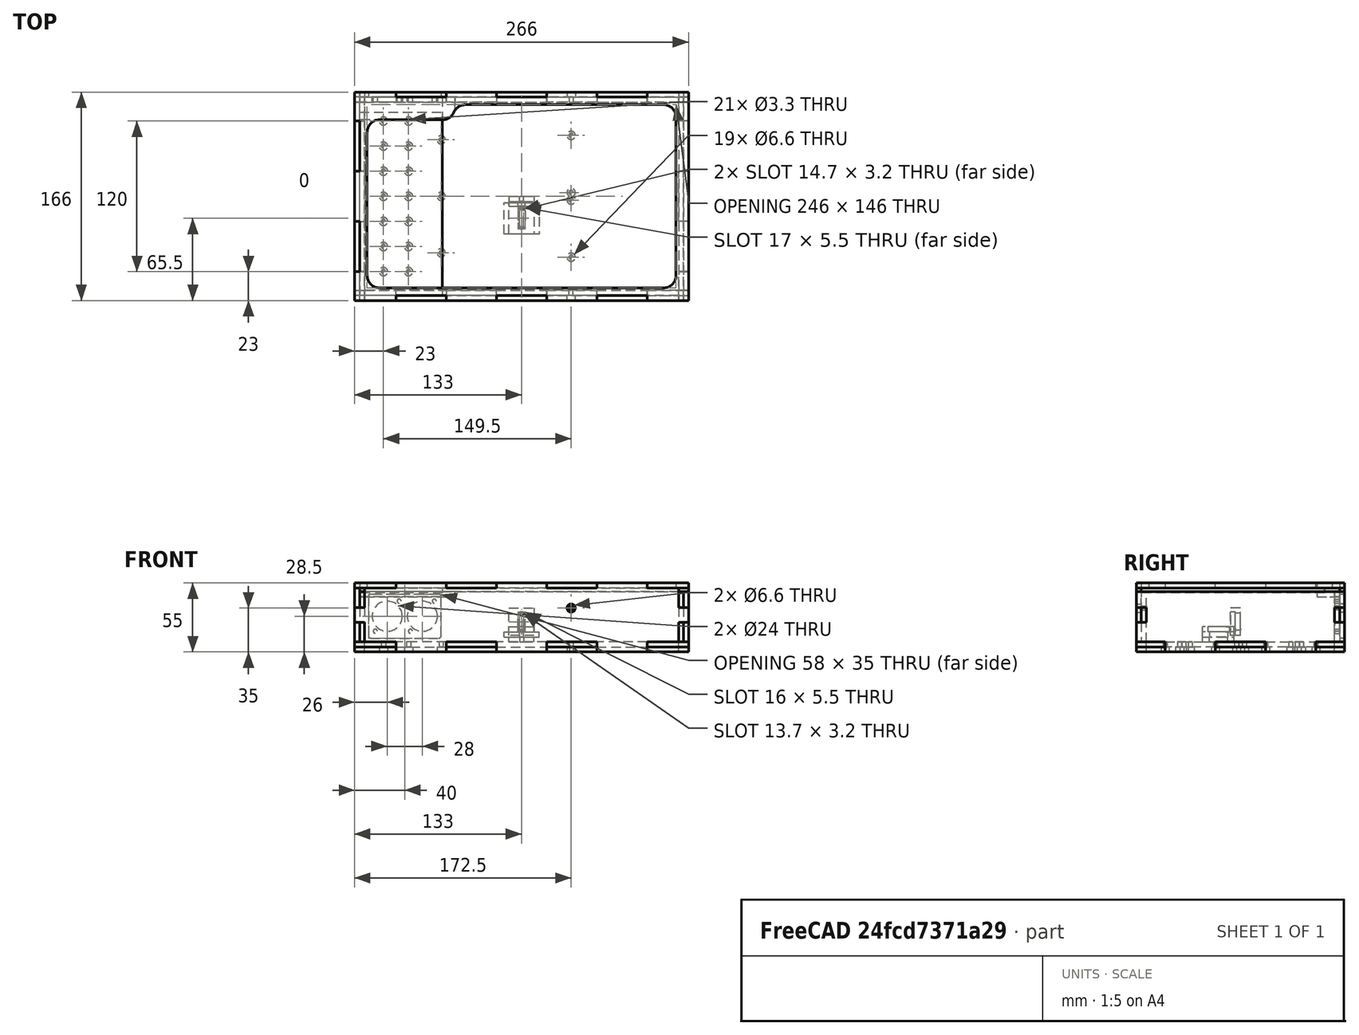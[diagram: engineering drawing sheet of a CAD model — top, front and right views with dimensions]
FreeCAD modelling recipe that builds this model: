
FCSTD DOCUMENT  (FreeCAD 0.17R13312 (Git))
Label: BreadBoardBox
License: All rights reserved
LicenseURL: http://en.wikipedia.org/wiki/All_rights_reserved
objects: Sketcher::SketchObject×62, PartDesign::ShapeBinder×61, PartDesign::Body×25, PartDesign::Pad×24, PartDesign::Pocket×24, TechDraw::DrawSVGTemplate×24, TechDraw::DrawViewPart×24, TechDraw::DrawPage×24, PartDesign::Plane×19, App::Part×18, PartDesign::FeatureBase×7, PartDesign::Hole×6, PartDesign::Mirrored×5, PartDesign::LinearPattern×5, PartDesign::MultiTransform×3, TechDraw::DrawViewDimension×3, App::DocumentObjectGroup×1
note: 295 computed .brp shape members not serialized (recipe doc carries the construction recipe); baked Part::Feature solids carry a one-line shape summary decoded from their .brp

FEATURE [Sketcher::SketchObject] Sketch  label="InsideSize_XY_Sketch"
  MapMode = 5
  Support = -> [XY_Plane026]
  sketch-geometry (4):
    g0: LineSegment StartX=-125 StartY=75 StartZ=0 EndX=125 EndY=75 EndZ=0
    g1: LineSegment StartX=125 StartY=75 StartZ=0 EndX=125 EndY=-75 EndZ=0
    g2: LineSegment StartX=125 StartY=-75 StartZ=0 EndX=-125 EndY=-75 EndZ=0
    g3: LineSegment StartX=-125 StartY=-75 StartZ=0 EndX=-125 EndY=75 EndZ=0
  constraints (11):
    c: Coincident(g0,g1)
    c: Coincident(g1,g2)
    c: Coincident(g2,g3)
    c: Coincident(g3,g0)
    c: Horizontal(g0)
    c: Horizontal(g2)
    c: Vertical(g1)
    c: Vertical(g3)
    c: Symmetric(g0,g2,g-1)
    c: DistanceX(g0,g0) = 250
    c: DistanceY(g1,g1) = 150
FEATURE [Sketcher::SketchObject] Sketch001  label="BaseIn_Sketch"
  MapMode = 5
  Support = -> [XY_Plane019]
  expr: Constraints[9] = 250 + 4 * 4
  expr: Constraints[8] = 150 + 4 * 4
  sketch-geometry (4):
    g0: LineSegment StartX=-133 StartY=83 StartZ=0 EndX=133 EndY=83 EndZ=0
    g1: LineSegment StartX=133 StartY=83 StartZ=0 EndX=133 EndY=-83 EndZ=0
    g2: LineSegment StartX=133 StartY=-83 StartZ=0 EndX=-133 EndY=-83 EndZ=0
    g3: LineSegment StartX=-133 StartY=-83 StartZ=0 EndX=-133 EndY=83 EndZ=0
  constraints (11):
    c: Coincident(g0,g1)
    c: Coincident(g1,g2)
    c: Coincident(g2,g3)
    c: Coincident(g3,g0)
    c: Horizontal(g0)
    c: Horizontal(g2)
    c: Vertical(g1)
    c: Vertical(g3)
    c: DistanceY(g1,g1) = 166
    c: DistanceX(g0,g0) = 266
    c: Symmetric(g2,g0,g-1)
FEATURE [PartDesign::Pad] Pad  label="BaseIn_Pad"
  Length = 4
  Length2 = 100
  Profile = -> Sketch001
  Reversed = true
  Type = 0
FEATURE [PartDesign::ShapeBinder] ShapeBinder
  Placement = pos=(0,0,-4) rot=(0,0,1;0rad)
  Support = -> [Pad]
FEATURE [PartDesign::Plane] DatumPlane
  MapMode = 5
  Placement = pos=(0,0,-4) rot=(0,0,1;3.14159rad)
  Support = -> [Pad]
FEATURE [Sketcher::SketchObject] Sketch002  label="BaseOut_Sketch"
  ExternalGeometry = -> [ShapeBinder]
  MapMode = 5
  Placement = pos=(0,0,-4) rot=(0,0,1;3.14159rad)
  Support = -> [DatumPlane]
  sketch-geometry (4):
    g0: LineSegment StartX=-133 StartY=83 StartZ=0 EndX=133 EndY=83 EndZ=0
    g1: LineSegment StartX=133 StartY=83 StartZ=0 EndX=133 EndY=-83 EndZ=0
    g2: LineSegment StartX=133 StartY=-83 StartZ=0 EndX=-133 EndY=-83 EndZ=0
    g3: LineSegment StartX=-133 StartY=-83 StartZ=0 EndX=-133 EndY=83 EndZ=0
  constraints (10):
    c: Coincident(g0,g1)
    c: Coincident(g1,g2)
    c: Coincident(g2,g3)
    c: Coincident(g3,g0)
    c: Horizontal(g0)
    c: Horizontal(g2)
    c: Vertical(g1)
    c: Vertical(g3)
    c: Coincident(g0,g-4)
    c: Coincident(g1,g-6)
FEATURE [PartDesign::Pad] Pad001  label="BaseOut_Pad"
  Length = 4
  Length2 = 100
  Placement = pos=(0,0,-4) rot=(0,0,1;3.14159rad)
  Profile = -> Sketch002
  Reversed = true
  Type = 0
FEATURE [Sketcher::SketchObject] Sketch003  label="InsideSize_XZ_Sketch"
  ExternalGeometry = -> [Sketch]
  MapMode = 5
  Placement = pos=(0,0,0) rot=(1,0,0;1.5708rad)
  Support = -> [XZ_Plane026]
  sketch-geometry (4):
    g0: LineSegment StartX=-125 StartY=40 StartZ=0 EndX=125 EndY=40 EndZ=0
    g1: LineSegment StartX=125 StartY=40 StartZ=0 EndX=125 EndY=0 EndZ=0
    g2: LineSegment StartX=125 StartY=0 StartZ=0 EndX=-125 EndY=0 EndZ=0
    g3: LineSegment StartX=-125 StartY=0 StartZ=0 EndX=-125 EndY=40 EndZ=0
  constraints (11):
    c: Coincident(g0,g1)
    c: Coincident(g1,g2)
    c: Coincident(g2,g3)
    c: Coincident(g3,g0)
    c: Horizontal(g0)
    c: Horizontal(g2)
    c: Vertical(g1)
    c: Vertical(g3)
    c: Coincident(g1,g-3)
    c: Coincident(g-3,g2)
    c: DistanceY(g3,g3) = 40
FEATURE [Sketcher::SketchObject] Sketch004  label="InsideSize_YZ_Sketch"
  ExternalGeometry = -> [Sketch003,Sketch]
  MapMode = 5
  Placement = pos=(0,0,0) rot=(0.57735,0.57735,0.57735;2.0944rad)
  Support = -> [YZ_Plane026]
  sketch-geometry (4):
    g0: LineSegment StartX=-75 StartY=40 StartZ=0 EndX=75 EndY=40 EndZ=0
    g1: LineSegment StartX=75 StartY=40 StartZ=0 EndX=75 EndY=0 EndZ=0
    g2: LineSegment StartX=75 StartY=0 StartZ=0 EndX=-75 EndY=0 EndZ=0
    g3: LineSegment StartX=-75 StartY=0 StartZ=0 EndX=-75 EndY=40 EndZ=0
  constraints (11):
    c: Coincident(g0,g1)
    c: Coincident(g1,g2)
    c: Coincident(g2,g3)
    c: Coincident(g3,g0)
    c: Horizontal(g0)
    c: Horizontal(g2)
    c: Vertical(g1)
    c: Vertical(g3)
    c: Coincident(g2,g-4)
    c: Coincident(g1,g-4)
    c: PointOnObject(g-3,g0)
FEATURE [PartDesign::Plane] DatumPlane001
  MapMode = 5
  Placement = pos=(0,83,0) rot=(1,0,0;1.5708rad)
  Support = -> [Pad]
FEATURE [PartDesign::ShapeBinder] ShapeBinder001
  Support = -> [Pad]
FEATURE [PartDesign::ShapeBinder] ShapeBinder002
  Placement = pos=(0,0,-4) rot=(0,0,1;3.14159rad)
  Support = -> [Pad001]
FEATURE [Sketcher::SketchObject] Sketch005  label="TopOut_Sketch"
  ExternalGeometry = -> [ShapeBinder001,ShapeBinder002]
  MapMode = 5
  Placement = pos=(0,83,0) rot=(1,0,0;1.5708rad)
  Support = -> [DatumPlane001]
  expr: Constraints[9] = 40 + 3 * 4 + 3
  sketch-geometry (4):
    g0: LineSegment StartX=-133 StartY=47 StartZ=0 EndX=133 EndY=47 EndZ=0
    g1: LineSegment StartX=133 StartY=47 StartZ=0 EndX=133 EndY=-8 EndZ=0
    g2: LineSegment StartX=133 StartY=-8 StartZ=0 EndX=-133 EndY=-8 EndZ=0
    g3: LineSegment StartX=-133 StartY=-8 StartZ=0 EndX=-133 EndY=47 EndZ=0
  constraints (11):
    c: Coincident(g0,g1)
    c: Coincident(g1,g2)
    c: Coincident(g2,g3)
    c: Coincident(g3,g0)
    c: Horizontal(g0)
    c: Horizontal(g2)
    c: Vertical(g1)
    c: Vertical(g3)
    c: Coincident(g1,g-4)
    c: DistanceY(g3,g3) = 55
    c: Coincident(g-4,g2)
FEATURE [PartDesign::Pad] Pad002  label="TopOut_Pad"
  Length = 4
  Length2 = 100
  Placement = pos=(0,83,0) rot=(1,0,0;1.5708rad)
  Profile = -> Sketch005
  Type = 0
FEATURE [PartDesign::ShapeBinder] ShapeBinder003
  Placement = pos=(0,-4,0) rot=(0,0,1;0rad)
  Support = -> [Pad002]
FEATURE [PartDesign::Plane] DatumPlane002  label="TopOut_inside_DatumPlane"
  MapMode = 5
  Placement = pos=(0,79,0) rot=(1,0,0;1.5708rad)
  Support = -> [Pad002]
FEATURE [Sketcher::SketchObject] Sketch006  label="TopIn_Sketch"
  ExternalGeometry = -> [ShapeBinder003]
  MapMode = 5
  Placement = pos=(0,79,0) rot=(1,0,0;1.5708rad)
  Support = -> [DatumPlane002]
  expr: Constraints[10] = 4 + 3
  sketch-geometry (4):
    g0: LineSegment StartX=-133 StartY=40 StartZ=0 EndX=133 EndY=40 EndZ=0
    g1: LineSegment StartX=133 StartY=40 StartZ=0 EndX=133 EndY=-8 EndZ=0
    g2: LineSegment StartX=133 StartY=-8 StartZ=0 EndX=-133 EndY=-8 EndZ=0
    g3: LineSegment StartX=-133 StartY=-8 StartZ=0 EndX=-133 EndY=40 EndZ=0
  constraints (11):
    c: Coincident(g0,g1)
    c: Coincident(g1,g2)
    c: Coincident(g2,g3)
    c: Coincident(g3,g0)
    c: Horizontal(g0)
    c: Horizontal(g2)
    c: Vertical(g1)
    c: Vertical(g3)
    c: Coincident(g1,g-6)
    c: PointOnObject(g0,g-3)
    c: DistanceY(g0,g-4) = 7
FEATURE [PartDesign::Pad] Pad003  label="TopIn_Pad"
  Length = 4
  Length2 = 100
  Placement = pos=(0,79,0) rot=(1,0,0;1.5708rad)
  Profile = -> Sketch006
  Type = 0
FEATURE [PartDesign::Plane] DatumPlane003
  MapMode = 5
  Placement = pos=(-133,0,-4) rot=(0.57735,0.57735,0.57735;2.0944rad)
  Support = -> [Pad001]
FEATURE [PartDesign::ShapeBinder] ShapeBinder004
  Placement = pos=(0,0,-4) rot=(0,0,1;3.14159rad)
  Support = -> [Pad001]
FEATURE [PartDesign::ShapeBinder] ShapeBinder005
  Placement = pos=(0,83,0) rot=(1,0,0;1.5708rad)
  Support = -> [Pad002]
FEATURE [Sketcher::SketchObject] Sketch007  label="LeftOut_Sketch"
  ExternalGeometry = -> [ShapeBinder004,ShapeBinder005]
  MapMode = 5
  Placement = pos=(-133,0,-4) rot=(0.57735,0.57735,0.57735;2.0944rad)
  Support = -> [DatumPlane003]
  sketch-geometry (4):
    g0: LineSegment StartX=-83 StartY=51 StartZ=0 EndX=83 EndY=51 EndZ=0
    g1: LineSegment StartX=83 StartY=51 StartZ=0 EndX=83 EndY=-4 EndZ=0
    g2: LineSegment StartX=83 StartY=-4 StartZ=0 EndX=-83 EndY=-4 EndZ=0
    g3: LineSegment StartX=-83 StartY=-4 StartZ=0 EndX=-83 EndY=51 EndZ=0
  constraints (10):
    c: Coincident(g0,g1)
    c: Coincident(g1,g2)
    c: Coincident(g2,g3)
    c: Coincident(g3,g0)
    c: Horizontal(g0)
    c: Horizontal(g2)
    c: Vertical(g1)
    c: Vertical(g3)
    c: Coincident(g0,g-4)
    c: Coincident(g2,g-3)
FEATURE [PartDesign::Pad] Pad004  label="LeftOut_Pad"
  Length = 4
  Length2 = 100
  Placement = pos=(-133,0,-4) rot=(0.57735,0.57735,0.57735;2.0944rad)
  Profile = -> Sketch007
  Type = 0
FEATURE [PartDesign::Plane] DatumPlane004
  MapMode = 5
  Placement = pos=(-129,0,-4) rot=(0.57735,0.57735,0.57735;2.0944rad)
  Support = -> [Pad004]
FEATURE [PartDesign::ShapeBinder] ShapeBinder006
  Placement = pos=(4,0,0) rot=(0,0,1;0rad)
  Support = -> [Pad004]
FEATURE [PartDesign::ShapeBinder] ShapeBinder007
  Placement = pos=(0,-4,0) rot=(0,0,1;0rad)
  Support = -> [Pad003]
FEATURE [Sketcher::SketchObject] Sketch008  label="LeftIn_Sketch"
  ExternalGeometry = -> [ShapeBinder007,ShapeBinder006]
  MapMode = 5
  Placement = pos=(-129,0,-4) rot=(0.57735,0.57735,0.57735;2.0944rad)
  Support = -> [DatumPlane004]
  sketch-geometry (4):
    g0: LineSegment StartX=-83 StartY=44 StartZ=0 EndX=83 EndY=44 EndZ=0
    g1: LineSegment StartX=83 StartY=44 StartZ=0 EndX=83 EndY=-4 EndZ=0
    g2: LineSegment StartX=83 StartY=-4 StartZ=0 EndX=-83 EndY=-4 EndZ=0
    g3: LineSegment StartX=-83 StartY=-4 StartZ=0 EndX=-83 EndY=44 EndZ=0
  constraints (11):
    c: Coincident(g0,g1)
    c: Coincident(g1,g2)
    c: Coincident(g2,g3)
    c: Coincident(g3,g0)
    c: Horizontal(g0)
    c: Horizontal(g2)
    c: Vertical(g1)
    c: Vertical(g3)
    c: Coincident(g2,g-4)
    c: PointOnObject(g0,g-5)
    c: PointOnObject(g-3,g0)
FEATURE [PartDesign::Pad] Pad005  label="LeftIn_Pad"
  Length = 4
  Length2 = 100
  Placement = pos=(-129,0,-4) rot=(0.57735,0.57735,0.57735;2.0944rad)
  Profile = -> Sketch008
  Type = 0
FEATURE [PartDesign::Plane] DatumPlane005
  MapMode = 5
  Placement = pos=(133,0,-4) rot=(0.57735,-0.57735,-0.57735;2.0944rad)
  Support = -> [Pad001]
FEATURE [PartDesign::ShapeBinder] ShapeBinder008
  Placement = pos=(0,0,-4) rot=(0,0,1;3.14159rad)
  Support = -> [Pad001]
FEATURE [PartDesign::ShapeBinder] ShapeBinder009
  Placement = pos=(0,83,0) rot=(1,0,0;1.5708rad)
  Support = -> [Pad002]
FEATURE [PartDesign::ShapeBinder] ShapeBinder010
  Placement = pos=(0,79,0) rot=(1,0,0;1.5708rad)
  Support = -> [Pad003]
FEATURE [Sketcher::SketchObject] Sketch009  label="RightOut_Sketch"
  ExternalGeometry = -> [ShapeBinder008,ShapeBinder009,ShapeBinder010]
  MapMode = 5
  Placement = pos=(133,0,-4) rot=(0.57735,-0.57735,-0.57735;2.0944rad)
  Support = -> [DatumPlane005]
  sketch-geometry (4):
    g0: LineSegment StartX=-83 StartY=44 StartZ=0 EndX=83 EndY=44 EndZ=0
    g1: LineSegment StartX=83 StartY=44 StartZ=0 EndX=83 EndY=-4 EndZ=0
    g2: LineSegment StartX=83 StartY=-4 StartZ=0 EndX=-83 EndY=-4 EndZ=0
    g3: LineSegment StartX=-83 StartY=-4 StartZ=0 EndX=-83 EndY=44 EndZ=0
  constraints (11):
    c: Coincident(g0,g1)
    c: Coincident(g1,g2)
    c: Coincident(g2,g3)
    c: Coincident(g3,g0)
    c: Horizontal(g0)
    c: Horizontal(g2)
    c: Vertical(g1)
    c: Vertical(g3)
    c: Coincident(g1,g-3)
    c: PointOnObject(g0,g-4)
    c: PointOnObject(g-5,g0)
FEATURE [PartDesign::Pad] Pad006  label="RightOut_Pad"
  Length = 4
  Length2 = 100
  Placement = pos=(133,0,-4) rot=(0.57735,-0.57735,-0.57735;2.0944rad)
  Profile = -> Sketch009
  Type = 0
FEATURE [PartDesign::Plane] DatumPlane006
  MapMode = 5
  Placement = pos=(129,0,-4) rot=(0.57735,-0.57735,-0.57735;2.0944rad)
  Support = -> [Pad006]
FEATURE [PartDesign::ShapeBinder] ShapeBinder011
  Placement = pos=(-4,0,0) rot=(0,0,1;0rad)
  Support = -> [Pad006]
FEATURE [Sketcher::SketchObject] Sketch010  label="RightIn_Sketch"
  ExternalGeometry = -> [ShapeBinder011]
  MapMode = 5
  Placement = pos=(129,0,-4) rot=(0.57735,-0.57735,-0.57735;2.0944rad)
  Support = -> [DatumPlane006]
  sketch-geometry (4):
    g0: LineSegment StartX=-83 StartY=44 StartZ=0 EndX=83 EndY=44 EndZ=0
    g1: LineSegment StartX=83 StartY=44 StartZ=0 EndX=83 EndY=-4 EndZ=0
    g2: LineSegment StartX=83 StartY=-4 StartZ=0 EndX=-83 EndY=-4 EndZ=0
    g3: LineSegment StartX=-83 StartY=-4 StartZ=0 EndX=-83 EndY=44 EndZ=0
  constraints (10):
    c: Coincident(g0,g1)
    c: Coincident(g1,g2)
    c: Coincident(g2,g3)
    c: Coincident(g3,g0)
    c: Horizontal(g0)
    c: Horizontal(g2)
    c: Vertical(g1)
    c: Vertical(g3)
    c: Coincident(g0,g-4)
    c: Coincident(g2,g-3)
FEATURE [PartDesign::Pad] Pad007  label="RightIn_Pad"
  Length = 4
  Length2 = 100
  Placement = pos=(129,0,-4) rot=(0.57735,-0.57735,-0.57735;2.0944rad)
  Profile = -> Sketch010
  Type = 0
FEATURE [PartDesign::Plane] DatumPlane007
  MapMode = 5
  Placement = pos=(0,-83,-4) rot=(0,0.707107,0.707107;3.14159rad)
  Support = -> [Pad001]
FEATURE [PartDesign::ShapeBinder] ShapeBinder012
  Placement = pos=(0,0,-4) rot=(0,0,1;3.14159rad)
  Support = -> [Pad001]
FEATURE [PartDesign::ShapeBinder] ShapeBinder013
  Placement = pos=(-133,0,-4) rot=(0.57735,0.57735,0.57735;2.0944rad)
  Support = -> [Pad004]
FEATURE [Sketcher::SketchObject] Sketch011  label="BottomOut_Sketch"
  ExternalGeometry = -> [ShapeBinder013,ShapeBinder012]
  MapMode = 5
  Placement = pos=(0,-83,-4) rot=(0,0.707107,0.707107;3.14159rad)
  Support = -> [DatumPlane007]
  sketch-geometry (4):
    g0: LineSegment StartX=-133 StartY=51 StartZ=0 EndX=133 EndY=51 EndZ=0
    g1: LineSegment StartX=133 StartY=51 StartZ=0 EndX=133 EndY=-4 EndZ=0
    g2: LineSegment StartX=133 StartY=-4 StartZ=0 EndX=-133 EndY=-4 EndZ=0
    g3: LineSegment StartX=-133 StartY=-4 StartZ=0 EndX=-133 EndY=51 EndZ=0
  constraints (10):
    c: Coincident(g0,g1)
    c: Coincident(g1,g2)
    c: Coincident(g2,g3)
    c: Coincident(g3,g0)
    c: Horizontal(g0)
    c: Horizontal(g2)
    c: Vertical(g1)
    c: Vertical(g3)
    c: Coincident(g0,g-3)
    c: Coincident(g2,g-4)
FEATURE [PartDesign::Pad] Pad008  label="BottomOut_Pad"
  Length = 4
  Length2 = 100
  Placement = pos=(0,-83,-4) rot=(0,0.707107,0.707107;3.14159rad)
  Profile = -> Sketch011
  Type = 0
FEATURE [PartDesign::Plane] DatumPlane008
  MapMode = 5
  Placement = pos=(0,-79,-4) rot=(0,0.707107,0.707107;3.14159rad)
  Support = -> [Pad008]
FEATURE [PartDesign::ShapeBinder] ShapeBinder014
  Placement = pos=(0,4,0) rot=(0,0,1;0rad)
  Support = -> [Pad008]
FEATURE [PartDesign::ShapeBinder] ShapeBinder015
  Placement = pos=(-129,0,-4) rot=(0.57735,0.57735,0.57735;2.0944rad)
  Support = -> [Pad005]
FEATURE [Sketcher::SketchObject] Sketch012  label="BottomIn_Sketch"
  ExternalGeometry = -> [ShapeBinder015,ShapeBinder014]
  MapMode = 5
  Placement = pos=(0,-79,-4) rot=(0,0.707107,0.707107;3.14159rad)
  Support = -> [DatumPlane008]
  sketch-geometry (4):
    g0: LineSegment StartX=-133 StartY=44 StartZ=0 EndX=133 EndY=44 EndZ=0
    g1: LineSegment StartX=133 StartY=44 StartZ=0 EndX=133 EndY=-4 EndZ=0
    g2: LineSegment StartX=133 StartY=-4 StartZ=0 EndX=-133 EndY=-4 EndZ=0
    g3: LineSegment StartX=-133 StartY=-4 StartZ=0 EndX=-133 EndY=44 EndZ=0
  constraints (11):
    c: Coincident(g0,g1)
    c: Coincident(g1,g2)
    c: Coincident(g2,g3)
    c: Coincident(g3,g0)
    c: Horizontal(g0)
    c: Horizontal(g2)
    c: Vertical(g1)
    c: Vertical(g3)
    c: Coincident(g1,g-5)
    c: Coincident(g2,g-4)
    c: PointOnObject(g-3,g0)
FEATURE [PartDesign::Pad] Pad009  label="BottomIn_Pad"
  Length = 4
  Length2 = 100
  Placement = pos=(0,-79,-4) rot=(0,0.707107,0.707107;3.14159rad)
  Profile = -> Sketch012
  Type = 0
FEATURE [PartDesign::Plane] DatumPlane009
  MapMode = 45
  Placement = pos=(-31.1547,0,47) rot=(-0.707107,0.707107,0;3.14159rad)
  Support = -> [Pad008,Pad002,Pad004]
FEATURE [PartDesign::ShapeBinder] ShapeBinder016
  Support = -> [Pad004,Pad008,Pad002]
FEATURE [PartDesign::ShapeBinder] ShapeBinder017
  Placement = pos=(0,-83,-4) rot=(0,0.707107,0.707107;3.14159rad)
  Support = -> [Pad008]
FEATURE [PartDesign::ShapeBinder] ShapeBinder018
  Placement = pos=(0,83,0) rot=(1,0,0;1.5708rad)
  Support = -> [Pad002]
FEATURE [Sketcher::SketchObject] Sketch013  label="LidOut_Sketch"
  ExternalGeometry = -> [ShapeBinder018,ShapeBinder016,ShapeBinder017]
  MapMode = 5
  Placement = pos=(-31.1547,0,47) rot=(-0.707107,0.707107,0;3.14159rad)
  Support = -> [DatumPlane009]
  sketch-geometry (4):
    g0: LineSegment StartX=-83 StartY=101.845 StartZ=0 EndX=83 EndY=101.845 EndZ=0
    g1: LineSegment StartX=83 StartY=101.845 StartZ=0 EndX=83 EndY=-164.155 EndZ=0
    g2: LineSegment StartX=83 StartY=-164.155 StartZ=0 EndX=-83 EndY=-164.155 EndZ=0
    g3: LineSegment StartX=-83 StartY=-164.155 StartZ=0 EndX=-83 EndY=101.845 EndZ=0
  constraints (10):
    c: Coincident(g0,g1)
    c: Coincident(g1,g2)
    c: Coincident(g2,g3)
    c: Coincident(g3,g0)
    c: Horizontal(g0)
    c: Horizontal(g2)
    c: Vertical(g1)
    c: Vertical(g3)
    c: Coincident(g0,g-4)
    c: Coincident(g1,g-5)
FEATURE [PartDesign::Pad] Pad010  label="LidOut_Pad"
  Length = 4
  Length2 = 100
  Placement = pos=(-31.1547,0,47) rot=(0.707107,-0.707107,0;3.14159rad)
  Profile = -> Sketch013
  Type = 0
FEATURE [PartDesign::Plane] DatumPlane010
  MapMode = 5
  Placement = pos=(-31.1547,0,43) rot=(0.707107,-0.707107,0;3.14159rad)
  Support = -> [Pad010]
FEATURE [PartDesign::ShapeBinder] ShapeBinder019
  Placement = pos=(0,79,0) rot=(1,0,0;1.5708rad)
  Support = -> [Pad003]
FEATURE [PartDesign::ShapeBinder] ShapeBinder020
  Placement = pos=(-129,0,-4) rot=(0.57735,0.57735,0.57735;2.0944rad)
  Support = -> [Pad005]
FEATURE [PartDesign::ShapeBinder] ShapeBinder021
  Placement = pos=(0,-79,-4) rot=(0,0.707107,0.707107;3.14159rad)
  Support = -> [Pad009]
FEATURE [PartDesign::ShapeBinder] ShapeBinder022
  Placement = pos=(133,0,-4) rot=(0.57735,-0.57735,-0.57735;2.0944rad)
  Support = -> [Pad006]
FEATURE [PartDesign::ShapeBinder] ShapeBinder023
  Placement = pos=(129,0,-4) rot=(0.57735,-0.57735,-0.57735;2.0944rad)
  Support = -> [Pad007]
FEATURE [Sketcher::SketchObject] Sketch015  label="BaseOut_Locks_Sketch"
  ExternalGeometry = -> [Pad001]
  MapMode = 5
  Placement = pos=(0,0,-8) rot=(0,1,0;3.14159rad)
  Support = -> [Pad001]
  sketch-geometry (28):
    g0: LineSegment StartX=-100 StartY=105 StartZ=0 EndX=-60 EndY=105 EndZ=0
    g1: LineSegment StartX=-60 StartY=105 StartZ=0 EndX=-60 EndY=75 EndZ=0
    g2: LineSegment StartX=-60 StartY=75 StartZ=0 EndX=-100 EndY=75 EndZ=0
    g3: LineSegment StartX=-100 StartY=75 StartZ=0 EndX=-100 EndY=105 EndZ=0
    g4: LineSegment StartX=-20 StartY=105 StartZ=0 EndX=20 EndY=105 EndZ=0
    g5: LineSegment StartX=20 StartY=105 StartZ=0 EndX=20 EndY=75 EndZ=0
    g6: LineSegment StartX=20 StartY=75 StartZ=0 EndX=-20 EndY=75 EndZ=0
    g7: LineSegment StartX=-20 StartY=75 StartZ=0 EndX=-20 EndY=105 EndZ=0
    g8: LineSegment StartX=60 StartY=105 StartZ=0 EndX=100 EndY=105 EndZ=0
    g9: LineSegment StartX=100 StartY=105 StartZ=0 EndX=100 EndY=75 EndZ=0
    g10: LineSegment StartX=100 StartY=75 StartZ=0 EndX=60 EndY=75 EndZ=0
    g11: LineSegment StartX=60 StartY=75 StartZ=0 EndX=60 EndY=105 EndZ=0
    g12: LineSegment [constr] StartX=-60 StartY=75 StartZ=0 EndX=-20 EndY=75 EndZ=0
    g13: LineSegment [constr] StartX=20 StartY=75 StartZ=0 EndX=60 EndY=75 EndZ=0
    g14: LineSegment [constr] StartX=-133 StartY=75 StartZ=0 EndX=-100 EndY=75 EndZ=0
    g15: LineSegment [constr] StartX=100 StartY=75 StartZ=0 EndX=133 EndY=75 EndZ=0
    g16: LineSegment StartX=-155 StartY=60 StartZ=0 EndX=-125 EndY=60 EndZ=0
    g17: LineSegment StartX=-125 StartY=60 StartZ=0 EndX=-125 EndY=20 EndZ=0
    g18: LineSegment StartX=-125 StartY=20 StartZ=0 EndX=-155 EndY=20 EndZ=0
    g19: LineSegment StartX=-155 StartY=20 StartZ=0 EndX=-155 EndY=60 EndZ=0
    g20: LineSegment StartX=-155 StartY=-20 StartZ=0 EndX=-125 EndY=-20 EndZ=0
    g21: LineSegment StartX=-125 StartY=-20 StartZ=0 EndX=-125 EndY=-60 EndZ=0
    g22: LineSegment StartX=-125 StartY=-60 StartZ=0 EndX=-155 EndY=-60 EndZ=0
    g23: LineSegment StartX=-155 StartY=-60 StartZ=0 EndX=-155 EndY=-20 EndZ=0
    g24: LineSegment [constr] StartX=-125 StartY=60 StartZ=0 EndX=-125 EndY=83 EndZ=0
    g25: LineSegment [constr] StartX=-125 StartY=-60 StartZ=0 EndX=-125 EndY=-83 EndZ=0
    g26: LineSegment [constr] StartX=-125 StartY=20 StartZ=0 EndX=-125 EndY=-20 EndZ=0
    g27: GeomPoint X=0 Y=0 Z=0
  constraints (79):
    c: Coincident(g0,g1)
    c: Coincident(g1,g2)
    c: Coincident(g2,g3)
    c: Coincident(g3,g0)
    c: Horizontal(g0)
    c: Horizontal(g2)
    c: Vertical(g1)
    c: Vertical(g3)
    c: Coincident(g4,g5)
    c: Coincident(g5,g6)
    c: Coincident(g6,g7)
    c: Coincident(g7,g4)
    c: Horizontal(g4)
    c: Horizontal(g6)
    c: Vertical(g5)
    c: Vertical(g7)
    c: Coincident(g8,g9)
    c: Coincident(g9,g10)
    c: Coincident(g10,g11)
    c: Coincident(g11,g8)
    c: Horizontal(g8)
    c: Horizontal(g10)
    c: Vertical(g9)
    c: Vertical(g11)
    c: Equal(g2,g6)
    c: Equal(g6,g10)
    c: Coincident(g12,g1)
    c: Horizontal(g12)
    c: Coincident(g13,g5)
    c: Coincident(g13,g10)
    c: Horizontal(g13)
    c: Coincident(g6,g12)
    c: Equal(g3,g7)
    c: Equal(g7,g11)
    c: DistanceY(g3,g3) = 30
    c: Equal(g12,g13)
    c: Horizontal(g14)
    c: Horizontal(g15)
    c: Coincident(g9,g15)
    c: PointOnObject(g15,g-4)
    c: Equal(g15,g14)
    c: Coincident(g2,g14)
    c: PointOnObject(g14,g-5)
    c: DistanceY(g14,g-5) = 8
    c: Equal(g2,g12)
    c: DistanceX(g2,g2) = 40
    c: Coincident(g16,g17)
    c: Coincident(g17,g18)
    c: Coincident(g18,g19)
    c: Coincident(g19,g16)
    c: Horizontal(g16)
    c: Horizontal(g18)
    c: Vertical(g17)
    c: Vertical(g19)
    c: Coincident(g20,g21)
    c: Coincident(g21,g22)
    c: Coincident(g22,g23)
    c: Coincident(g23,g20)
    c: Horizontal(g20)
    c: Horizontal(g22)
    c: Vertical(g21)
    c: Vertical(g23)
    c: Equal(g16,g20)
    c: Equal(g20,g3)
    c: Equal(g17,g2)
    c: Equal(g2,g21)
    c: Coincident(g24,g16)
    c: PointOnObject(g24,g-3)
    c: Vertical(g24)
    c: Coincident(g25,g21)
    c: PointOnObject(g25,g-6)
    c: Vertical(g25)
    c: Equal(g25,g24)
    c: Coincident(g26,g17)
    c: Vertical(g26)
    c: Coincident(g20,g26)
    c: Equal(g26,g2)
    c: DistanceX(g-5,g24) = 8
    c: Coincident(g27,g-1)
FEATURE [PartDesign::Pocket] Pocket  label="BaseOut_Locks_Pocket"
  BaseFeature = -> Pad001
  Length = 5
  Length2 = 100
  Placement = pos=(0,0,-4) rot=(0,0,1;3.14159rad)
  Profile = -> Sketch015
  Type = 1
FEATURE [PartDesign::Mirrored] Mirrored  label="BaseOut_Locks_MirroredY"
  BaseFeature = -> Pocket
  MirrorPlane = -> Sketch015 [V_Axis]
  Originals = -> [Pocket]
  Placement = pos=(0,0,-4) rot=(0,0,1;3.14159rad)
FEATURE [PartDesign::Mirrored] Mirrored001  label=" BaseOut_Locks_MirroredX"
  BaseFeature = -> Mirrored
  MirrorPlane = -> Sketch015 [H_Axis]
  Originals = -> [Pocket]
  Placement = pos=(0,0,-4) rot=(0,0,1;3.14159rad)
FEATURE [PartDesign::ShapeBinder] ShapeBinder024
  Placement = pos=(0,0,-8) rot=(0,1,0;3.14159rad)
  Support = -> [Sketch015]
FEATURE [Sketcher::SketchObject] Sketch016  label="BaseIn_Locks_Sketch"
  ExternalGeometry = -> [ShapeBinder024]
  MapMode = 5
  Placement = pos=(0,0,-4) rot=(1,0,0;3.14159rad)
  Support = -> [Pad]
  sketch-geometry (20):
    g0: LineSegment StartX=125 StartY=20 StartZ=0 EndX=155 EndY=20 EndZ=0
    g1: LineSegment StartX=155 StartY=20 StartZ=0 EndX=155 EndY=60 EndZ=0
    g2: LineSegment StartX=155 StartY=60 StartZ=0 EndX=125 EndY=60 EndZ=0
    g3: LineSegment StartX=125 StartY=60 StartZ=0 EndX=125 EndY=20 EndZ=0
    g4: LineSegment StartX=125 StartY=-60 StartZ=0 EndX=155 EndY=-60 EndZ=0
    g5: LineSegment StartX=155 StartY=-60 StartZ=0 EndX=155 EndY=-20 EndZ=0
    g6: LineSegment StartX=155 StartY=-20 StartZ=0 EndX=125 EndY=-20 EndZ=0
    g7: LineSegment StartX=125 StartY=-20 StartZ=0 EndX=125 EndY=-60 EndZ=0
    g8: LineSegment StartX=60 StartY=-105 StartZ=0 EndX=100 EndY=-105 EndZ=0
    g9: LineSegment StartX=100 StartY=-105 StartZ=0 EndX=100 EndY=-75 EndZ=0
    g10: LineSegment StartX=100 StartY=-75 StartZ=0 EndX=60 EndY=-75 EndZ=0
    g11: LineSegment StartX=60 StartY=-75 StartZ=0 EndX=60 EndY=-105 EndZ=0
    g12: LineSegment StartX=-20 StartY=-105 StartZ=0 EndX=20 EndY=-105 EndZ=0
    g13: LineSegment StartX=20 StartY=-105 StartZ=0 EndX=20 EndY=-75 EndZ=0
    g14: LineSegment StartX=20 StartY=-75 StartZ=0 EndX=-20 EndY=-75 EndZ=0
    g15: LineSegment StartX=-20 StartY=-75 StartZ=0 EndX=-20 EndY=-105 EndZ=0
    g16: LineSegment StartX=-100 StartY=-105 StartZ=0 EndX=-60 EndY=-105 EndZ=0
    g17: LineSegment StartX=-60 StartY=-105 StartZ=0 EndX=-60 EndY=-75 EndZ=0
    g18: LineSegment StartX=-60 StartY=-75 StartZ=0 EndX=-100 EndY=-75 EndZ=0
    g19: LineSegment StartX=-100 StartY=-75 StartZ=0 EndX=-100 EndY=-105 EndZ=0
  constraints (50):
    c: Coincident(g0,g1)
    c: Coincident(g1,g2)
    c: Coincident(g2,g3)
    c: Coincident(g3,g0)
    c: Horizontal(g0)
    c: Horizontal(g2)
    c: Vertical(g1)
    c: Vertical(g3)
    c: Coincident(g0,g-5)
    c: Coincident(g1,g-6)
    c: Coincident(g4,g5)
    c: Coincident(g5,g6)
    c: Coincident(g6,g7)
    c: Coincident(g7,g4)
    c: Horizontal(g4)
    c: Horizontal(g6)
    c: Vertical(g5)
    c: Vertical(g7)
    c: Coincident(g4,g-3)
    c: Coincident(g5,g-4)
    c: Coincident(g8,g9)
    c: Coincident(g9,g10)
    c: Coincident(g10,g11)
    c: Coincident(g11,g8)
    c: Horizontal(g8)
    c: Horizontal(g10)
    c: Vertical(g9)
    c: Vertical(g11)
    c: Coincident(g8,g-8)
    c: Coincident(g9,g-7)
    c: Coincident(g12,g13)
    c: Coincident(g13,g14)
    c: Coincident(g14,g15)
    c: Coincident(g15,g12)
    c: Horizontal(g12)
    c: Horizontal(g14)
    c: Vertical(g13)
    c: Vertical(g15)
    c: Coincident(g12,g-10)
    c: Coincident(g13,g-9)
    c: Coincident(g16,g17)
    c: Coincident(g17,g18)
    c: Coincident(g18,g19)
    c: Coincident(g19,g16)
    c: Horizontal(g16)
    c: Horizontal(g18)
    c: Vertical(g17)
    c: Vertical(g19)
    c: Coincident(g16,g-12)
    c: Coincident(g17,g-11)
FEATURE [PartDesign::Pocket] Pocket001  label="BaseIn_Locks_Pocket"
  BaseFeature = -> Pad
  Length = 5
  Length2 = 100
  Profile = -> Sketch016
  Type = 1
FEATURE [PartDesign::Mirrored] Mirrored002  label="BaseIn_Locks_MirroredX"
  MirrorPlane = -> Sketch016 [V_Axis]
FEATURE [PartDesign::Mirrored] Mirrored003  label="BaseIn_Locks_MirroredY"
  MirrorPlane = -> Sketch016 [H_Axis]
FEATURE [PartDesign::MultiTransform] MultiTransform  label="BaseIn_Locks_MultiTransform"
  BaseFeature = -> Pocket001
  Originals = -> [Pocket001]
  Transformations = -> [Mirrored002,Mirrored003]
FEATURE [PartDesign::ShapeBinder] ShapeBinder025
  Placement = pos=(0,0,-8) rot=(0,1,0;3.14159rad)
  Support = -> [Sketch015]
FEATURE [Sketcher::SketchObject] Sketch017  label="LidOut_Locks_Sketch"
  ExternalGeometry = -> [ShapeBinder025]
  MapMode = 5
  Placement = pos=(-31.1547,0,47) rot=(0,0,-1;1.5708rad)
  Support = -> [Pad010]
  sketch-geometry (13):
    g0: LineSegment StartX=-105 StartY=131.155 StartZ=0 EndX=-79 EndY=131.155 EndZ=0
    g1: LineSegment StartX=-79 StartY=131.155 StartZ=0 EndX=-79 EndY=91.1547 EndZ=0
    g2: LineSegment StartX=-79 StartY=91.1547 StartZ=0 EndX=-105 EndY=91.1547 EndZ=0
    g3: LineSegment StartX=-105 StartY=91.1547 StartZ=0 EndX=-105 EndY=131.155 EndZ=0
    g4: LineSegment StartX=-105 StartY=51.1547 StartZ=0 EndX=-79 EndY=51.1547 EndZ=0
    g5: LineSegment StartX=-79 StartY=51.1547 StartZ=0 EndX=-79 EndY=11.1547 EndZ=0
    g6: LineSegment StartX=-79 StartY=11.1547 StartZ=0 EndX=-105 EndY=11.1547 EndZ=0
    g7: LineSegment StartX=-105 StartY=11.1547 StartZ=0 EndX=-105 EndY=51.1547 EndZ=0
    g8: LineSegment StartX=-105 StartY=-28.8453 StartZ=0 EndX=-79 EndY=-28.8453 EndZ=0
    g9: LineSegment StartX=-79 StartY=-28.8453 StartZ=0 EndX=-79 EndY=-68.8453 EndZ=0
    g10: LineSegment StartX=-79 StartY=-68.8453 StartZ=0 EndX=-105 EndY=-68.8453 EndZ=0
    g11: LineSegment StartX=-105 StartY=-68.8453 StartZ=0 EndX=-105 EndY=-28.8453 EndZ=0
    g12: LineSegment [constr] StartX=-79 StartY=91.1547 StartZ=0 EndX=-79 EndY=-28.8453 EndZ=0
  constraints (36):
    c: Coincident(g0,g1)
    c: Coincident(g1,g2)
    c: Coincident(g2,g3)
    c: Coincident(g3,g0)
    c: Horizontal(g0)
    c: Horizontal(g2)
    c: Vertical(g1)
    c: Vertical(g3)
    c: Coincident(g0,g-3)
    c: Coincident(g4,g5)
    c: Coincident(g5,g6)
    c: Coincident(g6,g7)
    c: Coincident(g7,g4)
    c: Horizontal(g4)
    c: Horizontal(g6)
    c: Vertical(g5)
    c: Vertical(g7)
    c: Coincident(g4,g-5)
    c: Coincident(g8,g9)
    c: Coincident(g9,g10)
    c: Coincident(g10,g11)
    c: Horizontal(g8)
    c: Horizontal(g10)
    c: Vertical(g9)
    c: Vertical(g11)
    c: Coincident(g8,g-7)
    c: Coincident(g12,g8)
    c: Vertical(g12)
    c: PointOnObject(g1,g-4)
    c: PointOnObject(g1,g12)
    c: DistanceX(g12,g-3) = 4
    c: Coincident(g12,g1)
    c: Coincident(g8,g11)
    c: PointOnObject(g9,g-8)
    c: PointOnObject(g5,g-6)
    c: PointOnObject(g5,g12)
FEATURE [PartDesign::Pocket] Pocket002  label="LidOut_Locks_Pocket"
  BaseFeature = -> Pad010
  Length = 5
  Length2 = 100
  Placement = pos=(-31.1547,0,47) rot=(0.707107,-0.707107,0;3.14159rad)
  Profile = -> Sketch017
  Type = 1
FEATURE [PartDesign::Mirrored] Mirrored004  label="LidOut_Locks_MirroredX"
  BaseFeature = -> Pocket002
  MirrorPlane = -> Sketch017 [V_Axis]
  Originals = -> [Pocket002]
  Placement = pos=(-31.1547,0,47) rot=(0.707107,-0.707107,0;3.14159rad)
FEATURE [Sketcher::SketchObject] Sketch018  label="LidOut_LocksLeft_Sketch"
  ExternalGeometry = -> [ShapeBinder025,Mirrored004]
  MapMode = 5
  Placement = pos=(-31.1547,0,47) rot=(0,0,-1;1.5708rad)
  Support = -> [Mirrored004]
  sketch-geometry (9):
    g0: LineSegment StartX=-60 StartY=-97.8453 StartZ=0 EndX=-20 EndY=-97.8453 EndZ=0
    g1: LineSegment StartX=-20 StartY=-97.8453 StartZ=0 EndX=-20 EndY=-127.845 EndZ=0
    g2: LineSegment StartX=-20 StartY=-127.845 StartZ=0 EndX=-60 EndY=-127.845 EndZ=0
    g3: LineSegment StartX=-60 StartY=-127.845 StartZ=0 EndX=-60 EndY=-97.8453 EndZ=0
    g4: LineSegment StartX=20 StartY=-97.8453 StartZ=0 EndX=60 EndY=-97.8453 EndZ=0
    g5: LineSegment StartX=60 StartY=-97.8453 StartZ=0 EndX=60 EndY=-127.845 EndZ=0
    g6: LineSegment StartX=60 StartY=-127.845 StartZ=0 EndX=20 EndY=-127.845 EndZ=0
    g7: LineSegment StartX=20 StartY=-127.845 StartZ=0 EndX=20 EndY=-97.8453 EndZ=0
    g8: LineSegment [constr] StartX=-20 StartY=-97.8453 StartZ=0 EndX=20 EndY=-97.8453 EndZ=0
  constraints (26):
    c: Coincident(g0,g1)
    c: Coincident(g1,g2)
    c: Coincident(g2,g3)
    c: Coincident(g3,g0)
    c: Horizontal(g0)
    c: Horizontal(g2)
    c: Vertical(g1)
    c: Vertical(g3)
    c: Coincident(g4,g5)
    c: Coincident(g5,g6)
    c: Coincident(g6,g7)
    c: Coincident(g7,g4)
    c: Horizontal(g4)
    c: Horizontal(g6)
    c: Vertical(g5)
    c: Vertical(g7)
    c: Equal(g-4,g0)
    c: Equal(g0,g4)
    c: Equal(g-3,g3)
    c: Equal(g3,g7)
    c: Coincident(g8,g0)
    c: Horizontal(g8)
    c: Coincident(g4,g8)
    c: PointOnObject(g0,g-5)
    c: PointOnObject(g4,g-7)
    c: DistanceY(g-9,g0) = 4
FEATURE [PartDesign::Pocket] Pocket003  label="LidOut_LocksLeft_Pocket"
  BaseFeature = -> Mirrored004
  Length = 5
  Length2 = 100
  Placement = pos=(-31.1547,0,47) rot=(0.707107,-0.707107,0;3.14159rad)
  Profile = -> Sketch018
  Type = 1
FEATURE [Sketcher::SketchObject] Sketch019  label="Locks_XZ_Sketch"
  ExternalGeometry = -> [Sketch,Sketch003]
  MapMode = 5
  Placement = pos=(0,0,0) rot=(1,0,0;1.5708rad)
  Support = -> [XZ_Plane026]
  sketch-geometry (57):
    g0: LineSegment StartX=60 StartY=-8e-12 StartZ=0 EndX=100 EndY=-8e-12 EndZ=0
    g1: LineSegment StartX=100 StartY=-8e-12 StartZ=0 EndX=100 EndY=-30 EndZ=0
    g2: LineSegment StartX=100 StartY=-30 StartZ=0 EndX=60 EndY=-30 EndZ=0
    g3: LineSegment StartX=60 StartY=-30 StartZ=0 EndX=60 EndY=-8e-12 EndZ=0
    g4: LineSegment StartX=-100 StartY=-8e-12 StartZ=0 EndX=-60 EndY=-8e-12 EndZ=0
    g5: LineSegment StartX=-60 StartY=-8e-12 StartZ=0 EndX=-60 EndY=-30 EndZ=0
    g6: LineSegment StartX=-60 StartY=-30 StartZ=0 EndX=-100 EndY=-30 EndZ=0
    g7: LineSegment StartX=-100 StartY=-30 StartZ=0 EndX=-100 EndY=-8e-12 EndZ=0
    g8: LineSegment StartX=-20 StartY=-8e-12 StartZ=0 EndX=20 EndY=-8e-12 EndZ=0
    g9: LineSegment StartX=20 StartY=-8e-12 StartZ=0 EndX=20 EndY=-30 EndZ=0
    g10: LineSegment StartX=20 StartY=-30 StartZ=0 EndX=-20 EndY=-30 EndZ=0
    g11: LineSegment StartX=-20 StartY=-30 StartZ=0 EndX=-20 EndY=-8e-12 EndZ=0
    g12: LineSegment [constr] StartX=-125 StartY=40 StartZ=0 EndX=-125 EndY=43 EndZ=0
    g13: LineSegment [constr] StartX=-125 StartY=43 StartZ=0 EndX=125 EndY=43 EndZ=0
    g14: LineSegment [constr] StartX=125 StartY=43 StartZ=0 EndX=125 EndY=40 EndZ=0
    g15: LineSegment StartX=-100 StartY=73 StartZ=0 EndX=-60 EndY=73 EndZ=0
    g16: LineSegment StartX=-60 StartY=73 StartZ=0 EndX=-60 EndY=43 EndZ=0
    g17: LineSegment StartX=-60 StartY=43 StartZ=0 EndX=-100 EndY=43 EndZ=0
    g18: LineSegment StartX=-100 StartY=43 StartZ=0 EndX=-100 EndY=73 EndZ=0
    g19: LineSegment StartX=-20 StartY=73 StartZ=0 EndX=20 EndY=73 EndZ=0
    g20: LineSegment StartX=20 StartY=73 StartZ=0 EndX=20 EndY=43 EndZ=0
    g21: LineSegment StartX=20 StartY=43 StartZ=0 EndX=-20 EndY=43 EndZ=0
    g22: LineSegment StartX=-20 StartY=43 StartZ=0 EndX=-20 EndY=73 EndZ=0
    g23: LineSegment StartX=60 StartY=73 StartZ=0 EndX=100 EndY=73 EndZ=0
    g24: LineSegment StartX=100 StartY=73 StartZ=0 EndX=100 EndY=43 EndZ=0
    g25: LineSegment StartX=100 StartY=43 StartZ=0 EndX=60 EndY=43 EndZ=0
    g26: LineSegment StartX=60 StartY=43 StartZ=0 EndX=60 EndY=73 EndZ=0
    g27: LineSegment [constr] StartX=-60 StartY=-30 StartZ=0 EndX=-20 EndY=-30 EndZ=0
    g28: LineSegment [constr] StartX=20 StartY=-30 StartZ=0 EndX=60 EndY=-30 EndZ=0
    g29: LineSegment [constr] StartX=125 StartY=-30 StartZ=0 EndX=145 EndY=-30 EndZ=0
    g30: LineSegment [constr] StartX=-145 StartY=-30 StartZ=0 EndX=-125 EndY=-30 EndZ=0
    g31: LineSegment StartX=-145 StartY=43 StartZ=0 EndX=-145 EndY=73 EndZ=0
    g32: LineSegment StartX=145 StartY=73 StartZ=0 EndX=145 EndY=43 EndZ=0
    g33: LineSegment StartX=145 StartY=-30 StartZ=0 EndX=145 EndY=-8e-12 EndZ=0
    g34: LineSegment StartX=-145 StartY=-30 StartZ=0 EndX=-145 EndY=-8e-12 EndZ=0
    g35: LineSegment [constr] StartX=-125 StartY=-30 StartZ=0 EndX=-100 EndY=-30 EndZ=0
    g36: LineSegment [constr] StartX=100 StartY=-30 StartZ=0 EndX=125 EndY=-30 EndZ=0
    g37: LineSegment StartX=-155 StartY=47.5 StartZ=0 EndX=-125 EndY=47.5 EndZ=0
    g38: LineSegment StartX=-125 StartY=47.5 StartZ=0 EndX=-125 EndY=27.5 EndZ=0
    g39: LineSegment StartX=-125 StartY=27.5 StartZ=0 EndX=-155 EndY=27.5 EndZ=0
    g40: LineSegment StartX=-155 StartY=27.5 StartZ=0 EndX=-155 EndY=47.5 EndZ=0
    g41: LineSegment StartX=-155 StartY=15.5 StartZ=0 EndX=-125 EndY=15.5 EndZ=0
    g42: LineSegment StartX=-125 StartY=15.5 StartZ=0 EndX=-125 EndY=-4.5 EndZ=0
    g43: LineSegment StartX=-125 StartY=-4.5 StartZ=0 EndX=-155 EndY=-4.5 EndZ=0
    g44: LineSegment StartX=-155 StartY=-4.5 StartZ=0 EndX=-155 EndY=15.5 EndZ=0
    g45: LineSegment StartX=125 StartY=47.5 StartZ=0 EndX=155 EndY=47.5 EndZ=0
    g46: LineSegment StartX=155 StartY=47.5 StartZ=0 EndX=155 EndY=27.5 EndZ=0
    g47: LineSegment StartX=155 StartY=27.5 StartZ=0 EndX=125 EndY=27.5 EndZ=0
    g48: LineSegment StartX=125 StartY=27.5 StartZ=0 EndX=125 EndY=47.5 EndZ=0
    g49: LineSegment StartX=125 StartY=15.5 StartZ=0 EndX=155 EndY=15.5 EndZ=0
    g50: LineSegment StartX=155 StartY=15.5 StartZ=0 EndX=155 EndY=-4.5 EndZ=0
    g51: LineSegment StartX=155 StartY=-4.5 StartZ=0 EndX=125 EndY=-4.5 EndZ=0
    g52: LineSegment StartX=125 StartY=-4.5 StartZ=0 EndX=125 EndY=15.5 EndZ=0
    g53: LineSegment [constr] StartX=-155 StartY=27.5 StartZ=0 EndX=-155 EndY=15.5 EndZ=0
    g54: LineSegment [constr] StartX=155 StartY=27.5 StartZ=0 EndX=155 EndY=15.5 EndZ=0
    g55: LineSegment [constr] StartX=-145 StartY=-8e-12 StartZ=0 EndX=-145 EndY=15.5 EndZ=0
    g56: LineSegment [constr] StartX=-145 StartY=43 StartZ=0 EndX=-145 EndY=27.5 EndZ=0
  constraints (169):
    c: Coincident(g0,g1)
    c: Coincident(g1,g2)
    c: Coincident(g2,g3)
    c: Coincident(g3,g0)
    c: Horizontal(g0)
    c: Horizontal(g2)
    c: Vertical(g1)
    c: Vertical(g3)
    c: PointOnObject(g0,g-3)
    c: Coincident(g4,g5)
    c: Coincident(g5,g6)
    c: Coincident(g6,g7)
    c: Coincident(g7,g4)
    c: Horizontal(g4)
    c: Horizontal(g6)
    c: Vertical(g5)
    c: Vertical(g7)
    c: PointOnObject(g4,g-3)
    c: Coincident(g8,g9)
    c: Coincident(g9,g10)
    c: Coincident(g10,g11)
    c: Coincident(g11,g8)
    c: Horizontal(g8)
    c: Horizontal(g10)
    c: Vertical(g9)
    c: Vertical(g11)
    c: Equal(g3,g11)
    c: Equal(g11,g7)
    c: DistanceY(g7,g7) = 30
    c: Vertical(g12)
    c: Coincident(g12,g-4)
    c: Horizontal(g13)
    c: Vertical(g14)
    c: Coincident(g13,g14)
    c: Coincident(g14,g-4)
    c: Coincident(g12,g13)
    c: DistanceY(g12,g12) = 3
    c: Coincident(g15,g16)
    c: Coincident(g16,g17)
    c: Coincident(g17,g18)
    c: Coincident(g18,g15)
    c: Horizontal(g15)
    c: Horizontal(g17)
    c: Vertical(g16)
    c: Vertical(g18)
    c: PointOnObject(g16,g13)
    c: Coincident(g19,g20)
    c: Coincident(g20,g21)
    c: Coincident(g21,g22)
    c: Coincident(g22,g19)
    c: Horizontal(g19)
    c: Horizontal(g21)
    c: Vertical(g20)
    c: Vertical(g22)
    c: PointOnObject(g20,g13)
    c: Coincident(g23,g24)
    c: Coincident(g24,g25)
    c: Coincident(g25,g26)
    c: Coincident(g26,g23)
    c: Horizontal(g23)
    c: Horizontal(g25)
    c: Vertical(g24)
    c: Vertical(g26)
    c: PointOnObject(g24,g13)
    c: Equal(g18,g22)
    c: Equal(g22,g26)
    c: Equal(g26,g7)
    c: PointOnObject(g17,g7)
    c: PointOnObject(g16,g5)
    c: PointOnObject(g21,g11)
    c: PointOnObject(g20,g9)
    c: PointOnObject(g25,g3)
    c: PointOnObject(g24,g1)
    c: Horizontal(g27)
    c: Horizontal(g28)
    c: Horizontal(g29)
    c: Horizontal(g30)
    c: Coincident(g5,g27)
    c: Coincident(g10,g27)
    c: Coincident(g9,g28)
    c: Coincident(g2,g28)
    c: Equal(g6,g27)
    c: Equal(g27,g10)
    c: Equal(g10,g28)
    c: Equal(g28,g2)
    c: Equal(g30,g29)
    c: DistanceX(g6,g6) = 40
    c: Vertical(g31)
    c: PointOnObject(g32,g13)
    c: Equal(g32,g33)
    c: Equal(g33,g34)
    c: Equal(g34,g31)
    c: Equal(g31,g7)
    c: Vertical(g32)
    c: PointOnObject(g31,g13)
    c: Coincident(g35,g6)
    c: Horizontal(g35)
    c: Horizontal(g36)
    c: Coincident(g29,g36)
    c: Coincident(g1,g36)
    c: Equal(g36,g35)
    c: Coincident(g30,g35)
    c: DistanceX(g30,g30) = 20
    c: PointOnObject(g29,g-6)
    c: PointOnObject(g30,g-5)
    c: Coincident(g29,g33)
    c: Coincident(g30,g34)
    c: Vertical(g34)
    c: PointOnObject(g34,g31)
    c: Vertical(g33)
    c: PointOnObject(g33,g32)
    c: Coincident(g37,g38)
    c: Coincident(g38,g39)
    c: Coincident(g39,g40)
    c: Coincident(g40,g37)
    c: Horizontal(g37)
    c: Horizontal(g39)
    c: Vertical(g38)
    c: Vertical(g40)
    c: Coincident(g41,g42)
    c: Coincident(g42,g43)
    c: Coincident(g43,g44)
    c: Coincident(g44,g41)
    c: Horizontal(g41)
    c: Horizontal(g43)
    c: Vertical(g42)
    c: Vertical(g44)
    c: PointOnObject(g38,g-5)
    c: PointOnObject(g41,g-5)
    c: Coincident(g45,g46)
    c: Coincident(g46,g47)
    c: Coincident(g47,g48)
    c: Coincident(g48,g45)
    c: Horizontal(g45)
    c: Horizontal(g47)
    c: Vertical(g46)
    c: Vertical(g48)
    c: PointOnObject(g45,g-6)
    c: Coincident(g49,g50)
    c: Coincident(g50,g51)
    c: Coincident(g51,g52)
    c: Coincident(g52,g49)
    c: Horizontal(g49)
    c: Horizontal(g51)
    c: Vertical(g50)
    c: Vertical(g52)
    c: PointOnObject(g49,g-6)
    c: Equal(g49,g45)
    c: Equal(g45,g37)
    c: Equal(g37,g41)
    c: Equal(g41,g7)
    c: Equal(g50,g46)
    c: Equal(g46,g44)
    c: Equal(g44,g40)
    c: Coincident(g53,g39)
    c: Coincident(g53,g41)
    c: Coincident(g54,g46)
    c: Coincident(g54,g49)
    c: Equal(g54,g53)
    c: DistanceY(g53,g53) = 12
    c: DistanceY(g44,g44) = 20
    c: Coincident(g55,g34)
    c: PointOnObject(g55,g41)
    c: Vertical(g55)
    c: Coincident(g56,g31)
    c: PointOnObject(g56,g39)
    c: Vertical(g56)
    c: Equal(g56,g55)
    c: PointOnObject(g47,g39)
FEATURE [Sketcher::SketchObject] Sketch020  label="Locks_YZ_Sketch"
  ExternalGeometry = -> [Sketch004,Sketch019]
  MapMode = 5
  Placement = pos=(0,0,0) rot=(0.57735,0.57735,0.57735;2.0944rad)
  Support = -> [YZ_Plane026]
  sketch-geometry (37):
    g0: LineSegment [constr] StartX=-75 StartY=43 StartZ=0 EndX=75 EndY=43 EndZ=0
    g1: LineSegment [constr] StartX=75 StartY=43 StartZ=0 EndX=75 EndY=40 EndZ=0
    g2: LineSegment [constr] StartX=-75 StartY=43 StartZ=0 EndX=-75 EndY=40 EndZ=0
    g3: LineSegment [constr] StartX=-75 StartY=0 StartZ=0 EndX=75 EndY=0 EndZ=0
    g4: LineSegment [constr] StartX=-75 StartY=-30 StartZ=0 EndX=-60 EndY=-30 EndZ=0
    g5: LineSegment [constr] StartX=-20 StartY=-30 StartZ=0 EndX=20 EndY=-30 EndZ=0
    g6: LineSegment [constr] StartX=60 StartY=-30 StartZ=0 EndX=75 EndY=-30 EndZ=0
    g7: LineSegment StartX=-60 StartY=0 StartZ=0 EndX=-20 EndY=0 EndZ=0
    g8: LineSegment StartX=-20 StartY=0 StartZ=0 EndX=-20 EndY=-30 EndZ=0
    g9: LineSegment StartX=-20 StartY=-30 StartZ=0 EndX=-60 EndY=-30 EndZ=0
    g10: LineSegment StartX=-60 StartY=-30 StartZ=0 EndX=-60 EndY=0 EndZ=0
    g11: LineSegment StartX=20 StartY=0 StartZ=0 EndX=60 EndY=0 EndZ=0
    g12: LineSegment StartX=60 StartY=0 StartZ=0 EndX=60 EndY=-30 EndZ=0
    g13: LineSegment StartX=60 StartY=-30 StartZ=0 EndX=20 EndY=-30 EndZ=0
    g14: LineSegment StartX=20 StartY=-30 StartZ=0 EndX=20 EndY=0 EndZ=0
    g15: LineSegment StartX=-60 StartY=73 StartZ=0 EndX=-20 EndY=73 EndZ=0
    g16: LineSegment StartX=-20 StartY=73 StartZ=0 EndX=-20 EndY=43 EndZ=0
    g17: LineSegment StartX=-20 StartY=43 StartZ=0 EndX=-60 EndY=43 EndZ=0
    g18: LineSegment StartX=-60 StartY=43 StartZ=0 EndX=-60 EndY=73 EndZ=0
    g19: LineSegment StartX=20 StartY=73 StartZ=0 EndX=60 EndY=73 EndZ=0
    g20: LineSegment StartX=60 StartY=73 StartZ=0 EndX=60 EndY=43 EndZ=0
    g21: LineSegment StartX=60 StartY=43 StartZ=0 EndX=20 EndY=43 EndZ=0
    g22: LineSegment StartX=20 StartY=43 StartZ=0 EndX=20 EndY=73 EndZ=0
    g23: LineSegment [constr] StartX=75 StartY=-30 StartZ=0 EndX=100 EndY=-30 EndZ=0
    g24: LineSegment [constr] StartX=-75 StartY=-30 StartZ=0 EndX=-100 EndY=-30 EndZ=0
    g25: LineSegment StartX=-100 StartY=-30 StartZ=0 EndX=-100 EndY=0 EndZ=0
    g26: LineSegment StartX=100 StartY=-30 StartZ=0 EndX=100 EndY=0 EndZ=0
    g27: LineSegment StartX=-100 StartY=43 StartZ=0 EndX=-100 EndY=73 EndZ=0
    g28: LineSegment StartX=100 StartY=43 StartZ=0 EndX=100 EndY=73 EndZ=0
    g29: LineSegment StartX=-115 StartY=27.5 StartZ=0 EndX=-75 EndY=27.5 EndZ=0
    g30: LineSegment StartX=-75 StartY=27.5 StartZ=0 EndX=-75 EndY=15.5 EndZ=0
    g31: LineSegment StartX=-75 StartY=15.5 StartZ=0 EndX=-115 EndY=15.5 EndZ=0
    g32: LineSegment StartX=-115 StartY=15.5 StartZ=0 EndX=-115 EndY=27.5 EndZ=0
    g33: LineSegment StartX=75 StartY=27.5 StartZ=0 EndX=115 EndY=27.5 EndZ=0
    g34: LineSegment StartX=115 StartY=27.5 StartZ=0 EndX=115 EndY=15.5 EndZ=0
    g35: LineSegment StartX=115 StartY=15.5 StartZ=0 EndX=75 EndY=15.5 EndZ=0
    g36: LineSegment StartX=75 StartY=15.5 StartZ=0 EndX=75 EndY=27.5 EndZ=0
  constraints (110):
    c: Horizontal(g0)
    c: Coincident(g1,g0)
    c: Coincident(g0,g2)
    c: Vertical(g2)
    c: Vertical(g1)
    c: DistanceY(g2,g2) = 3
    c: Horizontal(g4)
    c: Horizontal(g5)
    c: Horizontal(g6)
    c: Equal(g6,g4)
    c: Coincident(g7,g8)
    c: Coincident(g8,g9)
    c: Coincident(g9,g10)
    c: Coincident(g10,g7)
    c: Horizontal(g7)
    c: Horizontal(g9)
    c: Vertical(g8)
    c: Vertical(g10)
    c: PointOnObject(g7,g3)
    c: Coincident(g8,g5)
    c: Coincident(g11,g12)
    c: Coincident(g12,g13)
    c: Coincident(g13,g14)
    c: Coincident(g14,g11)
    c: Horizontal(g11)
    c: Horizontal(g13)
    c: Vertical(g12)
    c: Vertical(g14)
    c: PointOnObject(g11,g3)
    c: Coincident(g12,g6)
    c: Coincident(g5,g13)
    c: Coincident(g4,g9)
    c: Equal(g13,g5)
    c: Equal(g5,g9)
    c: DistanceY(g10,g10) = 30
    c: DistanceX(g9,g9) = 40
    c: Coincident(g15,g16)
    c: Coincident(g16,g17)
    c: Coincident(g17,g18)
    c: Coincident(g18,g15)
    c: Horizontal(g15)
    c: Horizontal(g17)
    c: Vertical(g16)
    c: Vertical(g18)
    c: Coincident(g19,g20)
    c: Coincident(g20,g21)
    c: Coincident(g21,g22)
    c: Coincident(g22,g19)
    c: Horizontal(g19)
    c: Horizontal(g21)
    c: Vertical(g20)
    c: Vertical(g22)
    c: PointOnObject(g20,g0)
    c: Equal(g22,g18)
    c: Equal(g18,g10)
    c: PointOnObject(g17,g10)
    c: Equal(g17,g9)
    c: Equal(g9,g21)
    c: PointOnObject(g21,g14)
    c: PointOnObject(g16,g0)
    c: Coincident(g3,g-5)
    c: Coincident(g3,g-4)
    c: PointOnObject(g6,g-4)
    c: PointOnObject(g4,g-5)
    c: Coincident(g2,g-5)
    c: Coincident(g1,g-4)
    c: Coincident(g23,g6)
    c: Horizontal(g23)
    c: Coincident(g24,g4)
    c: Horizontal(g24)
    c: Equal(g24,g23)
    c: DistanceX(g24,g24) = 25
    c: Coincident(g25,g24)
    c: Vertical(g25)
    c: Coincident(g26,g23)
    c: Vertical(g26)
    c: Equal(g26,g25)
    c: Equal(g25,g10)
    c: Vertical(g27)
    c: Vertical(g28)
    c: Equal(g27,g10)
    c: PointOnObject(g27,g0)
    c: PointOnObject(g28,g0)
    c: PointOnObject(g26,g28)
    c: PointOnObject(g25,g27)
    c: Equal(g28,g10)
    c: Coincident(g29,g30)
    c: Coincident(g30,g31)
    c: Coincident(g31,g32)
    c: Coincident(g32,g29)
    c: Horizontal(g29)
    c: Horizontal(g31)
    c: Vertical(g30)
    c: Vertical(g32)
    c: Coincident(g33,g34)
    c: Coincident(g34,g35)
    c: Coincident(g35,g36)
    c: Coincident(g36,g33)
    c: Horizontal(g33)
    c: Horizontal(g35)
    c: Vertical(g34)
    c: Vertical(g36)
    c: PointOnObject(g33,g-4)
    c: PointOnObject(g29,g-5)
    c: PointOnObject(g-6,g29)
    c: PointOnObject(g-6,g33)
    c: PointOnObject(g-7,g35)
    c: PointOnObject(g-7,g31)
    c: Equal(g29,g33)
    c: Equal(g33,g9)
FEATURE [PartDesign::ShapeBinder] ShapeBinder026
  Placement = pos=(0,0,0) rot=(1,0,0;1.5708rad)
  Support = -> [Sketch019]
FEATURE [Sketcher::SketchObject] Sketch021  label="BottomOut_Locks_Sketch"
  ExternalGeometry = -> [ShapeBinder026]
  MapMode = 5
  Placement = pos=(0,-83,-4) rot=(0,-0.707107,0.707107;3.14159rad)
  Support = -> [Pad008]
  sketch-geometry (48):
    g0: LineSegment StartX=-60 StartY=26 StartZ=0 EndX=-20 EndY=26 EndZ=0
    g1: LineSegment StartX=-20 StartY=26 StartZ=0 EndX=-20 EndY=-4 EndZ=0
    g2: LineSegment StartX=-20 StartY=-4 StartZ=0 EndX=-60 EndY=-4 EndZ=0
    g3: LineSegment StartX=-60 StartY=-4 StartZ=0 EndX=-60 EndY=26 EndZ=0
    g4: LineSegment StartX=20 StartY=26 StartZ=0 EndX=60 EndY=26 EndZ=0
    g5: LineSegment StartX=60 StartY=26 StartZ=0 EndX=60 EndY=-4 EndZ=0
    g6: LineSegment StartX=60 StartY=-4 StartZ=0 EndX=20 EndY=-4 EndZ=0
    g7: LineSegment StartX=20 StartY=-4 StartZ=0 EndX=20 EndY=26 EndZ=0
    g8: LineSegment StartX=100 StartY=26 StartZ=0 EndX=145 EndY=26 EndZ=0
    g9: LineSegment StartX=145 StartY=26 StartZ=0 EndX=145 EndY=0.5 EndZ=0
    g10: LineSegment StartX=125 StartY=-4 StartZ=0 EndX=100 EndY=-4 EndZ=0
    g11: LineSegment StartX=100 StartY=-4 StartZ=0 EndX=100 EndY=26 EndZ=0
    g12: LineSegment StartX=-145 StartY=26 StartZ=0 EndX=-100 EndY=26 EndZ=0
    g13: LineSegment StartX=-100 StartY=26 StartZ=0 EndX=-100 EndY=-4 EndZ=0
    g14: LineSegment StartX=-100 StartY=-4 StartZ=0 EndX=-125 EndY=-4 EndZ=0
    g15: LineSegment StartX=-145 StartY=0.5 StartZ=0 EndX=-145 EndY=26 EndZ=0
    g16: LineSegment StartX=-125 StartY=-47 StartZ=0 EndX=-100 EndY=-47 EndZ=0
    g17: LineSegment StartX=-100 StartY=-47 StartZ=0 EndX=-100 EndY=-77 EndZ=0
    g18: LineSegment StartX=-100 StartY=-77 StartZ=0 EndX=-145 EndY=-77 EndZ=0
    g19: LineSegment StartX=-145 StartY=-77 StartZ=0 EndX=-145 EndY=-51.5 EndZ=0
    g20: LineSegment StartX=-60 StartY=-47 StartZ=0 EndX=-20 EndY=-47 EndZ=0
    g21: LineSegment StartX=-20 StartY=-47 StartZ=0 EndX=-20 EndY=-77 EndZ=0
    g22: LineSegment StartX=-20 StartY=-77 StartZ=0 EndX=-60 EndY=-77 EndZ=0
    g23: LineSegment StartX=-60 StartY=-77 StartZ=0 EndX=-60 EndY=-47 EndZ=0
    g24: LineSegment StartX=20 StartY=-47 StartZ=0 EndX=60 EndY=-47 EndZ=0
    g25: LineSegment StartX=60 StartY=-47 StartZ=0 EndX=60 EndY=-77 EndZ=0
    g26: LineSegment StartX=60 StartY=-77 StartZ=0 EndX=20 EndY=-77 EndZ=0
    g27: LineSegment StartX=20 StartY=-77 StartZ=0 EndX=20 EndY=-47 EndZ=0
    g28: LineSegment StartX=100 StartY=-47 StartZ=0 EndX=125 EndY=-47 EndZ=0
    g29: LineSegment StartX=145 StartY=-51.5 StartZ=0 EndX=145 EndY=-77 EndZ=0
    g30: LineSegment StartX=145 StartY=-77 StartZ=0 EndX=100 EndY=-77 EndZ=0
    g31: LineSegment StartX=100 StartY=-77 StartZ=0 EndX=100 EndY=-47 EndZ=0
    g32: LineSegment StartX=-155 StartY=0.5 StartZ=0 EndX=-145 EndY=0.5 EndZ=0
    g33: LineSegment StartX=-125 StartY=-4 StartZ=0 EndX=-125 EndY=-19.5 EndZ=0
    g34: LineSegment StartX=-125 StartY=-19.5 StartZ=0 EndX=-155 EndY=-19.5 EndZ=0
    g35: LineSegment StartX=-155 StartY=-19.5 StartZ=0 EndX=-155 EndY=0.5 EndZ=0
    g36: LineSegment StartX=-155 StartY=-31.5 StartZ=0 EndX=-125 EndY=-31.5 EndZ=0
    g37: LineSegment StartX=-125 StartY=-31.5 StartZ=0 EndX=-125 EndY=-47 EndZ=0
    g38: LineSegment StartX=-145 StartY=-51.5 StartZ=0 EndX=-155 EndY=-51.5 EndZ=0
    g39: LineSegment StartX=-155 StartY=-51.5 StartZ=0 EndX=-155 EndY=-31.5 EndZ=0
    g40: LineSegment StartX=145 StartY=0.5 StartZ=0 EndX=155 EndY=0.5 EndZ=0
    g41: LineSegment StartX=155 StartY=0.5 StartZ=0 EndX=155 EndY=-19.5 EndZ=0
    g42: LineSegment StartX=155 StartY=-19.5 StartZ=0 EndX=125 EndY=-19.5 EndZ=0
    g43: LineSegment StartX=125 StartY=-19.5 StartZ=0 EndX=125 EndY=-4 EndZ=0
    g44: LineSegment StartX=125 StartY=-31.5 StartZ=0 EndX=155 EndY=-31.5 EndZ=0
    g45: LineSegment StartX=155 StartY=-31.5 StartZ=0 EndX=155 EndY=-51.5 EndZ=0
    g46: LineSegment StartX=155 StartY=-51.5 StartZ=0 EndX=145 EndY=-51.5 EndZ=0
    g47: LineSegment StartX=125 StartY=-47 StartZ=0 EndX=125 EndY=-31.5 EndZ=0
  constraints (116):
    c: Coincident(g0,g1)
    c: Coincident(g1,g2)
    c: Coincident(g2,g3)
    c: Coincident(g3,g0)
    c: Horizontal(g0)
    c: Horizontal(g2)
    c: Vertical(g1)
    c: Vertical(g3)
    c: Coincident(g1,g-5)
    c: Coincident(g4,g5)
    c: Coincident(g5,g6)
    c: Coincident(g6,g7)
    c: Coincident(g7,g4)
    c: Horizontal(g4)
    c: Horizontal(g6)
    c: Vertical(g5)
    c: Vertical(g7)
    c: Coincident(g5,g-7)
    c: Coincident(g8,g9)
    c: Coincident(g10,g11)
    c: Coincident(g11,g8)
    c: Horizontal(g8)
    c: Horizontal(g10)
    c: Vertical(g9)
    c: Vertical(g11)
    c: Coincident(g12,g13)
    c: Coincident(g13,g14)
    c: Coincident(g15,g12)
    c: Horizontal(g12)
    c: Horizontal(g14)
    c: Vertical(g13)
    c: Vertical(g15)
    c: Coincident(g13,g-3)
    c: Coincident(g16,g17)
    c: Coincident(g17,g18)
    c: Coincident(g18,g19)
    c: Horizontal(g16)
    c: Horizontal(g18)
    c: Vertical(g17)
    c: Vertical(g19)
    c: Coincident(g17,g-14)
    c: Coincident(g20,g21)
    c: Coincident(g21,g22)
    c: Coincident(g22,g23)
    c: Coincident(g23,g20)
    c: Horizontal(g20)
    c: Horizontal(g22)
    c: Vertical(g21)
    c: Vertical(g23)
    c: Coincident(g20,g-13)
    c: Coincident(g21,g-12)
    c: Coincident(g24,g25)
    c: Coincident(g25,g26)
    c: Coincident(g26,g27)
    c: Coincident(g27,g24)
    c: Horizontal(g24)
    c: Horizontal(g26)
    c: Vertical(g25)
    c: Vertical(g27)
    c: Coincident(g25,g-10)
    c: Coincident(g29,g30)
    c: Coincident(g30,g31)
    c: Coincident(g31,g28)
    c: Horizontal(g28)
    c: Horizontal(g30)
    c: Vertical(g29)
    c: Vertical(g31)
    c: Coincident(g28,g-9)
    c: Coincident(g0,g-4)
    c: Coincident(g4,g-6)
    c: Coincident(g8,g-8)
    c: Coincident(g24,g-11)
    c: Coincident(g29,g-17)
    c: Coincident(g12,g-15)
    c: Coincident(g33,g34)
    c: Coincident(g34,g35)
    c: Coincident(g35,g32)
    c: Horizontal(g32)
    c: Horizontal(g34)
    c: Vertical(g33)
    c: Vertical(g35)
    c: Coincident(g32,g-20)
    c: Coincident(g33,g-19)
    c: Coincident(g36,g37)
    c: Coincident(g38,g39)
    c: Coincident(g39,g36)
    c: Horizontal(g36)
    c: Horizontal(g38)
    c: Vertical(g37)
    c: Vertical(g39)
    c: Coincident(g36,g-21)
    c: Coincident(g40,g41)
    c: Coincident(g41,g42)
    c: Coincident(g42,g43)
    c: Horizontal(g40)
    c: Horizontal(g42)
    c: Vertical(g41)
    c: Vertical(g43)
    c: Coincident(g41,g-24)
    c: Coincident(g44,g45)
    c: Coincident(g45,g46)
    c: Coincident(g47,g44)
    c: Horizontal(g44)
    c: Horizontal(g46)
    c: Vertical(g45)
    c: Vertical(g47)
    c: Coincident(g44,g-25)
    c: Coincident(g45,g-26)
    c: Coincident(g15,g32)
    c: Coincident(g33,g14)
    c: Coincident(g38,g19)
    c: Coincident(g37,g16)
    c: Coincident(g10,g43)
    c: Coincident(g9,g40)
    c: Coincident(g29,g46)
    c: Coincident(g47,g28)
FEATURE [PartDesign::Pocket] Pocket004  label="BottomOut_Locks_Pocket"
  BaseFeature = -> Pad008
  Length = 5
  Length2 = 100
  Placement = pos=(0,-83,-4) rot=(0,0.707107,0.707107;3.14159rad)
  Profile = -> Sketch021
  Type = 1
FEATURE [PartDesign::ShapeBinder] ShapeBinder027
  Placement = pos=(0,0,0) rot=(1,0,0;1.5708rad)
  Support = -> [Sketch019]
FEATURE [Sketcher::SketchObject] Sketch022  label="BottomIn_Locks_Sketch"
  ExternalGeometry = -> [ShapeBinder027]
  MapMode = 5
  Placement = pos=(0,-79,-4) rot=(0,-0.707107,0.707107;3.14159rad)
  Support = -> [Pad009]
  sketch-geometry (32):
    g0: LineSegment StartX=-145 StartY=26 StartZ=0 EndX=-100 EndY=26 EndZ=0
    g1: LineSegment StartX=-100 StartY=26 StartZ=0 EndX=-100 EndY=-4 EndZ=0
    g2: LineSegment StartX=-100 StartY=-4 StartZ=0 EndX=-125 EndY=-4 EndZ=0
    g3: LineSegment StartX=-145 StartY=0.5 StartZ=0 EndX=-145 EndY=26 EndZ=0
    g4: LineSegment StartX=-60 StartY=26 StartZ=0 EndX=-20 EndY=26 EndZ=0
    g5: LineSegment StartX=-20 StartY=26 StartZ=0 EndX=-20 EndY=-4 EndZ=0
    g6: LineSegment StartX=-20 StartY=-4 StartZ=0 EndX=-60 EndY=-4 EndZ=0
    g7: LineSegment StartX=-60 StartY=-4 StartZ=0 EndX=-60 EndY=26 EndZ=0
    g8: LineSegment StartX=20 StartY=26 StartZ=0 EndX=60 EndY=26 EndZ=0
    g9: LineSegment StartX=60 StartY=26 StartZ=0 EndX=60 EndY=-4 EndZ=0
    g10: LineSegment StartX=60 StartY=-4 StartZ=0 EndX=20 EndY=-4 EndZ=0
    g11: LineSegment StartX=20 StartY=-4 StartZ=0 EndX=20 EndY=26 EndZ=0
    g12: LineSegment StartX=100 StartY=26 StartZ=0 EndX=145 EndY=26 EndZ=0
    g13: LineSegment StartX=145 StartY=26 StartZ=0 EndX=145 EndY=0.5 EndZ=0
    g14: LineSegment StartX=125 StartY=-4 StartZ=0 EndX=100 EndY=-4 EndZ=0
    g15: LineSegment StartX=100 StartY=-4 StartZ=0 EndX=100 EndY=26 EndZ=0
    g16: LineSegment StartX=-155 StartY=0.5 StartZ=0 EndX=-145 EndY=0.5 EndZ=0
    g17: LineSegment StartX=-125 StartY=-4 StartZ=0 EndX=-125 EndY=-19.5 EndZ=0
    g18: LineSegment StartX=-125 StartY=-19.5 StartZ=0 EndX=-155 EndY=-19.5 EndZ=0
    g19: LineSegment StartX=-155 StartY=-19.5 StartZ=0 EndX=-155 EndY=0.5 EndZ=0
    g20: LineSegment StartX=125 StartY=-19.5 StartZ=0 EndX=155 EndY=-19.5 EndZ=0
    g21: LineSegment StartX=155 StartY=-19.5 StartZ=0 EndX=155 EndY=0.5 EndZ=0
    g22: LineSegment StartX=155 StartY=0.5 StartZ=0 EndX=145 EndY=0.5 EndZ=0
    g23: LineSegment StartX=125 StartY=-4 StartZ=0 EndX=125 EndY=-19.5 EndZ=0
    g24: LineSegment StartX=-155 StartY=-31.5 StartZ=0 EndX=-125 EndY=-31.5 EndZ=0
    g25: LineSegment StartX=-125 StartY=-31.5 StartZ=0 EndX=-125 EndY=-51.5 EndZ=0
    g26: LineSegment StartX=-125 StartY=-51.5 StartZ=0 EndX=-155 EndY=-51.5 EndZ=0
    g27: LineSegment StartX=-155 StartY=-51.5 StartZ=0 EndX=-155 EndY=-31.5 EndZ=0
    g28: LineSegment StartX=125 StartY=-51.5 StartZ=0 EndX=155 EndY=-51.5 EndZ=0
    g29: LineSegment StartX=155 StartY=-51.5 StartZ=0 EndX=155 EndY=-31.5 EndZ=0
    g30: LineSegment StartX=155 StartY=-31.5 StartZ=0 EndX=125 EndY=-31.5 EndZ=0
    g31: LineSegment StartX=125 StartY=-31.5 StartZ=0 EndX=125 EndY=-51.5 EndZ=0
  constraints (81):
    c: Coincident(g0,g1)
    c: Coincident(g1,g2)
    c: Coincident(g3,g0)
    c: Horizontal(g0)
    c: Horizontal(g2)
    c: Vertical(g1)
    c: Vertical(g3)
    c: Coincident(g0,g-3)
    c: Coincident(g4,g5)
    c: Coincident(g5,g6)
    c: Coincident(g6,g7)
    c: Coincident(g7,g4)
    c: Horizontal(g4)
    c: Horizontal(g6)
    c: Vertical(g5)
    c: Vertical(g7)
    c: Coincident(g8,g9)
    c: Coincident(g9,g10)
    c: Coincident(g10,g11)
    c: Coincident(g11,g8)
    c: Horizontal(g8)
    c: Horizontal(g10)
    c: Vertical(g9)
    c: Vertical(g11)
    c: Coincident(g12,g13)
    c: Coincident(g14,g15)
    c: Coincident(g15,g12)
    c: Horizontal(g12)
    c: Horizontal(g14)
    c: Vertical(g13)
    c: Vertical(g15)
    c: Coincident(g12,g-9)
    c: Coincident(g8,g-7)
    c: Coincident(g9,g-8)
    c: Coincident(g4,g-5)
    c: Coincident(g5,g-6)
    c: Coincident(g1,g-4)
    c: Coincident(g17,g18)
    c: Coincident(g18,g19)
    c: Coincident(g19,g16)
    c: Horizontal(g16)
    c: Horizontal(g18)
    c: Vertical(g17)
    c: Vertical(g19)
    c: Coincident(g16,g-11)
    c: Coincident(g17,g-12)
    c: Coincident(g2,g17)
    c: Coincident(g3,g16)
    c: Coincident(g20,g21)
    c: Coincident(g21,g22)
    c: Coincident(g23,g20)
    c: Horizontal(g20)
    c: Horizontal(g22)
    c: Vertical(g21)
    c: Vertical(g23)
    c: Coincident(g20,g-14)
    c: Coincident(g21,g-13)
    c: Coincident(g14,g23)
    c: Coincident(g13,g22)
    c: PointOnObject(g13,g-10)
    c: Coincident(g14,g-9)
    c: Coincident(g24,g25)
    c: Coincident(g25,g26)
    c: Coincident(g26,g27)
    c: Coincident(g27,g24)
    c: Horizontal(g24)
    c: Horizontal(g26)
    c: Vertical(g25)
    c: Vertical(g27)
    c: Coincident(g24,g-15)
    c: Coincident(g28,g29)
    c: Coincident(g29,g30)
    c: Coincident(g30,g31)
    c: Coincident(g31,g28)
    c: Horizontal(g28)
    c: Horizontal(g30)
    c: Vertical(g29)
    c: Vertical(g31)
    c: Coincident(g29,g-17)
    c: Coincident(g25,g-16)
    c: Coincident(g28,g-18)
FEATURE [PartDesign::Pocket] Pocket005  label="BottomIn_Locks_Pocket"
  BaseFeature = -> Pad009
  Length = 5
  Length2 = 100
  Placement = pos=(0,-79,-4) rot=(0,0.707107,0.707107;3.14159rad)
  Profile = -> Sketch022
  Type = 1
FEATURE [PartDesign::ShapeBinder] ShapeBinder028
  Placement = pos=(0,0,0) rot=(1,0,0;1.5708rad)
  Support = -> [Sketch019]
FEATURE [Sketcher::SketchObject] Sketch023  label="TopOut_Locks_Sketch"
  ExternalGeometry = -> [ShapeBinder028]
  MapMode = 5
  Placement = pos=(0,83,0) rot=(-1,0,0;1.5708rad)
  Support = -> [Pad002]
  sketch-geometry (48):
    g0: LineSegment StartX=-145 StartY=30 StartZ=0 EndX=-100 EndY=30 EndZ=0
    g1: LineSegment StartX=-100 StartY=30 StartZ=0 EndX=-100 EndY=8e-12 EndZ=0
    g2: LineSegment StartX=-100 StartY=8e-12 StartZ=0 EndX=-125 EndY=8e-12 EndZ=0
    g3: LineSegment StartX=-145 StartY=4.5 StartZ=0 EndX=-145 EndY=30 EndZ=0
    g4: LineSegment StartX=-60 StartY=30 StartZ=0 EndX=-20 EndY=30 EndZ=0
    g5: LineSegment StartX=-20 StartY=30 StartZ=0 EndX=-20 EndY=8e-12 EndZ=0
    g6: LineSegment StartX=-20 StartY=8e-12 StartZ=0 EndX=-60 EndY=8e-12 EndZ=0
    g7: LineSegment StartX=-60 StartY=8e-12 StartZ=0 EndX=-60 EndY=30 EndZ=0
    g8: LineSegment StartX=20 StartY=30 StartZ=0 EndX=60 EndY=30 EndZ=0
    g9: LineSegment StartX=60 StartY=30 StartZ=0 EndX=60 EndY=8e-12 EndZ=0
    g10: LineSegment StartX=60 StartY=8e-12 StartZ=0 EndX=20 EndY=8e-12 EndZ=0
    g11: LineSegment StartX=20 StartY=8e-12 StartZ=0 EndX=20 EndY=30 EndZ=0
    g12: LineSegment StartX=100 StartY=30 StartZ=0 EndX=145 EndY=30 EndZ=0
    g13: LineSegment StartX=145 StartY=30 StartZ=0 EndX=145 EndY=4.5 EndZ=0
    g14: LineSegment StartX=125 StartY=8e-12 StartZ=0 EndX=100 EndY=8e-12 EndZ=0
    g15: LineSegment StartX=100 StartY=8e-12 StartZ=0 EndX=100 EndY=30 EndZ=0
    g16: LineSegment StartX=-125 StartY=-43 StartZ=0 EndX=-100 EndY=-43 EndZ=0
    g17: LineSegment StartX=-100 StartY=-43 StartZ=0 EndX=-100 EndY=-73 EndZ=0
    g18: LineSegment StartX=-100 StartY=-73 StartZ=0 EndX=-145 EndY=-73 EndZ=0
    g19: LineSegment StartX=-145 StartY=-73 StartZ=0 EndX=-145 EndY=-47.5 EndZ=0
    g20: LineSegment StartX=-60 StartY=-43 StartZ=0 EndX=-20 EndY=-43 EndZ=0
    g21: LineSegment StartX=-20 StartY=-43 StartZ=0 EndX=-20 EndY=-73 EndZ=0
    g22: LineSegment StartX=-20 StartY=-73 StartZ=0 EndX=-60 EndY=-73 EndZ=0
    g23: LineSegment StartX=-60 StartY=-73 StartZ=0 EndX=-60 EndY=-43 EndZ=0
    g24: LineSegment StartX=20 StartY=-43 StartZ=0 EndX=60 EndY=-43 EndZ=0
    g25: LineSegment StartX=60 StartY=-43 StartZ=0 EndX=60 EndY=-73 EndZ=0
    g26: LineSegment StartX=60 StartY=-73 StartZ=0 EndX=20 EndY=-73 EndZ=0
    g27: LineSegment StartX=20 StartY=-73 StartZ=0 EndX=20 EndY=-43 EndZ=0
    g28: LineSegment StartX=100 StartY=-43 StartZ=0 EndX=125 EndY=-43 EndZ=0
    g29: LineSegment StartX=145 StartY=-47.5 StartZ=0 EndX=145 EndY=-73 EndZ=0
    g30: LineSegment StartX=145 StartY=-73 StartZ=0 EndX=100 EndY=-73 EndZ=0
    g31: LineSegment StartX=100 StartY=-73 StartZ=0 EndX=100 EndY=-43 EndZ=0
    g32: LineSegment StartX=-155 StartY=4.5 StartZ=0 EndX=-145 EndY=4.5 EndZ=0
    g33: LineSegment StartX=-125 StartY=8e-12 StartZ=0 EndX=-125 EndY=-15.5 EndZ=0
    g34: LineSegment StartX=-125 StartY=-15.5 StartZ=0 EndX=-155 EndY=-15.5 EndZ=0
    g35: LineSegment StartX=-155 StartY=-15.5 StartZ=0 EndX=-155 EndY=4.5 EndZ=0
    g36: LineSegment StartX=-155 StartY=-27.5 StartZ=0 EndX=-125 EndY=-27.5 EndZ=0
    g37: LineSegment StartX=-125 StartY=-27.5 StartZ=0 EndX=-125 EndY=-43 EndZ=0
    g38: LineSegment StartX=-145 StartY=-47.5 StartZ=0 EndX=-155 EndY=-47.5 EndZ=0
    g39: LineSegment StartX=-155 StartY=-47.5 StartZ=0 EndX=-155 EndY=-27.5 EndZ=0
    g40: LineSegment StartX=145 StartY=4.5 StartZ=0 EndX=155 EndY=4.5 EndZ=0
    g41: LineSegment StartX=155 StartY=4.5 StartZ=0 EndX=155 EndY=-15.5 EndZ=0
    g42: LineSegment StartX=155 StartY=-15.5 StartZ=0 EndX=125 EndY=-15.5 EndZ=0
    g43: LineSegment StartX=125 StartY=-15.5 StartZ=0 EndX=125 EndY=8e-12 EndZ=0
    g44: LineSegment StartX=125 StartY=-27.5 StartZ=0 EndX=155 EndY=-27.5 EndZ=0
    g45: LineSegment StartX=155 StartY=-27.5 StartZ=0 EndX=155 EndY=-47.5 EndZ=0
    g46: LineSegment StartX=155 StartY=-47.5 StartZ=0 EndX=145 EndY=-47.5 EndZ=0
    g47: LineSegment StartX=125 StartY=-43 StartZ=0 EndX=125 EndY=-27.5 EndZ=0
  constraints (124):
    c: Coincident(g0,g1)
    c: Coincident(g1,g2)
    c: Coincident(g3,g0)
    c: Horizontal(g0)
    c: Horizontal(g2)
    c: Vertical(g1)
    c: Vertical(g3)
    c: Coincident(g4,g5)
    c: Coincident(g5,g6)
    c: Coincident(g6,g7)
    c: Coincident(g7,g4)
    c: Horizontal(g4)
    c: Horizontal(g6)
    c: Vertical(g5)
    c: Vertical(g7)
    c: Coincident(g8,g9)
    c: Coincident(g9,g10)
    c: Coincident(g10,g11)
    c: Coincident(g11,g8)
    c: Horizontal(g8)
    c: Horizontal(g10)
    c: Vertical(g9)
    c: Vertical(g11)
    c: Coincident(g12,g13)
    c: Coincident(g14,g15)
    c: Coincident(g15,g12)
    c: Horizontal(g12)
    c: Horizontal(g14)
    c: Vertical(g13)
    c: Vertical(g15)
    c: Coincident(g16,g17)
    c: Coincident(g17,g18)
    c: Coincident(g18,g19)
    c: Horizontal(g16)
    c: Horizontal(g18)
    c: Vertical(g17)
    c: Vertical(g19)
    c: Coincident(g20,g21)
    c: Coincident(g21,g22)
    c: Coincident(g22,g23)
    c: Coincident(g23,g20)
    c: Horizontal(g20)
    c: Horizontal(g22)
    c: Vertical(g21)
    c: Vertical(g23)
    c: Coincident(g24,g25)
    c: Coincident(g25,g26)
    c: Coincident(g26,g27)
    c: Coincident(g27,g24)
    c: Horizontal(g24)
    c: Horizontal(g26)
    c: Vertical(g25)
    c: Vertical(g27)
    c: Coincident(g29,g30)
    c: Coincident(g30,g31)
    c: Coincident(g31,g28)
    c: Horizontal(g28)
    c: Horizontal(g30)
    c: Vertical(g29)
    c: Vertical(g31)
    c: Coincident(g0,g-3)
    c: Coincident(g1,g-4)
    c: Coincident(g4,g-5)
    c: Coincident(g5,g-6)
    c: Coincident(g8,g-7)
    c: Coincident(g9,g-9)
    c: Coincident(g12,g-8)
    c: Coincident(g17,g-17)
    c: Coincident(g20,g-16)
    c: Coincident(g21,g-15)
    c: Coincident(g24,g-14)
    c: Coincident(g25,g-13)
    c: Coincident(g28,g-12)
    c: Coincident(g29,g-11)
    c: Coincident(g33,g34)
    c: Coincident(g34,g35)
    c: Coincident(g35,g32)
    c: Horizontal(g32)
    c: Horizontal(g34)
    c: Vertical(g33)
    c: Vertical(g35)
    c: Coincident(g33,g-20)
    c: Coincident(g36,g37)
    c: Coincident(g38,g39)
    c: Coincident(g39,g36)
    c: Horizontal(g36)
    c: Horizontal(g38)
    c: Vertical(g37)
    c: Vertical(g39)
    c: Coincident(g36,g-22)
    c: Coincident(g38,g-22)
    c: Coincident(g36,g-21)
    c: Coincident(g36,g-21)
    c: Coincident(g32,g-19)
    c: Coincident(g40,g41)
    c: Coincident(g41,g42)
    c: Coincident(g42,g43)
    c: Horizontal(g40)
    c: Horizontal(g42)
    c: Vertical(g41)
    c: Vertical(g43)
    c: Coincident(g40,g-24)
    c: Coincident(g42,g-23)
    c: Coincident(g44,g45)
    c: Coincident(g45,g46)
    c: Coincident(g47,g44)
    c: Horizontal(g44)
    c: Horizontal(g46)
    c: Vertical(g45)
    c: Vertical(g47)
    c: Coincident(g45,g-26)
    c: Coincident(g44,g-25)
    c: Coincident(g47,g28)
    c: Coincident(g29,g46)
    c: Coincident(g40,g13)
    c: Coincident(g43,g14)
    c: Coincident(g14,g-8)
    c: Coincident(g12,g-10)
    c: Coincident(g3,g32)
    c: Coincident(g2,g33)
    c: Coincident(g38,g19)
    c: Coincident(g37,g16)
    c: Coincident(g18,g-18)
    c: Coincident(g16,g-17)
FEATURE [PartDesign::Pocket] Pocket006  label="TopOut_Locks_Pocket"
  BaseFeature = -> Pad002
  Length = 5
  Length2 = 100
  Placement = pos=(0,83,0) rot=(1,0,0;1.5708rad)
  Profile = -> Sketch023
  Type = 1
FEATURE [PartDesign::ShapeBinder] ShapeBinder029
  Placement = pos=(0,0,0) rot=(1,0,0;1.5708rad)
  Support = -> [Sketch019]
FEATURE [Sketcher::SketchObject] Sketch024  label="TopIn_Locks_Sketch"
  ExternalGeometry = -> [ShapeBinder029]
  MapMode = 5
  Placement = pos=(0,79,0) rot=(-1,0,0;1.5708rad)
  Support = -> [Pad003]
  sketch-geometry (32):
    g0: LineSegment StartX=-145 StartY=30 StartZ=0 EndX=-100 EndY=30 EndZ=0
    g1: LineSegment StartX=-100 StartY=30 StartZ=0 EndX=-100 EndY=8e-12 EndZ=0
    g2: LineSegment StartX=-100 StartY=8e-12 StartZ=0 EndX=-125 EndY=8e-12 EndZ=0
    g3: LineSegment StartX=-145 StartY=4.5 StartZ=0 EndX=-145 EndY=30 EndZ=0
    g4: LineSegment StartX=-60 StartY=30 StartZ=0 EndX=-20 EndY=30 EndZ=0
    g5: LineSegment StartX=-20 StartY=30 StartZ=0 EndX=-20 EndY=8e-12 EndZ=0
    g6: LineSegment StartX=-20 StartY=8e-12 StartZ=0 EndX=-60 EndY=8e-12 EndZ=0
    g7: LineSegment StartX=-60 StartY=8e-12 StartZ=0 EndX=-60 EndY=30 EndZ=0
    g8: LineSegment StartX=20 StartY=30 StartZ=0 EndX=60 EndY=30 EndZ=0
    g9: LineSegment StartX=60 StartY=30 StartZ=0 EndX=60 EndY=8e-12 EndZ=0
    g10: LineSegment StartX=60 StartY=8e-12 StartZ=0 EndX=20 EndY=8e-12 EndZ=0
    g11: LineSegment StartX=20 StartY=8e-12 StartZ=0 EndX=20 EndY=30 EndZ=0
    g12: LineSegment StartX=100 StartY=30 StartZ=0 EndX=145 EndY=30 EndZ=0
    g13: LineSegment StartX=145 StartY=30 StartZ=0 EndX=145 EndY=4.5 EndZ=0
    g14: LineSegment StartX=125 StartY=8e-12 StartZ=0 EndX=100 EndY=8e-12 EndZ=0
    g15: LineSegment StartX=100 StartY=8e-12 StartZ=0 EndX=100 EndY=30 EndZ=0
    g16: LineSegment StartX=-155 StartY=4.5 StartZ=0 EndX=-145 EndY=4.5 EndZ=0
    g17: LineSegment StartX=-125 StartY=8e-12 StartZ=0 EndX=-125 EndY=-15.5 EndZ=0
    g18: LineSegment StartX=-125 StartY=-15.5 StartZ=0 EndX=-155 EndY=-15.5 EndZ=0
    g19: LineSegment StartX=-155 StartY=-15.5 StartZ=0 EndX=-155 EndY=4.5 EndZ=0
    g20: LineSegment StartX=-125 StartY=-27.5 StartZ=0 EndX=-155 EndY=-27.5 EndZ=0
    g21: LineSegment StartX=-155 StartY=-27.5 StartZ=0 EndX=-155 EndY=-47.5 EndZ=0
    g22: LineSegment StartX=-155 StartY=-47.5 StartZ=0 EndX=-125 EndY=-47.5 EndZ=0
    g23: LineSegment StartX=-125 StartY=-47.5 StartZ=0 EndX=-125 EndY=-27.5 EndZ=0
    g24: LineSegment StartX=125 StartY=-27.5 StartZ=0 EndX=155 EndY=-27.5 EndZ=0
    g25: LineSegment StartX=155 StartY=-27.5 StartZ=0 EndX=155 EndY=-47.5 EndZ=0
    g26: LineSegment StartX=155 StartY=-47.5 StartZ=0 EndX=125 EndY=-47.5 EndZ=0
    g27: LineSegment StartX=125 StartY=-47.5 StartZ=0 EndX=125 EndY=-27.5 EndZ=0
    g28: LineSegment StartX=125 StartY=-15.5 StartZ=0 EndX=155 EndY=-15.5 EndZ=0
    g29: LineSegment StartX=155 StartY=-15.5 StartZ=0 EndX=155 EndY=4.5 EndZ=0
    g30: LineSegment StartX=155 StartY=4.5 StartZ=0 EndX=145 EndY=4.5 EndZ=0
    g31: LineSegment StartX=125 StartY=8e-12 StartZ=0 EndX=125 EndY=-15.5 EndZ=0
  constraints (81):
    c: Coincident(g0,g1)
    c: Coincident(g1,g2)
    c: Coincident(g3,g0)
    c: Horizontal(g0)
    c: Horizontal(g2)
    c: Vertical(g1)
    c: Vertical(g3)
    c: Coincident(g0,g-4)
    c: Coincident(g1,g-3)
    c: Coincident(g4,g5)
    c: Coincident(g5,g6)
    c: Coincident(g6,g7)
    c: Coincident(g7,g4)
    c: Horizontal(g4)
    c: Horizontal(g6)
    c: Vertical(g5)
    c: Vertical(g7)
    c: Coincident(g4,g-5)
    c: Coincident(g8,g9)
    c: Coincident(g9,g10)
    c: Coincident(g10,g11)
    c: Coincident(g11,g8)
    c: Horizontal(g8)
    c: Horizontal(g10)
    c: Vertical(g9)
    c: Vertical(g11)
    c: Coincident(g8,g-6)
    c: Coincident(g12,g13)
    c: Coincident(g14,g15)
    c: Coincident(g15,g12)
    c: Horizontal(g12)
    c: Horizontal(g14)
    c: Vertical(g13)
    c: Vertical(g15)
    c: Coincident(g12,g-9)
    c: Coincident(g9,g-8)
    c: Coincident(g5,g-7)
    c: Coincident(g17,g18)
    c: Coincident(g18,g19)
    c: Coincident(g19,g16)
    c: Horizontal(g16)
    c: Horizontal(g18)
    c: Vertical(g17)
    c: Vertical(g19)
    c: Coincident(g16,g-11)
    c: Coincident(g17,g-12)
    c: Coincident(g20,g21)
    c: Coincident(g21,g22)
    c: Coincident(g22,g23)
    c: Coincident(g23,g20)
    c: Horizontal(g20)
    c: Horizontal(g22)
    c: Vertical(g21)
    c: Vertical(g23)
    c: Coincident(g20,g-13)
    c: Coincident(g21,g-14)
    c: Coincident(g24,g25)
    c: Coincident(g25,g26)
    c: Coincident(g26,g27)
    c: Coincident(g27,g24)
    c: Horizontal(g24)
    c: Horizontal(g26)
    c: Vertical(g25)
    c: Vertical(g27)
    c: Coincident(g24,g-15)
    c: Coincident(g28,g29)
    c: Coincident(g29,g30)
    c: Coincident(g31,g28)
    c: Horizontal(g28)
    c: Horizontal(g30)
    c: Vertical(g29)
    c: Vertical(g31)
    c: Coincident(g28,g-17)
    c: Coincident(g29,g-18)
    c: Coincident(g25,g-16)
    c: Coincident(g2,g17)
    c: Coincident(g3,g16)
    c: Coincident(g13,g30)
    c: Coincident(g31,g14)
    c: Coincident(g12,g-10)
    c: Coincident(g14,g-9)
FEATURE [PartDesign::Pocket] Pocket007  label="TopIn_Locks_Pocket"
  BaseFeature = -> Pad003
  Length = 5
  Length2 = 100
  Placement = pos=(0,79,0) rot=(1,0,0;1.5708rad)
  Profile = -> Sketch024
  Type = 1
FEATURE [PartDesign::ShapeBinder] ShapeBinder030 .. ShapeBinder033  x4 (patterned run collapsed; names and placements below)
  Support = -> [Sketch020]
  placements: all 4 at pos=(0,0,0) rot=(0.57735,0.57735,0.57735;2.0944rad)
FEATURE [TechDraw::DrawSVGTemplate] Template  label="LibSlide_Template"
  EditableTexts = Designed by Name=Stefan Krüger; Drawing number=1; FC-Date=17.07.2017; FC-SC=1:1; FC-SH=Sheet; FC-Title=BreadBoardBox; Subtitle=LidSlide; Weight=-
  Height = 210
  Orientation = 1
  Width = 297
FEATURE [Sketcher::SketchObject] Sketch025  label="RightOut_Locks_Sketch"
  ExternalGeometry = -> [ShapeBinder030]
  MapMode = 5
  Placement = pos=(133,0,-4) rot=(0.57735,-0.57735,0.57735;4.18879rad)
  Support = -> [Pad006]
  sketch-geometry (20):
    g0: LineSegment StartX=-100 StartY=26 StartZ=0 EndX=-60 EndY=26 EndZ=0
    g1: LineSegment StartX=-60 StartY=26 StartZ=0 EndX=-60 EndY=-4 EndZ=0
    g2: LineSegment StartX=-60 StartY=-4 StartZ=0 EndX=-100 EndY=-4 EndZ=0
    g3: LineSegment StartX=-100 StartY=-4 StartZ=0 EndX=-100 EndY=26 EndZ=0
    g4: LineSegment StartX=-20 StartY=26 StartZ=0 EndX=20 EndY=26 EndZ=0
    g5: LineSegment StartX=20 StartY=26 StartZ=0 EndX=20 EndY=-4 EndZ=0
    g6: LineSegment StartX=20 StartY=-4 StartZ=0 EndX=-20 EndY=-4 EndZ=0
    g7: LineSegment StartX=-20 StartY=-4 StartZ=0 EndX=-20 EndY=26 EndZ=0
    g8: LineSegment StartX=60 StartY=26 StartZ=0 EndX=100 EndY=26 EndZ=0
    g9: LineSegment StartX=100 StartY=26 StartZ=0 EndX=100 EndY=-4 EndZ=0
    g10: LineSegment StartX=100 StartY=-4 StartZ=0 EndX=60 EndY=-4 EndZ=0
    g11: LineSegment StartX=60 StartY=-4 StartZ=0 EndX=60 EndY=26 EndZ=0
    g12: LineSegment StartX=-115 StartY=-19.5 StartZ=0 EndX=-75 EndY=-19.5 EndZ=0
    g13: LineSegment StartX=-75 StartY=-19.5 StartZ=0 EndX=-75 EndY=-31.5 EndZ=0
    g14: LineSegment StartX=-75 StartY=-31.5 StartZ=0 EndX=-115 EndY=-31.5 EndZ=0
    g15: LineSegment StartX=-115 StartY=-31.5 StartZ=0 EndX=-115 EndY=-19.5 EndZ=0
    g16: LineSegment StartX=75 StartY=-19.5 StartZ=0 EndX=115 EndY=-19.5 EndZ=0
    g17: LineSegment StartX=115 StartY=-19.5 StartZ=0 EndX=115 EndY=-31.5 EndZ=0
    g18: LineSegment StartX=115 StartY=-31.5 StartZ=0 EndX=75 EndY=-31.5 EndZ=0
    g19: LineSegment StartX=75 StartY=-31.5 StartZ=0 EndX=75 EndY=-19.5 EndZ=0
  constraints (50):
    c: Coincident(g0,g1)
    c: Coincident(g1,g2)
    c: Coincident(g2,g3)
    c: Coincident(g3,g0)
    c: Horizontal(g0)
    c: Horizontal(g2)
    c: Vertical(g1)
    c: Vertical(g3)
    c: Coincident(g1,g-3)
    c: Coincident(g4,g5)
    c: Coincident(g5,g6)
    c: Coincident(g6,g7)
    c: Coincident(g7,g4)
    c: Horizontal(g4)
    c: Horizontal(g6)
    c: Vertical(g5)
    c: Vertical(g7)
    c: Coincident(g4,g-4)
    c: Coincident(g5,g-6)
    c: Coincident(g8,g9)
    c: Coincident(g9,g10)
    c: Coincident(g10,g11)
    c: Coincident(g11,g8)
    c: Horizontal(g8)
    c: Horizontal(g10)
    c: Vertical(g9)
    c: Vertical(g11)
    c: Coincident(g8,g-7)
    c: Coincident(g9,g-8)
    c: Coincident(g0,g-5)
    c: Coincident(g12,g13)
    c: Coincident(g13,g14)
    c: Coincident(g14,g15)
    c: Coincident(g15,g12)
    c: Horizontal(g12)
    c: Horizontal(g14)
    c: Vertical(g13)
    c: Vertical(g15)
    c: Coincident(g12,g-9)
    c: Coincident(g13,g-10)
    c: Coincident(g16,g17)
    c: Coincident(g17,g18)
    c: Coincident(g18,g19)
    c: Coincident(g19,g16)
    c: Horizontal(g16)
    c: Horizontal(g18)
    c: Vertical(g17)
    c: Vertical(g19)
    c: Coincident(g17,g-12)
    c: Coincident(g16,g-11)
FEATURE [PartDesign::Pocket] Pocket008  label="RightOut_Locks_Pocket"
  BaseFeature = -> Pad006
  Length = 5
  Length2 = 100
  Placement = pos=(133,0,-4) rot=(0.57735,-0.57735,-0.57735;2.0944rad)
  Profile = -> Sketch025
  Type = 1
FEATURE [PartDesign::Body] Body  label="RightOut_Body"
  Group = -> [DatumPlane005,ShapeBinder008,ShapeBinder009,Sketch009,Pad006,ShapeBinder010,ShapeBinder030,Sketch025,Pocket008]
  Origin = -> Origin003
  Tip = -> Pocket008
FEATURE [Sketcher::SketchObject] Sketch026  label="RightIn_Locks_Sketch"
  ExternalGeometry = -> [ShapeBinder031]
  MapMode = 5
  Placement = pos=(129,0,-4) rot=(0.57735,-0.57735,0.57735;4.18879rad)
  Support = -> [Pad007]
  sketch-geometry (20):
    g0: LineSegment StartX=-100 StartY=26 StartZ=0 EndX=-60 EndY=26 EndZ=0
    g1: LineSegment StartX=-60 StartY=26 StartZ=0 EndX=-60 EndY=-4 EndZ=0
    g2: LineSegment StartX=-60 StartY=-4 StartZ=0 EndX=-100 EndY=-4 EndZ=0
    g3: LineSegment StartX=-100 StartY=-4 StartZ=0 EndX=-100 EndY=26 EndZ=0
    g4: LineSegment StartX=-20 StartY=26 StartZ=0 EndX=20 EndY=26 EndZ=0
    g5: LineSegment StartX=20 StartY=26 StartZ=0 EndX=20 EndY=-4 EndZ=0
    g6: LineSegment StartX=20 StartY=-4 StartZ=0 EndX=-20 EndY=-4 EndZ=0
    g7: LineSegment StartX=-20 StartY=-4 StartZ=0 EndX=-20 EndY=26 EndZ=0
    g8: LineSegment StartX=60 StartY=26 StartZ=0 EndX=100 EndY=26 EndZ=0
    g9: LineSegment StartX=100 StartY=26 StartZ=0 EndX=100 EndY=-4 EndZ=0
    g10: LineSegment StartX=100 StartY=-4 StartZ=0 EndX=60 EndY=-4 EndZ=0
    g11: LineSegment StartX=60 StartY=-4 StartZ=0 EndX=60 EndY=26 EndZ=0
    g12: LineSegment StartX=75 StartY=-19.5 StartZ=0 EndX=115 EndY=-19.5 EndZ=0
    g13: LineSegment StartX=115 StartY=-19.5 StartZ=0 EndX=115 EndY=-31.5 EndZ=0
    g14: LineSegment StartX=115 StartY=-31.5 StartZ=0 EndX=75 EndY=-31.5 EndZ=0
    g15: LineSegment StartX=75 StartY=-31.5 StartZ=0 EndX=75 EndY=-19.5 EndZ=0
    g16: LineSegment StartX=-115 StartY=-19.5 StartZ=0 EndX=-75 EndY=-19.5 EndZ=0
    g17: LineSegment StartX=-75 StartY=-19.5 StartZ=0 EndX=-75 EndY=-31.5 EndZ=0
    g18: LineSegment StartX=-75 StartY=-31.5 StartZ=0 EndX=-115 EndY=-31.5 EndZ=0
    g19: LineSegment StartX=-115 StartY=-31.5 StartZ=0 EndX=-115 EndY=-19.5 EndZ=0
  constraints (50):
    c: Coincident(g0,g1)
    c: Coincident(g1,g2)
    c: Coincident(g2,g3)
    c: Coincident(g3,g0)
    c: Horizontal(g0)
    c: Horizontal(g2)
    c: Vertical(g1)
    c: Vertical(g3)
    c: Coincident(g0,g-3)
    c: Coincident(g1,g-4)
    c: Coincident(g4,g5)
    c: Coincident(g5,g6)
    c: Coincident(g6,g7)
    c: Coincident(g7,g4)
    c: Horizontal(g4)
    c: Horizontal(g6)
    c: Vertical(g5)
    c: Vertical(g7)
    c: Coincident(g4,g-5)
    c: Coincident(g5,g-6)
    c: Coincident(g8,g9)
    c: Coincident(g9,g10)
    c: Coincident(g10,g11)
    c: Coincident(g11,g8)
    c: Horizontal(g8)
    c: Horizontal(g10)
    c: Vertical(g9)
    c: Vertical(g11)
    c: Coincident(g8,g-7)
    c: Coincident(g9,g-8)
    c: Coincident(g12,g13)
    c: Coincident(g13,g14)
    c: Coincident(g14,g15)
    c: Coincident(g15,g12)
    c: Horizontal(g12)
    c: Horizontal(g14)
    c: Vertical(g13)
    c: Vertical(g15)
    c: Coincident(g12,g-11)
    c: Coincident(g13,g-12)
    c: Coincident(g16,g17)
    c: Coincident(g17,g18)
    c: Coincident(g18,g19)
    c: Coincident(g19,g16)
    c: Horizontal(g16)
    c: Horizontal(g18)
    c: Vertical(g17)
    c: Vertical(g19)
    c: Coincident(g16,g-9)
    c: Coincident(g17,g-10)
FEATURE [PartDesign::Pocket] Pocket009  label="RightIn_Locks_Pocket"
  BaseFeature = -> Pad007
  Length = 5
  Length2 = 100
  Placement = pos=(129,0,-4) rot=(0.57735,-0.57735,-0.57735;2.0944rad)
  Profile = -> Sketch026
  Type = 1
FEATURE [PartDesign::Body] Body003  label="RightIn_Body"
  Group = -> [DatumPlane006,ShapeBinder011,Sketch010,Pad007,ShapeBinder031,Sketch026,Pocket009]
  Origin = -> Origin007
  Tip = -> Pocket009
FEATURE [Sketcher::SketchObject] Sketch027  label="LeftOut_Locks_Sketch"
  ExternalGeometry = -> [ShapeBinder032]
  MapMode = 5
  Placement = pos=(-133,0,-4) rot=(0.57735,0.57735,-0.57735;4.18879rad)
  Support = -> [Pad004]
  sketch-geometry (32):
    g0: LineSegment StartX=-100 StartY=26 StartZ=0 EndX=-60 EndY=26 EndZ=0
    g1: LineSegment StartX=-60 StartY=26 StartZ=0 EndX=-60 EndY=-4 EndZ=0
    g2: LineSegment StartX=-60 StartY=-4 StartZ=0 EndX=-100 EndY=-4 EndZ=0
    g3: LineSegment StartX=-100 StartY=-4 StartZ=0 EndX=-100 EndY=26 EndZ=0
    g4: LineSegment StartX=-20 StartY=26 StartZ=0 EndX=20 EndY=26 EndZ=0
    g5: LineSegment StartX=20 StartY=26 StartZ=0 EndX=20 EndY=-4 EndZ=0
    g6: LineSegment StartX=20 StartY=-4 StartZ=0 EndX=-20 EndY=-4 EndZ=0
    g7: LineSegment StartX=-20 StartY=-4 StartZ=0 EndX=-20 EndY=26 EndZ=0
    g8: LineSegment StartX=60 StartY=26 StartZ=0 EndX=100 EndY=26 EndZ=0
    g9: LineSegment StartX=100 StartY=26 StartZ=0 EndX=100 EndY=-4 EndZ=0
    g10: LineSegment StartX=100 StartY=-4 StartZ=0 EndX=60 EndY=-4 EndZ=0
    g11: LineSegment StartX=60 StartY=-4 StartZ=0 EndX=60 EndY=26 EndZ=0
    g12: LineSegment StartX=-100 StartY=-47 StartZ=0 EndX=-60 EndY=-47 EndZ=0
    g13: LineSegment StartX=-60 StartY=-47 StartZ=0 EndX=-60 EndY=-77 EndZ=0
    g14: LineSegment StartX=-60 StartY=-77 StartZ=0 EndX=-100 EndY=-77 EndZ=0
    g15: LineSegment StartX=-100 StartY=-77 StartZ=0 EndX=-100 EndY=-47 EndZ=0
    g16: LineSegment StartX=-20 StartY=-47 StartZ=0 EndX=20 EndY=-47 EndZ=0
    g17: LineSegment StartX=20 StartY=-47 StartZ=0 EndX=20 EndY=-77 EndZ=0
    g18: LineSegment StartX=20 StartY=-77 StartZ=0 EndX=-20 EndY=-77 EndZ=0
    g19: LineSegment StartX=-20 StartY=-77 StartZ=0 EndX=-20 EndY=-47 EndZ=0
    g20: LineSegment StartX=60 StartY=-47 StartZ=0 EndX=100 EndY=-47 EndZ=0
    g21: LineSegment StartX=100 StartY=-47 StartZ=0 EndX=100 EndY=-77 EndZ=0
    g22: LineSegment StartX=100 StartY=-77 StartZ=0 EndX=60 EndY=-77 EndZ=0
    g23: LineSegment StartX=60 StartY=-77 StartZ=0 EndX=60 EndY=-47 EndZ=0
    g24: LineSegment StartX=-115 StartY=-19.5 StartZ=0 EndX=-75 EndY=-19.5 EndZ=0
    g25: LineSegment StartX=-75 StartY=-19.5 StartZ=0 EndX=-75 EndY=-31.5 EndZ=0
    g26: LineSegment StartX=-75 StartY=-31.5 StartZ=0 EndX=-115 EndY=-31.5 EndZ=0
    g27: LineSegment StartX=-115 StartY=-31.5 StartZ=0 EndX=-115 EndY=-19.5 EndZ=0
    g28: LineSegment StartX=75 StartY=-19.5 StartZ=0 EndX=115 EndY=-19.5 EndZ=0
    g29: LineSegment StartX=115 StartY=-19.5 StartZ=0 EndX=115 EndY=-31.5 EndZ=0
    g30: LineSegment StartX=115 StartY=-31.5 StartZ=0 EndX=75 EndY=-31.5 EndZ=0
    g31: LineSegment StartX=75 StartY=-31.5 StartZ=0 EndX=75 EndY=-19.5 EndZ=0
  constraints (80):
    c: Coincident(g0,g1)
    c: Coincident(g1,g2)
    c: Coincident(g2,g3)
    c: Coincident(g3,g0)
    c: Horizontal(g0)
    c: Horizontal(g2)
    c: Vertical(g1)
    c: Vertical(g3)
    c: Coincident(g0,g-3)
    c: Coincident(g1,g-4)
    c: Coincident(g4,g5)
    c: Coincident(g5,g6)
    c: Coincident(g6,g7)
    c: Coincident(g7,g4)
    c: Horizontal(g4)
    c: Horizontal(g6)
    c: Vertical(g5)
    c: Vertical(g7)
    c: Coincident(g4,g-5)
    c: Coincident(g5,g-6)
    c: Coincident(g8,g9)
    c: Coincident(g9,g10)
    c: Coincident(g10,g11)
    c: Coincident(g11,g8)
    c: Horizontal(g8)
    c: Horizontal(g10)
    c: Vertical(g9)
    c: Vertical(g11)
    c: Coincident(g8,g-7)
    c: Coincident(g9,g-8)
    c: Coincident(g12,g13)
    c: Coincident(g13,g14)
    c: Coincident(g14,g15)
    c: Coincident(g15,g12)
    c: Horizontal(g12)
    c: Horizontal(g14)
    c: Vertical(g13)
    c: Vertical(g15)
    c: Coincident(g12,g-12)
    c: Coincident(g13,g-13)
    c: Coincident(g16,g17)
    c: Coincident(g17,g18)
    c: Coincident(g18,g19)
    c: Coincident(g19,g16)
    c: Horizontal(g16)
    c: Horizontal(g18)
    c: Vertical(g17)
    c: Vertical(g19)
    c: Coincident(g16,g-14)
    c: Coincident(g17,g-11)
    c: Coincident(g20,g21)
    c: Coincident(g21,g22)
    c: Coincident(g22,g23)
    c: Coincident(g23,g20)
    c: Horizontal(g20)
    c: Horizontal(g22)
    c: Vertical(g21)
    c: Vertical(g23)
    c: Coincident(g20,g-9)
    c: Coincident(g21,g-10)
    c: Coincident(g24,g25)
    c: Coincident(g25,g26)
    c: Coincident(g26,g27)
    c: Coincident(g27,g24)
    c: Horizontal(g24)
    c: Horizontal(g26)
    c: Vertical(g25)
    c: Vertical(g27)
    c: Coincident(g24,g-15)
    c: Coincident(g25,g-16)
    c: Coincident(g28,g29)
    c: Coincident(g29,g30)
    c: Coincident(g30,g31)
    c: Coincident(g31,g28)
    c: Horizontal(g28)
    c: Horizontal(g30)
    c: Vertical(g29)
    c: Vertical(g31)
    c: Coincident(g28,g-17)
    c: Coincident(g29,g-18)
FEATURE [PartDesign::Pocket] Pocket010  label="LeftOut_Locks_Pocket"
  BaseFeature = -> Pad004
  Length = 5
  Length2 = 100
  Placement = pos=(-133,0,-4) rot=(0.57735,0.57735,0.57735;2.0944rad)
  Profile = -> Sketch027
  Type = 1
FEATURE [PartDesign::Body] Body004  label="LeftOut_Body"
  Group = -> [DatumPlane003,ShapeBinder004,ShapeBinder005,Sketch007,Pad004,ShapeBinder032,Sketch027,Pocket010]
  Origin = -> Origin009
  Tip = -> Pocket010
FEATURE [Sketcher::SketchObject] Sketch028  label="LeftIn_Locks_Sketch"
  ExternalGeometry = -> [ShapeBinder033]
  MapMode = 5
  Placement = pos=(-129,0,-4) rot=(0.57735,0.57735,-0.57735;4.18879rad)
  Support = -> [Pad005]
  sketch-geometry (20):
    g0: LineSegment StartX=-100 StartY=26 StartZ=0 EndX=-60 EndY=26 EndZ=0
    g1: LineSegment StartX=-60 StartY=26 StartZ=0 EndX=-60 EndY=-4 EndZ=0
    g2: LineSegment StartX=-60 StartY=-4 StartZ=0 EndX=-100 EndY=-4 EndZ=0
    g3: LineSegment StartX=-100 StartY=-4 StartZ=0 EndX=-100 EndY=26 EndZ=0
    g4: LineSegment StartX=-20 StartY=26 StartZ=0 EndX=20 EndY=26 EndZ=0
    g5: LineSegment StartX=20 StartY=26 StartZ=0 EndX=20 EndY=-4 EndZ=0
    g6: LineSegment StartX=20 StartY=-4 StartZ=0 EndX=-20 EndY=-4 EndZ=0
    g7: LineSegment StartX=-20 StartY=-4 StartZ=0 EndX=-20 EndY=26 EndZ=0
    g8: LineSegment StartX=60 StartY=26 StartZ=0 EndX=100 EndY=26 EndZ=0
    g9: LineSegment StartX=100 StartY=26 StartZ=0 EndX=100 EndY=-4 EndZ=0
    g10: LineSegment StartX=100 StartY=-4 StartZ=0 EndX=60 EndY=-4 EndZ=0
    g11: LineSegment StartX=60 StartY=-4 StartZ=0 EndX=60 EndY=26 EndZ=0
    g12: LineSegment StartX=-115 StartY=-19.5 StartZ=0 EndX=-75 EndY=-19.5 EndZ=0
    g13: LineSegment StartX=-75 StartY=-19.5 StartZ=0 EndX=-75 EndY=-31.5 EndZ=0
    g14: LineSegment StartX=-75 StartY=-31.5 StartZ=0 EndX=-115 EndY=-31.5 EndZ=0
    g15: LineSegment StartX=-115 StartY=-31.5 StartZ=0 EndX=-115 EndY=-19.5 EndZ=0
    g16: LineSegment StartX=75 StartY=-19.5 StartZ=0 EndX=115 EndY=-19.5 EndZ=0
    g17: LineSegment StartX=115 StartY=-19.5 StartZ=0 EndX=115 EndY=-31.5 EndZ=0
    g18: LineSegment StartX=115 StartY=-31.5 StartZ=0 EndX=75 EndY=-31.5 EndZ=0
    g19: LineSegment StartX=75 StartY=-31.5 StartZ=0 EndX=75 EndY=-19.5 EndZ=0
  constraints (50):
    c: Coincident(g0,g1)
    c: Coincident(g1,g2)
    c: Coincident(g2,g3)
    c: Coincident(g3,g0)
    c: Horizontal(g0)
    c: Horizontal(g2)
    c: Vertical(g1)
    c: Vertical(g3)
    c: Coincident(g0,g-3)
    c: Coincident(g1,g-4)
    c: Coincident(g4,g5)
    c: Coincident(g5,g6)
    c: Coincident(g6,g7)
    c: Coincident(g7,g4)
    c: Horizontal(g4)
    c: Horizontal(g6)
    c: Vertical(g5)
    c: Vertical(g7)
    c: Coincident(g4,g-5)
    c: Coincident(g5,g-6)
    c: Coincident(g8,g9)
    c: Coincident(g9,g10)
    c: Coincident(g10,g11)
    c: Coincident(g11,g8)
    c: Horizontal(g8)
    c: Horizontal(g10)
    c: Vertical(g9)
    c: Vertical(g11)
    c: Coincident(g9,g-8)
    c: Coincident(g8,g-7)
    c: Coincident(g12,g13)
    c: Coincident(g13,g14)
    c: Coincident(g14,g15)
    c: Coincident(g15,g12)
    c: Horizontal(g12)
    c: Horizontal(g14)
    c: Vertical(g13)
    c: Vertical(g15)
    c: Coincident(g12,g-9)
    c: Coincident(g13,g-10)
    c: Coincident(g16,g17)
    c: Coincident(g17,g18)
    c: Coincident(g18,g19)
    c: Coincident(g19,g16)
    c: Horizontal(g16)
    c: Horizontal(g18)
    c: Vertical(g17)
    c: Vertical(g19)
    c: Coincident(g16,g-11)
    c: Coincident(g17,g-12)
FEATURE [PartDesign::Pocket] Pocket011  label="LeftIn_Locks_Pocket"
  BaseFeature = -> Pad005
  Length = 5
  Length2 = 100
  Placement = pos=(-129,0,-4) rot=(0.57735,0.57735,0.57735;2.0944rad)
  Profile = -> Sketch028
  Type = 1
FEATURE [Sketcher::SketchObject] Sketch029  label="LidOut_Window_Sketch"
  ExternalGeometry = -> [Pocket003]
  MapMode = 5
  Placement = pos=(-31.1547,0,47) rot=(0,0,-1;1.5708rad)
  Support = -> [Pocket003]
  sketch-geometry (19):
    g0: LineSegment StartX=-63 StartY=154.155 StartZ=0 EndX=63 EndY=154.155 EndZ=0
    g1: LineSegment StartX=73 StartY=144.155 StartZ=0 EndX=73 EndY=-81.8453 EndZ=0
    g2: LineSegment StartX=63 StartY=-91.8453 StartZ=0 EndX=-51 EndY=-91.8453 EndZ=0
    g3: LineSegment StartX=-73 StartY=-13.515 StartZ=0 EndX=-73 EndY=144.155 EndZ=0
    g4: LineSegment [constr] StartX=-83 StartY=164.155 StartZ=0 EndX=-63 EndY=164.155 EndZ=0
    g5: LineSegment [constr] StartX=-63 StartY=164.155 StartZ=0 EndX=-63 EndY=144.155 EndZ=0
    g6: LineSegment [constr] StartX=-63 StartY=144.155 StartZ=0 EndX=-83 EndY=144.155 EndZ=0
    g7: LineSegment [constr] StartX=-83 StartY=144.155 StartZ=0 EndX=-83 EndY=164.155 EndZ=0
    g8: LineSegment [constr] StartX=63 StartY=-81.8453 StartZ=0 EndX=83 EndY=-81.8453 EndZ=0
    g9: LineSegment [constr] StartX=83 StartY=-81.8453 StartZ=0 EndX=83 EndY=-101.845 EndZ=0
    g10: LineSegment [constr] StartX=83 StartY=-101.845 StartZ=0 EndX=63 EndY=-101.845 EndZ=0
    g11: LineSegment [constr] StartX=63 StartY=-101.845 StartZ=0 EndX=63 EndY=-81.8453 EndZ=0
    g12: ArcOfCircle CenterX=-63 CenterY=144.155 CenterZ=0 NormalX=0 NormalY=0 NormalZ=1 AngleXU=0 Radius=10 StartAngle=1.5708 EndAngle=3.14159
    g13: ArcOfCircle CenterX=63 CenterY=144.155 CenterZ=0 NormalX=0 NormalY=0 NormalZ=1 AngleXU=0 Radius=10 StartAngle=0 EndAngle=1.5708
    g14: ArcOfCircle CenterX=63 CenterY=-81.8453 CenterZ=0 NormalX=0 NormalY=0 NormalZ=1 AngleXU=0 Radius=10 StartAngle=4.71239 EndAngle=6.28319
    g15: ArcOfCircle CenterX=-51 CenterY=-81.8453 CenterZ=0 NormalX=0 NormalY=0 NormalZ=1 AngleXU=0 Radius=10 StartAngle=3.14159 EndAngle=4.71239
    g16: LineSegment StartX=-61 StartY=-81.8453 StartZ=0 EndX=-61 EndY=-31.8453 EndZ=0
    g17: ArcOfCircle CenterX=-71 CenterY=-31.8453 CenterZ=0 NormalX=0 NormalY=0 NormalZ=1 AngleXU=0 Radius=10 StartAngle=7e-12 EndAngle=1.15928
    g18: ArcOfCircle CenterX=-63 CenterY=-13.515 CenterZ=0 NormalX=0 NormalY=0 NormalZ=1 AngleXU=0 Radius=10 StartAngle=3.14159 EndAngle=4.30087
  constraints (50):
    c: Horizontal(g0)
    c: Horizontal(g2)
    c: Vertical(g1)
    c: Vertical(g3)
    c: Coincident(g4,g5)
    c: Coincident(g5,g6)
    c: Coincident(g6,g7)
    c: Coincident(g7,g4)
    c: Horizontal(g4)
    c: Horizontal(g6)
    c: Vertical(g5)
    c: Vertical(g7)
    c: Coincident(g4,g-3)
    c: Equal(g5,g6)
    c: Coincident(g8,g9)
    c: Coincident(g9,g10)
    c: Coincident(g10,g11)
    c: Coincident(g11,g8)
    c: Horizontal(g8)
    c: Horizontal(g10)
    c: Vertical(g9)
    c: Vertical(g11)
    c: Coincident(g9,g-5)
    c: Equal(g11,g10)
    c: Equal(g10,g5)
    c: DistanceY(g7,g7) = 20
    c: Tangent(g0,g12) = 1.5708
    c: Tangent(g3,g12) = 1.5708
    c: Tangent(g0,g13) = 1.5708
    c: Tangent(g1,g13) = 1.5708
    c: Tangent(g2,g14) = 1.5708
    c: Tangent(g1,g14) = 1.5708
    c: Tangent(g2,g15) = 1.5708
    c: Equal(g14,g15)
    c: Equal(g15,g13)
    c: Equal(g13,g12)
    c: Coincident(g5,g12)
    c: Coincident(g8,g14)
    c: Radius(g13) = 10
    c: DistanceY(g0,g4) = 10
    c: DistanceX(g-7,g3) = 6
    c: Vertical(g16)
    c: Tangent(g16,g15) = 1.5708
    c: Tangent(g3,g18) = 1.5708
    c: Tangent(g17,g18) = 1.5708
    c: Equal(g18,g17)
    c: Equal(g17,g15)
    c: Tangent(g16,g17) = -1.5708
    c: DistanceX(g3,g16) = 12
    c: DistanceY(g2,g16) = 60
FEATURE [PartDesign::Pocket] Pocket012  label="LidOut_Window_Pocket"
  BaseFeature = -> Pocket003
  Length = 5
  Length2 = 100
  Placement = pos=(-31.1547,0,47) rot=(0.707107,-0.707107,0;3.14159rad)
  Profile = -> Sketch029
  Type = 1
FEATURE [PartDesign::Body] Body013  label="LidOut_Body"
  Group = -> [DatumPlane009,ShapeBinder016,Sketch013,ShapeBinder017,ShapeBinder018,Pad010,ShapeBinder025,Sketch017,Pocket002,Mirrored004,Sketch018,Pocket003,Sketch029,Pocket012]
  Origin = -> Origin027
  Tip = -> Pocket012
FEATURE [Sketcher::SketchObject] Sketch030  label="TopOut_Connectors_Sketch"
  ExternalGeometry = -> [Pocket006]
  MapMode = 5
  Placement = pos=(0,83,0) rot=(-1,0,0;1.5708rad)
  Support = -> [Pocket006]
  expr: Constraints[55] = 3 + 2
  sketch-geometry (21):
    g0: LineSegment [constr] StartX=-94 StartY=-36 StartZ=0 EndX=-120 EndY=-36 EndZ=0
    g1: LineSegment [constr] StartX=-120 StartY=-36 StartZ=0 EndX=-120 EndY=-5 EndZ=0
    g2: LineSegment [constr] StartX=-120 StartY=-5 StartZ=0 EndX=-94 EndY=-5 EndZ=0
    g3: LineSegment [constr] StartX=-94 StartY=-5 StartZ=0 EndX=-94 EndY=-36 EndZ=0
    g4: LineSegment [constr] StartX=-66 StartY=-36 StartZ=0 EndX=-92 EndY=-36 EndZ=0
    g5: LineSegment [constr] StartX=-92 StartY=-36 StartZ=0 EndX=-92 EndY=-5 EndZ=0
    g6: LineSegment [constr] StartX=-92 StartY=-5 StartZ=0 EndX=-66 EndY=-5 EndZ=0
    g7: LineSegment [constr] StartX=-66 StartY=-5 StartZ=0 EndX=-66 EndY=-36 EndZ=0
    g8: LineSegment [constr] StartX=-94 StartY=-36 StartZ=0 EndX=-92 EndY=-36 EndZ=0
    g9: LineSegment StartX=-120 StartY=-3 StartZ=0 EndX=-66 EndY=-3 EndZ=0
    g10: LineSegment StartX=-64 StartY=-5 StartZ=0 EndX=-64 EndY=-36 EndZ=0
    g11: LineSegment StartX=-66 StartY=-38 StartZ=0 EndX=-120 EndY=-38 EndZ=0
    g12: LineSegment StartX=-122 StartY=-36 StartZ=0 EndX=-122 EndY=-5 EndZ=0
    g13: ArcOfCircle CenterX=-120 CenterY=-5 CenterZ=0 NormalX=0 NormalY=0 NormalZ=1 AngleXU=0 Radius=2 StartAngle=1.5708 EndAngle=3.14159
    g14: ArcOfCircle CenterX=-66 CenterY=-5 CenterZ=0 NormalX=0 NormalY=0 NormalZ=1 AngleXU=0 Radius=2 StartAngle=0 EndAngle=1.5708
    g15: ArcOfCircle CenterX=-66 CenterY=-36 CenterZ=0 NormalX=0 NormalY=0 NormalZ=1 AngleXU=0 Radius=2 StartAngle=4.71239 EndAngle=6.28319
    g16: ArcOfCircle CenterX=-120 CenterY=-36 CenterZ=0 NormalX=0 NormalY=0 NormalZ=1 AngleXU=0 Radius=2 StartAngle=3.14159 EndAngle=4.71239
    g17: LineSegment [constr] StartX=-125 StartY=-15.5 StartZ=0 EndX=-120 EndY=-15.5 EndZ=0
    g18: LineSegment [constr] StartX=-100 StartY=8e-12 StartZ=0 EndX=-100 EndY=-5 EndZ=0
    g19: LineSegment [constr] StartX=-100 StartY=-43 StartZ=0 EndX=-100 EndY=-38 EndZ=0
    g20: LineSegment [constr] StartX=-100 StartY=-38 StartZ=0 EndX=-100 EndY=-36 EndZ=0
  constraints (58):
    c: Coincident(g0,g1)
    c: Coincident(g1,g2)
    c: Coincident(g2,g3)
    c: Coincident(g3,g0)
    c: Horizontal(g0)
    c: Horizontal(g2)
    c: Vertical(g1)
    c: Vertical(g3)
    c: DistanceX(g0,g0) = 26
    c: DistanceY(g3,g3) = 31
    c: Coincident(g4,g5)
    c: Coincident(g5,g6)
    c: Coincident(g6,g7)
    c: Coincident(g7,g4)
    c: Horizontal(g4)
    c: Horizontal(g6)
    c: Vertical(g5)
    c: Vertical(g7)
    c: Equal(g0,g4) = 26
    c: Equal(g3,g7) = 31
    c: Coincident(g4,g8)
    c: Coincident(g8,g0)
    c: Horizontal(g8)
    c: DistanceX(g8,g8) = 2
    c: Horizontal(g9)
    c: Horizontal(g11)
    c: Vertical(g10)
    c: Vertical(g12)
    c: Tangent(g12,g13) = 1.5708
    c: Tangent(g9,g13) = 1.5708
    c: Tangent(g9,g14) = 1.5708
    c: Tangent(g10,g14) = 1.5708
    c: Tangent(g10,g15) = 1.5708
    c: Tangent(g11,g15) = 1.5708
    c: Tangent(g11,g16) = 1.5708
    c: Tangent(g12,g16) = 1.5708
    c: Equal(g13,g16)
    c: Equal(g16,g15)
    c: Equal(g15,g14)
    c: Radius(g14) = 2
    c: Coincident(g1,g13)
    c: Coincident(g4,g15)
    c: Coincident(g17,g-8)
    c: PointOnObject(g17,g1)
    c: Horizontal(g17)
    c: Coincident(g18,g-10)
    c: PointOnObject(g18,g2)
    c: Vertical(g18)
    c: DistanceY(g18,g18) = 5
    c: DistanceX(g17,g17) = 5
    c: Coincident(g19,g-6)
    c: Vertical(g19)
    c: Coincident(g20,g19)
    c: Vertical(g20)
    c: PointOnObject(g20,g0)
    c: DistanceY(g19,g19) = 5
    c: DistanceY(g9,g-10) = 3
    c: PointOnObject(g19,g11)
FEATURE [PartDesign::Pocket] Pocket013  label="TopOut_Connectors_Pocket"
  BaseFeature = -> Pocket006
  Length = 5
  Length2 = 100
  Placement = pos=(0,83,0) rot=(1,0,0;1.5708rad)
  Profile = -> Sketch030
  Type = 1
FEATURE [Sketcher::SketchObject] Sketch031  label="TopIn_Connectors_Sketch"
  ExternalGeometry = -> [Pocket007]
  MapMode = 5
  Placement = pos=(0,79,0) rot=(-1,0,0;1.5708rad)
  Support = -> [Pocket007]
  expr: Constraints[12] = 24 / 2
  expr: Constraints[11] = 3.2000000000000002 / 2
  sketch-geometry (25):
    g0: LineSegment [constr] StartX=-120 StartY=-5 StartZ=0 EndX=-94 EndY=-5 EndZ=0
    g1: LineSegment [constr] StartX=-94 StartY=-5 StartZ=0 EndX=-94 EndY=-36 EndZ=0
    g2: LineSegment [constr] StartX=-94 StartY=-36 StartZ=0 EndX=-120 EndY=-36 EndZ=0
    g3: LineSegment [constr] StartX=-120 StartY=-36 StartZ=0 EndX=-120 EndY=-5 EndZ=0
    g4: Circle CenterX=-107 CenterY=-20.5 CenterZ=0 NormalX=0 NormalY=0 NormalZ=1 AngleXU=0 Radius=12
    g5: Circle CenterX=-116.5 CenterY=-8.5 CenterZ=0 NormalX=0 NormalY=0 NormalZ=1 AngleXU=0 Radius=1.6
    g6: Circle CenterX=-97.5 CenterY=-32.5 CenterZ=0 NormalX=0 NormalY=0 NormalZ=1 AngleXU=0 Radius=1.6
    g7: LineSegment [constr] StartX=-97.5 StartY=-8.5 StartZ=0 EndX=-116.5 EndY=-8.5 EndZ=0
    g8: LineSegment [constr] StartX=-116.5 StartY=-8.5 StartZ=0 EndX=-116.5 EndY=-32.5 EndZ=0
    g9: LineSegment [constr] StartX=-116.5 StartY=-32.5 StartZ=0 EndX=-97.5 EndY=-32.5 EndZ=0
    g10: LineSegment [constr] StartX=-97.5 StartY=-32.5 StartZ=0 EndX=-97.5 EndY=-8.5 EndZ=0
    g11: Circle CenterX=-88.5 CenterY=-8.5 CenterZ=0 NormalX=0 NormalY=0 NormalZ=1 AngleXU=0 Radius=1.6
    g12: LineSegment [constr] StartX=-92 StartY=-5 StartZ=0 EndX=-66 EndY=-5 EndZ=0
    g13: LineSegment [constr] StartX=-66 StartY=-5 StartZ=0 EndX=-66 EndY=-36 EndZ=0
    g14: LineSegment [constr] StartX=-66 StartY=-36 StartZ=0 EndX=-92 EndY=-36 EndZ=0
    g15: LineSegment [constr] StartX=-92 StartY=-36 StartZ=0 EndX=-92 EndY=-5 EndZ=0
    g16: Circle CenterX=-79 CenterY=-20.5 CenterZ=0 NormalX=0 NormalY=0 NormalZ=1 AngleXU=0 Radius=12
    g17: Circle CenterX=-69.5 CenterY=-32.5 CenterZ=0 NormalX=0 NormalY=0 NormalZ=1 AngleXU=0 Radius=1.6
    g18: LineSegment [constr] StartX=-69.5 StartY=-8.5 StartZ=0 EndX=-88.5 EndY=-8.5 EndZ=0
    g19: LineSegment [constr] StartX=-88.5 StartY=-8.5 StartZ=0 EndX=-88.5 EndY=-32.5 EndZ=0
    g20: LineSegment [constr] StartX=-88.5 StartY=-32.5 StartZ=0 EndX=-69.5 EndY=-32.5 EndZ=0
    g21: LineSegment [constr] StartX=-69.5 StartY=-32.5 StartZ=0 EndX=-69.5 EndY=-8.5 EndZ=0
    g22: LineSegment [constr] StartX=-94 StartY=-36 StartZ=0 EndX=-92 EndY=-36 EndZ=0
    g23: LineSegment [constr] StartX=-94 StartY=-36 StartZ=0 EndX=-94 EndY=-40 EndZ=0
    g24: LineSegment [constr] StartX=-125 StartY=-15.5 StartZ=0 EndX=-120 EndY=-15.5 EndZ=0
  constraints (68):
    c: Coincident(g0,g1)
    c: Coincident(g1,g2)
    c: Coincident(g2,g3)
    c: Coincident(g3,g0)
    c: Horizontal(g0)
    c: Horizontal(g2)
    c: Vertical(g1)
    c: Vertical(g3)
    c: DistanceX(g0,g0) = 26
    c: DistanceY(g3,g3) = 31
    c: Equal(g6,g5)
    c: Radius(g5) = 1.6
    c: Radius(g4) = 12
    c: Symmetric(g0,g2,g4)
    c: Horizontal(g7)
    c: Tangent(g7,g4)
    c: Coincident(g8,g7)
    c: Vertical(g8)
    c: Horizontal(g9)
    c: Coincident(g10,g9)
    c: Vertical(g10)
    c: Tangent(g9,g4)
    c: Symmetric(g6,g5,g4)
    c: DistanceX(g9,g9) = 19
    c: Coincident(g9,g8)
    c: Coincident(g7,g10)
    c: Coincident(g5,g7)
    c: Coincident(g6,g9)
    c: Coincident(g12,g13)
    c: Coincident(g13,g14)
    c: Coincident(g14,g15)
    c: Coincident(g15,g12)
    c: Horizontal(g12)
    c: Horizontal(g14)
    c: Vertical(g13)
    c: Vertical(g15)
    c: Equal(g0,g12) = 26
    c: Equal(g3,g15) = 31
    c: Equal(g17,g11)
    c: Equal(g5,g11) = 1.6
    c: Equal(g4,g16) = 12
    c: Symmetric(g12,g14,g16)
    c: Horizontal(g18)
    c: Tangent(g18,g16)
    c: Coincident(g19,g18)
    c: Vertical(g19)
    c: Horizontal(g20)
    c: Coincident(g21,g20)
    c: Vertical(g21)
    c: Tangent(g20,g16)
    c: Symmetric(g17,g11,g16)
    c: Equal(g9,g20) = 19
    c: Coincident(g20,g19)
    c: Coincident(g18,g21)
    c: Coincident(g11,g18)
    c: Coincident(g17,g20)
    c: Horizontal(g22)
    c: Coincident(g1,g22)
    c: Coincident(g14,g22)
    c: DistanceX(g22,g22) = 2
    c: Coincident(g23,g1)
    c: PointOnObject(g23,g-6)
    c: Vertical(g23)
    c: Coincident(g24,g-4)
    c: Horizontal(g24)
    c: PointOnObject(g24,g3)
    c: DistanceX(g24,g24) = 5
    c: DistanceY(g23,g23) = 4
FEATURE [Sketcher::SketchObject] Sketch032  label="BreadBoard_Positions_Sketch"
  ExternalGeometry = -> [Sketch]
  MapMode = 5
  Support = -> [XY_Plane026]
  sketch-geometry (15):
    g0: LineSegment StartX=-43 StartY=-18 StartZ=0 EndX=122 EndY=-18 EndZ=0
    g1: LineSegment StartX=122 StartY=-18 StartZ=0 EndX=122 EndY=-72 EndZ=0
    g2: LineSegment StartX=122 StartY=-72 StartZ=0 EndX=-43 EndY=-72 EndZ=0
    g3: LineSegment StartX=-43 StartY=-72 StartZ=0 EndX=-43 EndY=-18 EndZ=0
    g4: LineSegment StartX=-43 StartY=72 StartZ=0 EndX=122 EndY=72 EndZ=0
    g5: LineSegment StartX=122 StartY=72 StartZ=0 EndX=122 EndY=27.5 EndZ=0
    g6: LineSegment StartX=122 StartY=27.5 StartZ=0 EndX=-43 EndY=27.5 EndZ=0
    g7: LineSegment StartX=-43 StartY=27.5 StartZ=0 EndX=-43 EndY=72 EndZ=0
    g8: LineSegment StartX=-43 StartY=27.5 StartZ=0 EndX=-43 EndY=-18 EndZ=0
    g9: LineSegment StartX=122 StartY=27.5 StartZ=0 EndX=122 EndY=-18 EndZ=0
    g10: LineSegment StartX=122 StartY=75 StartZ=0 EndX=122 EndY=72 EndZ=0
    g11: LineSegment StartX=125 StartY=72 StartZ=0 EndX=122 EndY=72 EndZ=0
    g12: LineSegment StartX=122 StartY=-72 StartZ=0 EndX=122 EndY=-75 EndZ=0
    g13: LineSegment StartX=-43 StartY=18 StartZ=0 EndX=122 EndY=18 EndZ=0
    g14: LineSegment StartX=-43 StartY=-27.5 StartZ=0 EndX=122 EndY=-27.5 EndZ=0
  constraints (46):
    c: Coincident(g0,g1)
    c: Coincident(g1,g2)
    c: Coincident(g2,g3)
    c: Coincident(g3,g0)
    c: Horizontal(g0)
    c: Horizontal(g2)
    c: Vertical(g1)
    c: Vertical(g3)
    c: DistanceY(g1,g1) = 54
    c: Coincident(g4,g5)
    c: Coincident(g5,g6)
    c: Coincident(g6,g7)
    c: Coincident(g7,g4)
    c: Horizontal(g4)
    c: Horizontal(g6)
    c: Vertical(g5)
    c: Vertical(g7)
    c: Coincident(g8,g6)
    c: Coincident(g8,g0)
    c: Vertical(g9)
    c: Vertical(g8)
    c: Coincident(g0,g9)
    c: DistanceY(g1,g4) = 144
    c: Coincident(g5,g9)
    c: DistanceX(g2,g2) = 165
    c: DistanceY(g1,g5) = 99.5
    c: PointOnObject(g10,g-4)
    c: Coincident(g10,g4)
    c: Vertical(g10)
    c: Coincident(g11,g4)
    c: PointOnObject(g11,g-5)
    c: Horizontal(g11)
    c: Equal(g10,g11)
    c: PointOnObject(g12,g-3)
    c: Vertical(g12)
    c: Coincident(g12,g1)
    c: Equal(g12,g10)
    c: DistanceY(g10,g10) = 3
    c: PointOnObject(g13,g8)
    c: PointOnObject(g13,g9)
    c: Horizontal(g13)
    c: DistanceY(g13,g4) = 54
    c: PointOnObject(g14,g1)
    c: Horizontal(g14)
    c: PointOnObject(g14,g3)
    c: DistanceY(g14,g4) = 99.5
FEATURE [PartDesign::Pocket] Pocket014  label="TopIn_Connectors_Pocket"
  BaseFeature = -> Pocket007
  Length = 5
  Length2 = 100
  Placement = pos=(0,79,0) rot=(1,0,0;1.5708rad)
  Profile = -> Sketch031
  Type = 1
FEATURE [Sketcher::SketchObject] Sketch033  label="BreadBoard_Clamps_Sketch"
  ExternalGeometry = -> [Sketch032,Sketch]
  MapMode = 5
  Support = -> [XY_Plane026]
  sketch-geometry (18):
    g0: Circle CenterX=39.5 CenterY=48.5 CenterZ=0 NormalX=0 NormalY=0 NormalZ=1 AngleXU=0 Radius=1.6
    g1: LineSegment [constr] StartX=39.5 StartY=48.5 StartZ=0 EndX=39.5 EndY=27.5 EndZ=0
    g2: Circle CenterX=39.5 CenterY=3 CenterZ=0 NormalX=0 NormalY=0 NormalZ=1 AngleXU=0 Radius=1.6
    g3: LineSegment [constr] StartX=39.5 StartY=3 StartZ=0 EndX=39.5 EndY=-18 EndZ=0
    g4: Circle CenterX=39.5 CenterY=-48.5 CenterZ=0 NormalX=0 NormalY=0 NormalZ=1 AngleXU=0 Radius=1.6
    g5: LineSegment [constr] StartX=39.5 StartY=-48.5 StartZ=0 EndX=39.5 EndY=-27.5 EndZ=0
    g6: Circle CenterX=39.5 CenterY=-3 CenterZ=0 NormalX=0 NormalY=0 NormalZ=1 AngleXU=0 Radius=1.6
    g7: LineSegment [constr] StartX=39.5 StartY=-3 StartZ=0 EndX=39.5 EndY=18 EndZ=0
    g8: Circle CenterX=-64 CenterY=45 CenterZ=0 NormalX=0 NormalY=0 NormalZ=1 AngleXU=0 Radius=1.6
    g9: LineSegment [constr] StartX=-64 StartY=45 StartZ=0 EndX=-43 EndY=45 EndZ=0
    g10: Circle CenterX=-64 CenterY=0 CenterZ=0 NormalX=0 NormalY=0 NormalZ=1 AngleXU=0 Radius=1.6
    g11: LineSegment [constr] StartX=-64 StartY=0 StartZ=0 EndX=-43 EndY=0 EndZ=0
    g12: Circle CenterX=-64 CenterY=-45 CenterZ=0 NormalX=0 NormalY=0 NormalZ=1 AngleXU=0 Radius=1.6
    g13: LineSegment [constr] StartX=-64 StartY=-45 StartZ=0 EndX=-43 EndY=-45 EndZ=0
    g14: LineSegment [constr] StartX=-64 StartY=45 StartZ=0 EndX=-64 EndY=0 EndZ=0
    g15: LineSegment [constr] StartX=-64 StartY=0 StartZ=0 EndX=-64 EndY=-45 EndZ=0
    g16: Circle CenterX=-110 CenterY=-60 CenterZ=0 NormalX=0 NormalY=0 NormalZ=1 AngleXU=0 Radius=1.6
    g17: LineSegment [constr] StartX=-110 StartY=-60 StartZ=0 EndX=-90 EndY=-60 EndZ=0
  constraints (49):
    c: Coincident(g1,g0)
    c: Vertical(g1)
    c: Symmetric(g-3,g-3,g1)
    c: Coincident(g3,g2)
    c: Vertical(g3)
    c: Symmetric(g-4,g-4,g3)
    c: Coincident(g7,g6)
    c: Vertical(g7)
    c: Coincident(g5,g4)
    c: Vertical(g5)
    c: Symmetric(g-9,g-9,g7)
    c: Symmetric(g-8,g-8,g5)
    c: Equal(g4,g2)
    c: Equal(g2,g6)
    c: Equal(g6,g0)
    c: Radius(g0) = 1.6
    c: Equal(g7,g1)
    c: Equal(g1,g3)
    c: Equal(g3,g5)
    c: DistanceY(g1,g1) = 21
    c: Coincident(g9,g8)
    c: Equal(g0,g8) = 1.6
    c: Equal(g1,g9) = 25
    c: Horizontal(g9)
    c: PointOnObject(g9,g-7)
    c: Coincident(g11,g10)
    c: Horizontal(g11)
    c: PointOnObject(g11,g-6)
    c: Coincident(g13,g12)
    c: Horizontal(g13)
    c: PointOnObject(g13,g-5)
    c: PointOnObject(g10,g-1)
    c: Vertical(g14)
    c: Vertical(g15)
    c: Coincident(g14,g15)
    c: Coincident(g14,g10)
    c: Coincident(g8,g14)
    c: Coincident(g15,g12)
    c: Symmetric(g-5,g-5,g13)
    c: DistanceY(g15,g15) = 45
    c: Equal(g12,g10)
    c: Equal(g10,g8)
    c: Equal(g14,g15)
    c: Equal(g16,g0)
    c: DistanceX(g-11,g16) = 15
    c: DistanceY(g-11,g16) = 15
    c: Coincident(g17,g16)
    c: Horizontal(g17)
    c: DistanceX(g17,g17) = 20
FEATURE [PartDesign::ShapeBinder] ShapeBinder034
  Support = -> [Sketch033]
FEATURE [Sketcher::SketchObject] Sketch034  label="BaseOut_BBMounting_Sketch"
  ExternalGeometry = -> [ShapeBinder034]
  MapMode = 5
  Placement = pos=(0,0,-4) rot=(0,0,1;3.14159rad)
  Support = -> [Mirrored001]
  sketch-geometry (34):
    g0: Circle CenterX=-39.5 CenterY=48.5 CenterZ=0 NormalX=0 NormalY=0 NormalZ=1 AngleXU=0 Radius=1.6
    g1: Circle CenterX=64 CenterY=45 CenterZ=0 NormalX=0 NormalY=0 NormalZ=1 AngleXU=0 Radius=1.6
    g2: Circle CenterX=64 CenterY=0 CenterZ=0 NormalX=0 NormalY=0 NormalZ=1 AngleXU=0 Radius=1.6
    g3: Circle CenterX=-39.5 CenterY=3 CenterZ=0 NormalX=0 NormalY=0 NormalZ=1 AngleXU=0 Radius=1.6
    g4: Circle CenterX=-39.5 CenterY=-3 CenterZ=0 NormalX=0 NormalY=0 NormalZ=1 AngleXU=0 Radius=1.6
    g5: Circle CenterX=-39.5 CenterY=-48.5 CenterZ=0 NormalX=0 NormalY=0 NormalZ=1 AngleXU=0 Radius=1.6
    g6: Circle CenterX=64 CenterY=-45 CenterZ=0 NormalX=0 NormalY=0 NormalZ=1 AngleXU=0 Radius=1.6
    g7: Circle CenterX=110 CenterY=60 CenterZ=0 NormalX=0 NormalY=0 NormalZ=1 AngleXU=0 Radius=1.6
    g8: Circle CenterX=90 CenterY=60 CenterZ=0 NormalX=0 NormalY=0 NormalZ=1 AngleXU=0 Radius=1.6
    g9: LineSegment [constr] StartX=90 StartY=60 StartZ=0 EndX=110 EndY=60 EndZ=0
    g10: Circle CenterX=110 CenterY=40 CenterZ=0 NormalX=0 NormalY=0 NormalZ=1 AngleXU=0 Radius=1.6
    g11: Circle CenterX=90 CenterY=40 CenterZ=0 NormalX=0 NormalY=0 NormalZ=1 AngleXU=0 Radius=1.6
    g12: LineSegment [constr] StartX=90 StartY=40 StartZ=0 EndX=110 EndY=40 EndZ=0
    g13: LineSegment [constr] StartX=110 StartY=60 StartZ=0 EndX=110 EndY=40 EndZ=0
    g14: Circle CenterX=110 CenterY=20 CenterZ=0 NormalX=0 NormalY=0 NormalZ=1 AngleXU=0 Radius=1.6
    g15: Circle CenterX=90 CenterY=20 CenterZ=0 NormalX=0 NormalY=0 NormalZ=1 AngleXU=0 Radius=1.6
    g16: LineSegment [constr] StartX=90 StartY=20 StartZ=0 EndX=110 EndY=20 EndZ=0
    g17: LineSegment [constr] StartX=110 StartY=40 StartZ=0 EndX=110 EndY=20 EndZ=0
    g18: Circle CenterX=110 CenterY=0 CenterZ=0 NormalX=0 NormalY=0 NormalZ=1 AngleXU=0 Radius=1.6
    g19: Circle CenterX=90 CenterY=0 CenterZ=0 NormalX=0 NormalY=0 NormalZ=1 AngleXU=0 Radius=1.6
    g20: LineSegment [constr] StartX=90 StartY=0 StartZ=0 EndX=110 EndY=0 EndZ=0
    g21: LineSegment [constr] StartX=110 StartY=20 StartZ=0 EndX=110 EndY=0 EndZ=0
    g22: Circle CenterX=110 CenterY=-20 CenterZ=0 NormalX=0 NormalY=0 NormalZ=1 AngleXU=0 Radius=1.6
    g23: Circle CenterX=90 CenterY=-20 CenterZ=0 NormalX=0 NormalY=0 NormalZ=1 AngleXU=0 Radius=1.6
    g24: LineSegment [constr] StartX=90 StartY=-20 StartZ=0 EndX=110 EndY=-20 EndZ=0
    g25: LineSegment [constr] StartX=110 StartY=0 StartZ=0 EndX=110 EndY=-20 EndZ=0
    g26: Circle CenterX=110 CenterY=-40 CenterZ=0 NormalX=0 NormalY=0 NormalZ=1 AngleXU=0 Radius=1.6
    g27: Circle CenterX=90 CenterY=-40 CenterZ=0 NormalX=0 NormalY=0 NormalZ=1 AngleXU=0 Radius=1.6
    g28: LineSegment [constr] StartX=90 StartY=-40 StartZ=0 EndX=110 EndY=-40 EndZ=0
    g29: LineSegment [constr] StartX=110 StartY=-20 StartZ=0 EndX=110 EndY=-40 EndZ=0
    g30: Circle CenterX=110 CenterY=-60 CenterZ=0 NormalX=0 NormalY=0 NormalZ=1 AngleXU=0 Radius=1.6
    g31: Circle CenterX=90 CenterY=-60 CenterZ=0 NormalX=0 NormalY=0 NormalZ=1 AngleXU=0 Radius=1.6
    g32: LineSegment [constr] StartX=90 StartY=-60 StartZ=0 EndX=110 EndY=-60 EndZ=0
    g33: LineSegment [constr] StartX=110 StartY=-40 StartZ=0 EndX=110 EndY=-60 EndZ=0
  constraints (81):
    c: Coincident(g0,g-3)
    c: Coincident(g1,g-4)
    c: Coincident(g6,g-8)
    c: Equal(g1,g-4)
    c: Equal(g-3,g0)
    c: Coincident(g-5,g3)
    c: Equal(g-5,g3)
    c: Coincident(g4,g-6)
    c: Equal(g4,g-6)
    c: Coincident(g5,g-9)
    c: Equal(g-9,g5)
    c: Equal(g-8,g6)
    c: Equal(g2,g-7)
    c: Coincident(g2,g-7)
    c: Coincident(g7,g-10)
    c: Equal(g8,g7)
    c: Equal(g-10,g7)
    c: Horizontal(g9)
    c: Coincident(g7,g9)
    c: Coincident(g8,g9)
    c: DistanceX(g9,g9) = 20
    c: Equal(g11,g10)
    c: Horizontal(g12)
    c: Coincident(g10,g12)
    c: Coincident(g11,g12)
    c: Equal(g9,g12) = 20
    c: Coincident(g7,g13)
    c: Coincident(g10,g13)
    c: Distance(g13) = 20
    c: Angle(g13) = -1.5708
    c: Equal(g15,g14)
    c: Horizontal(g16)
    c: Coincident(g14,g16)
    c: Coincident(g15,g16)
    c: Equal(g9,g16) = 20
    c: Coincident(g10,g17)
    c: Coincident(g14,g17)
    c: Equal(g13,g17)
    c: Parallel(g17,g13)
    c: Equal(g19,g18)
    c: Horizontal(g20)
    c: Coincident(g18,g20)
    c: Coincident(g19,g20)
    c: Equal(g9,g20) = 20
    c: Coincident(g14,g21)
    c: Coincident(g18,g21)
    c: Equal(g13,g21)
    c: Parallel(g21,g13)
    c: Equal(g23,g22)
    c: Horizontal(g24)
    c: Coincident(g22,g24)
    c: Coincident(g23,g24)
    c: Equal(g9,g24) = 20
    c: Coincident(g18,g25)
    c: Coincident(g22,g25)
    c: Equal(g13,g25)
    c: Parallel(g25,g13)
    c: Equal(g27,g26)
    c: Horizontal(g28)
    c: Coincident(g26,g28)
    c: Coincident(g27,g28)
    c: Equal(g9,g28) = 20
    c: Coincident(g22,g29)
    c: Coincident(g26,g29)
    c: Equal(g13,g29)
    c: Parallel(g29,g13)
    c: Equal(g31,g30)
    c: Horizontal(g32)
    c: Coincident(g30,g32)
    c: Coincident(g31,g32)
    c: Equal(g9,g32) = 20
    c: Coincident(g26,g33)
    c: Coincident(g30,g33)
    c: Equal(g13,g33)
    c: Parallel(g33,g13)
    c: Equal(g11,g8)
    c: Equal(g8,g15)
    c: Equal(g15,g19)
    c: Equal(g19,g23)
    c: Equal(g23,g27)
    c: Equal(g27,g31)
FEATURE [PartDesign::Hole] Hole  label="BaseOut_BBMounting_Hole"
  BaseFeature = -> Mirrored001
  Depth = 25
  DepthType = 1
  Diameter = 6.6
  DrillPoint = 1
  DrillPointAngle = 118
  HoleCutCountersinkAngle = 90
  HoleCutDepth = 0
  HoleCutDiameter = 6
  HoleCutType = 0
  ModelActualThread = false
  Placement = pos=(0,0,-4) rot=(0,0,1;3.14159rad)
  Profile = -> Sketch034
  Tapered = false
  TaperedAngle = 90
  ThreadAngle = 0
  ThreadClass = 0
  ThreadCutOffInner = 0
  ThreadCutOffOuter = 0
  ThreadDirection = 0
  ThreadFit = 0
  ThreadPitch = 0
  ThreadSize = 7
  ThreadType = 1
  Threaded = false
FEATURE [PartDesign::Body] Body008  label="BaseOut_Body"
  Group = -> [DatumPlane,ShapeBinder,Sketch002,Pad001,Sketch015,Pocket,Mirrored,Mirrored001,ShapeBinder034,Sketch034,Hole]
  Origin = -> Origin017
  Tip = -> Hole
FEATURE [PartDesign::ShapeBinder] ShapeBinder035
  Support = -> [Sketch033]
FEATURE [Sketcher::SketchObject] Sketch035  label="BaseIn_BBMounting_Sketch"
  ExternalGeometry = -> [ShapeBinder035]
  MapMode = 5
  Support = -> [MultiTransform]
  sketch-geometry (34):
    g0: Circle CenterX=-64 CenterY=45 CenterZ=0 NormalX=0 NormalY=0 NormalZ=1 AngleXU=0 Radius=1.6
    g1: Circle CenterX=39.5 CenterY=48.5 CenterZ=0 NormalX=0 NormalY=0 NormalZ=1 AngleXU=0 Radius=1.6
    g2: Circle CenterX=39.5 CenterY=3 CenterZ=0 NormalX=0 NormalY=0 NormalZ=1 AngleXU=0 Radius=1.6
    g3: Circle CenterX=39.5 CenterY=-3 CenterZ=0 NormalX=0 NormalY=0 NormalZ=1 AngleXU=0 Radius=1.6
    g4: Circle CenterX=39.5 CenterY=-48.5 CenterZ=0 NormalX=0 NormalY=0 NormalZ=1 AngleXU=0 Radius=1.6
    g5: Circle CenterX=-64 CenterY=-45 CenterZ=0 NormalX=0 NormalY=0 NormalZ=1 AngleXU=0 Radius=1.6
    g6: Circle CenterX=-64 CenterY=0 CenterZ=0 NormalX=0 NormalY=0 NormalZ=1 AngleXU=0 Radius=1.6
    g7: Circle CenterX=-110 CenterY=-60 CenterZ=0 NormalX=0 NormalY=0 NormalZ=1 AngleXU=0 Radius=1.6
    g8: Circle CenterX=-90 CenterY=-60 CenterZ=0 NormalX=0 NormalY=0 NormalZ=1 AngleXU=0 Radius=1.6
    g9: LineSegment [constr] StartX=-110 StartY=-60 StartZ=0 EndX=-90 EndY=-60 EndZ=0
    g10: Circle CenterX=-110 CenterY=-40 CenterZ=0 NormalX=0 NormalY=0 NormalZ=1 AngleXU=0 Radius=1.6
    g11: Circle CenterX=-90 CenterY=-40 CenterZ=0 NormalX=0 NormalY=0 NormalZ=1 AngleXU=0 Radius=1.6
    g12: LineSegment [constr] StartX=-110 StartY=-40 StartZ=0 EndX=-90 EndY=-40 EndZ=0
    g13: LineSegment [constr] StartX=-110 StartY=-60 StartZ=0 EndX=-110 EndY=-40 EndZ=0
    g14: Circle CenterX=-110 CenterY=-20 CenterZ=0 NormalX=0 NormalY=0 NormalZ=1 AngleXU=0 Radius=1.6
    g15: Circle CenterX=-90 CenterY=-20 CenterZ=0 NormalX=0 NormalY=0 NormalZ=1 AngleXU=0 Radius=1.6
    g16: LineSegment [constr] StartX=-110 StartY=-20 StartZ=0 EndX=-90 EndY=-20 EndZ=0
    g17: LineSegment [constr] StartX=-110 StartY=-40 StartZ=0 EndX=-110 EndY=-20 EndZ=0
    g18: Circle CenterX=-110 CenterY=0 CenterZ=0 NormalX=0 NormalY=0 NormalZ=1 AngleXU=0 Radius=1.6
    g19: Circle CenterX=-90 CenterY=0 CenterZ=0 NormalX=0 NormalY=0 NormalZ=1 AngleXU=0 Radius=1.6
    g20: LineSegment [constr] StartX=-110 StartY=0 StartZ=0 EndX=-90 EndY=0 EndZ=0
    g21: LineSegment [constr] StartX=-110 StartY=-20 StartZ=0 EndX=-110 EndY=0 EndZ=0
    g22: Circle CenterX=-110 CenterY=20 CenterZ=0 NormalX=0 NormalY=0 NormalZ=1 AngleXU=0 Radius=1.6
    g23: Circle CenterX=-90 CenterY=20 CenterZ=0 NormalX=0 NormalY=0 NormalZ=1 AngleXU=0 Radius=1.6
    g24: LineSegment [constr] StartX=-110 StartY=20 StartZ=0 EndX=-90 EndY=20 EndZ=0
    g25: LineSegment [constr] StartX=-110 StartY=0 StartZ=0 EndX=-110 EndY=20 EndZ=0
    g26: Circle CenterX=-110 CenterY=40 CenterZ=0 NormalX=0 NormalY=0 NormalZ=1 AngleXU=0 Radius=1.6
    g27: Circle CenterX=-90 CenterY=40 CenterZ=0 NormalX=0 NormalY=0 NormalZ=1 AngleXU=0 Radius=1.6
    g28: LineSegment [constr] StartX=-110 StartY=40 StartZ=0 EndX=-90 EndY=40 EndZ=0
    g29: LineSegment [constr] StartX=-110 StartY=20 StartZ=0 EndX=-110 EndY=40 EndZ=0
    g30: Circle CenterX=-110 CenterY=60 CenterZ=0 NormalX=0 NormalY=0 NormalZ=1 AngleXU=0 Radius=1.6
    g31: Circle CenterX=-90 CenterY=60 CenterZ=0 NormalX=0 NormalY=0 NormalZ=1 AngleXU=0 Radius=1.6
    g32: LineSegment [constr] StartX=-110 StartY=60 StartZ=0 EndX=-90 EndY=60 EndZ=0
    g33: LineSegment [constr] StartX=-110 StartY=40 StartZ=0 EndX=-110 EndY=60 EndZ=0
  constraints (81):
    c: Coincident(g0,g-3)
    c: Coincident(g1,g-4)
    c: Coincident(g2,g-5)
    c: Coincident(g3,g-9)
    c: Coincident(g4,g-8)
    c: Coincident(g6,g-6)
    c: Equal(g6,g-6)
    c: Equal(g0,g-3)
    c: Equal(g5,g-7)
    c: Equal(g1,g-4)
    c: Equal(g2,g-5)
    c: Equal(g3,g-9)
    c: Equal(g4,g-8)
    c: Coincident(g5,g-7)
    c: Coincident(g-10,g7)
    c: Equal(g7,g-10)
    c: Equal(g7,g8)
    c: Horizontal(g9)
    c: Coincident(g8,g9)
    c: Coincident(g9,g7)
    c: DistanceX(g9,g9) = 20
    c: Equal(g10,g11)
    c: Horizontal(g12)
    c: Coincident(g11,g12)
    c: Coincident(g12,g10)
    c: Equal(g9,g12) = 20
    c: Coincident(g7,g13)
    c: Coincident(g10,g13)
    c: Distance(g13) = 20
    c: Angle(g13) = 1.5708
    c: Equal(g14,g15)
    c: Horizontal(g16)
    c: Coincident(g15,g16)
    c: Coincident(g16,g14)
    c: Equal(g9,g16) = 20
    c: Coincident(g10,g17)
    c: Coincident(g14,g17)
    c: Equal(g13,g17)
    c: Parallel(g17,g13)
    c: Equal(g18,g19)
    c: Horizontal(g20)
    c: Coincident(g19,g20)
    c: Coincident(g20,g18)
    c: Equal(g9,g20) = 20
    c: Coincident(g14,g21)
    c: Coincident(g18,g21)
    c: Equal(g13,g21)
    c: Parallel(g21,g13)
    c: Equal(g22,g23)
    c: Horizontal(g24)
    c: Coincident(g23,g24)
    c: Coincident(g24,g22)
    c: Equal(g9,g24) = 20
    c: Coincident(g18,g25)
    c: Coincident(g22,g25)
    c: Equal(g13,g25)
    c: Parallel(g25,g13)
    c: Equal(g26,g27)
    c: Horizontal(g28)
    c: Coincident(g27,g28)
    c: Coincident(g28,g26)
    c: Equal(g9,g28) = 20
    c: Coincident(g22,g29)
    c: Coincident(g26,g29)
    c: Equal(g13,g29)
    c: Parallel(g29,g13)
    c: Equal(g30,g31)
    c: Horizontal(g32)
    c: Coincident(g31,g32)
    c: Coincident(g32,g30)
    c: Equal(g9,g32) = 20
    c: Coincident(g26,g33)
    c: Coincident(g30,g33)
    c: Equal(g13,g33)
    c: Parallel(g33,g13)
    c: Equal(g31,g27)
    c: Equal(g27,g23)
    c: Equal(g23,g19)
    c: Equal(g19,g15)
    c: Equal(g15,g11)
    c: Equal(g11,g8)
FEATURE [PartDesign::Hole] Hole001  label="BaseIn_BBMounting_Hole"
  BaseFeature = -> MultiTransform
  Depth = 25
  DepthType = 1
  Diameter = 3.3
  DrillPoint = 1
  DrillPointAngle = 118
  HoleCutCountersinkAngle = 90
  HoleCutDepth = 0
  HoleCutDiameter = 3
  HoleCutType = 0
  ModelActualThread = false
  Profile = -> Sketch035
  Tapered = false
  TaperedAngle = 90
  ThreadAngle = 0
  ThreadClass = 0
  ThreadCutOffInner = 0
  ThreadCutOffOuter = 0
  ThreadDirection = 0
  ThreadFit = 0
  ThreadPitch = 0
  ThreadSize = 3
  ThreadType = 1
  Threaded = false
FEATURE [PartDesign::Body] Body009  label="BaseIn_Body"
  Group = -> [Sketch001,Pad,ShapeBinder024,Sketch016,Pocket001,MultiTransform,Mirrored002,Mirrored003,ShapeBinder035,Sketch035,Hole001]
  Origin = -> Origin019
  Tip = -> Hole001
FEATURE [Sketcher::SketchObject] Sketch036  label="BreadBoard_ClampSide_Sketch"
  ExternalGeometry = -> [Sketch032]
  MapMode = 5
  Placement = pos=(0,0,0) rot=(1,0,0;1.5708rad)
  Support = -> [XZ_Plane026]
  sketch-geometry (2):
    g0: Circle CenterX=39.5 CenterY=27 CenterZ=0 NormalX=0 NormalY=0 NormalZ=1 AngleXU=0 Radius=3
    g1: LineSegment [constr] StartX=39.5 StartY=27 StartZ=0 EndX=39.5 EndY=7e-12 EndZ=0
  constraints (5):
    c: Vertical(g1)
    c: Symmetric(g-3,g-3,g1)
    c: Coincident(g1,g0)
    c: Radius(g0) = 3
    c: DistanceY(g1,g1) = 27
FEATURE [PartDesign::Body] Body012  label="Helper_Body"
  Group = -> [Sketch,Sketch003,Sketch004,Sketch019,Sketch020,Sketch032,Sketch033,Sketch036]
  Origin = -> Origin026
FEATURE [App::Part] Part013  label="Helper_Part"
  Group = -> [Body012]
  License = CC BY 3.0
  LicenseURL = http://creativecommons.org/licenses/by/3.0/
  Origin = -> Origin025
FEATURE [PartDesign::ShapeBinder] ShapeBinder036
  Placement = pos=(0,0,0) rot=(1,0,0;1.5708rad)
  Support = -> [Sketch036]
FEATURE [Sketcher::SketchObject] Sketch037  label="BottomOut_BBClamp_Sketch"
  ExternalGeometry = -> [ShapeBinder036]
  MapMode = 5
  Placement = pos=(0,-83,-4) rot=(0,-0.707107,0.707107;3.14159rad)
  Support = -> [Pocket004]
  sketch-geometry (1):
    g0: Circle CenterX=-39.5 CenterY=-31 CenterZ=0 NormalX=0 NormalY=0 NormalZ=1 AngleXU=0 Radius=3
  constraints (2):
    c: Coincident(g0,g-3)
    c: Equal(g-3,g0)
FEATURE [PartDesign::Hole] Hole002  label="BottomOut_BBClamp_Hole"
  BaseFeature = -> Pocket004
  Depth = 25
  DepthType = 0
  Diameter = 6.6
  DrillPoint = 1
  DrillPointAngle = 118
  HoleCutCountersinkAngle = 90
  HoleCutDepth = 0
  HoleCutDiameter = 6
  HoleCutType = 0
  ModelActualThread = false
  Placement = pos=(0,-83,-4) rot=(0,0.707107,0.707107;3.14159rad)
  Profile = -> Sketch037
  Tapered = false
  TaperedAngle = 90
  ThreadAngle = 0
  ThreadClass = 0
  ThreadCutOffInner = 0
  ThreadCutOffOuter = 0
  ThreadDirection = 0
  ThreadFit = 0
  ThreadPitch = 0
  ThreadSize = 7
  ThreadType = 1
  Threaded = false
FEATURE [PartDesign::Body] Body002  label="BottomOut_Body"
  Group = -> [DatumPlane007,ShapeBinder012,ShapeBinder013,Sketch011,Pad008,Sketch021,ShapeBinder026,Pocket004,ShapeBinder036,Sketch037,Hole002]
  Origin = -> Origin005
  Tip = -> Hole002
FEATURE [PartDesign::ShapeBinder] ShapeBinder037
  Placement = pos=(0,0,0) rot=(1,0,0;1.5708rad)
  Support = -> [Sketch036]
FEATURE [Sketcher::SketchObject] Sketch038  label="BottomIn_BBClamp_Sketch"
  ExternalGeometry = -> [ShapeBinder037]
  MapMode = 5
  Placement = pos=(0,-79,-4) rot=(0,-0.707107,0.707107;3.14159rad)
  Support = -> [Pocket005]
  sketch-geometry (1):
    g0: Circle CenterX=-39.5 CenterY=-31 CenterZ=0 NormalX=0 NormalY=0 NormalZ=1 AngleXU=0 Radius=3
  constraints (2):
    c: Coincident(g0,g-3)
    c: Equal(g0,g-3)
FEATURE [PartDesign::Hole] Hole003  label="BottomIn_BBClamp_Hole"
  BaseFeature = -> Pocket005
  Depth = 25
  DepthType = 0
  Diameter = 3.3
  DrillPoint = 1
  DrillPointAngle = 118
  HoleCutCountersinkAngle = 90
  HoleCutDepth = 0
  HoleCutDiameter = 3
  HoleCutType = 0
  ModelActualThread = false
  Placement = pos=(0,-79,-4) rot=(0,0.707107,0.707107;3.14159rad)
  Profile = -> Sketch038
  Tapered = false
  TaperedAngle = 90
  ThreadAngle = 0
  ThreadClass = 0
  ThreadCutOffInner = 0
  ThreadCutOffOuter = 0
  ThreadDirection = 0
  ThreadFit = 0
  ThreadPitch = 0
  ThreadSize = 3
  ThreadType = 1
  Threaded = false
FEATURE [PartDesign::Body] Body001  label="BottomIn_Body"
  Group = -> [DatumPlane008,ShapeBinder014,ShapeBinder015,Sketch012,Pad009,ShapeBinder027,Sketch022,Pocket005,ShapeBinder037,Sketch038,Hole003]
  Origin = -> Origin004
  Tip = -> Hole003
FEATURE [PartDesign::ShapeBinder] ShapeBinder038
  Placement = pos=(0,0,0) rot=(1,0,0;1.5708rad)
  Support = -> [Sketch036]
FEATURE [Sketcher::SketchObject] Sketch039  label="TopOut_BBClamp_Sketch"
  ExternalGeometry = -> [ShapeBinder038]
  MapMode = 5
  Placement = pos=(0,83,0) rot=(-1,0,0;1.5708rad)
  Support = -> [Pocket013]
  sketch-geometry (1):
    g0: Circle CenterX=39.5 CenterY=-27 CenterZ=0 NormalX=0 NormalY=0 NormalZ=1 AngleXU=0 Radius=3
  constraints (2):
    c: Coincident(g0,g-3)
    c: Equal(g0,g-3)
FEATURE [PartDesign::Hole] Hole004  label="TopOut_BBClamp_Hole"
  BaseFeature = -> Pocket013
  Depth = 25
  DepthType = 1
  Diameter = 6.6
  DrillPoint = 1
  DrillPointAngle = 118
  HoleCutCountersinkAngle = 90
  HoleCutDepth = 0
  HoleCutDiameter = 6
  HoleCutType = 0
  ModelActualThread = false
  Placement = pos=(0,83,0) rot=(1,0,0;1.5708rad)
  Profile = -> Sketch039
  Tapered = false
  TaperedAngle = 90
  ThreadAngle = 0
  ThreadClass = 0
  ThreadCutOffInner = 0
  ThreadCutOffOuter = 0
  ThreadDirection = 0
  ThreadFit = 0
  ThreadPitch = 0
  ThreadSize = 7
  ThreadType = 1
  Threaded = false
FEATURE [PartDesign::Body] Body006  label="TopOut_Body"
  Group = -> [DatumPlane001,ShapeBinder001,Sketch005,ShapeBinder002,Pad002,Sketch023,ShapeBinder028,Pocket006,Sketch030,Pocket013,ShapeBinder038,Sketch039,Hole004]
  Origin = -> Origin013
  Tip = -> Hole004
FEATURE [PartDesign::ShapeBinder] ShapeBinder039
  Placement = pos=(0,0,0) rot=(1,0,0;1.5708rad)
  Support = -> [Sketch036]
FEATURE [Sketcher::SketchObject] Sketch040  label="TopIn_BBClamp_Sketch"
  ExternalGeometry = -> [ShapeBinder039]
  MapMode = 5
  Placement = pos=(0,79,0) rot=(-1,0,0;1.5708rad)
  Support = -> [Pocket014]
  sketch-geometry (1):
    g0: Circle CenterX=39.5 CenterY=-27 CenterZ=0 NormalX=0 NormalY=0 NormalZ=1 AngleXU=0 Radius=3
  constraints (2):
    c: Coincident(g-3,g0)
    c: Equal(g0,g-3)
FEATURE [PartDesign::Hole] Hole005  label="TopIn_BBClamp_Hole"
  BaseFeature = -> Pocket014
  Depth = 25
  DepthType = 1
  Diameter = 3.3
  DrillPoint = 1
  DrillPointAngle = 118
  HoleCutCountersinkAngle = 90
  HoleCutDepth = 0
  HoleCutDiameter = 3
  HoleCutType = 0
  ModelActualThread = false
  Placement = pos=(0,79,0) rot=(1,0,0;1.5708rad)
  Profile = -> Sketch040
  Tapered = false
  TaperedAngle = 90
  ThreadAngle = 0
  ThreadClass = 0
  ThreadCutOffInner = 0
  ThreadCutOffOuter = 0
  ThreadDirection = 0
  ThreadFit = 0
  ThreadPitch = 0
  ThreadSize = 3
  ThreadType = 1
  Threaded = false
FEATURE [TechDraw::DrawSVGTemplate] Template001  label="BottomOut_Template"
  Height = 210
  Orientation = 1
  Width = 297
FEATURE [TechDraw::DrawViewPart] View001  label="BottomOut_View"
  CoarseView = false
  Direction = (0,1,0)
  Focus = 100
  HardHidden = false
  IsoCount = 0
  IsoHidden = false
  IsoVisible = false
  LockPosition = false
  Perspective = false
  Rotation = 0
  ScaleType = 0
  SeamHidden = false
  SeamVisible = false
  SmoothHidden = false
  SmoothVisible = false
  Source = -> [Hole002]
  X = 148.5
  Y = 105
FEATURE [TechDraw::DrawPage] Page001  label="BottomOut_Page"
  KeepUpdated = true
  ProjectionType = 0
  Template = -> Template001
  Views = -> [View001]
FEATURE [App::Part] Part  label="BottomOut_Part"
  Group = -> [Body002,Template001,Page001]
  License = CC BY 3.0
  LicenseURL = http://creativecommons.org/licenses/by/3.0/
  Origin = -> Origin
FEATURE [TechDraw::DrawSVGTemplate] Template002  label="BottomIn_Template"
  Height = 210
  Orientation = 1
  Width = 297
FEATURE [TechDraw::DrawViewPart] View002  label="BottomIn_View"
  CoarseView = false
  Direction = (0,1,0)
  Focus = 100
  HardHidden = false
  IsoCount = 0
  IsoHidden = false
  IsoVisible = false
  LockPosition = false
  Perspective = false
  Rotation = 0
  ScaleType = 0
  SeamHidden = false
  SeamVisible = false
  SmoothHidden = false
  SmoothVisible = false
  Source = -> [Hole003]
  X = 148.5
  Y = 105
FEATURE [TechDraw::DrawPage] Page002  label="BottomIn_Page"
  KeepUpdated = true
  ProjectionType = 0
  Template = -> Template002
  Views = -> [View002]
FEATURE [App::Part] Part001  label="BottomIn_Part"
  Group = -> [Body001,Template002,Page002]
  License = CC BY 3.0
  LicenseURL = http://creativecommons.org/licenses/by/3.0/
  Origin = -> Origin001
FEATURE [TechDraw::DrawSVGTemplate] Template003  label="RightOut_Template"
  Height = 210
  Orientation = 1
  Width = 297
FEATURE [TechDraw::DrawSVGTemplate] Template004  label="RightIn_Template"
  Height = 210
  Orientation = 1
  Width = 297
FEATURE [TechDraw::DrawSVGTemplate] Template005  label="LeftOut_Template"
  Height = 210
  Orientation = 1
  Width = 297
FEATURE [TechDraw::DrawSVGTemplate] Template006  label="LeftIn_Template"
  Height = 210
  Orientation = 1
  Width = 297
FEATURE [TechDraw::DrawViewPart] View003  label="RightOut_View"
  CoarseView = false
  Direction = (1,0,0)
  Focus = 100
  HardHidden = false
  IsoCount = 0
  IsoHidden = false
  IsoVisible = false
  LockPosition = false
  Perspective = false
  Rotation = 0
  ScaleType = 0
  SeamHidden = false
  SeamVisible = false
  SmoothHidden = false
  SmoothVisible = false
  Source = -> [Body]
  X = 148.5
  Y = 105
FEATURE [TechDraw::DrawPage] Page003  label="RightOut_Page"
  KeepUpdated = true
  ProjectionType = 0
  Template = -> Template003
  Views = -> [View003]
FEATURE [App::Part] Part002  label="RightOut_Part"
  Group = -> [Body,Template003,Page003]
  License = CC BY 3.0
  LicenseURL = http://creativecommons.org/licenses/by/3.0/
  Origin = -> Origin002
FEATURE [TechDraw::DrawViewPart] View004  label="RightIn_View"
  CoarseView = false
  Direction = (1,0,0)
  Focus = 100
  HardHidden = false
  IsoCount = 0
  IsoHidden = false
  IsoVisible = false
  LockPosition = false
  Perspective = false
  Rotation = 0
  ScaleType = 0
  SeamHidden = false
  SeamVisible = false
  SmoothHidden = false
  SmoothVisible = false
  Source = -> [Body003]
  X = 148.5
  Y = 105
FEATURE [TechDraw::DrawPage] Page004  label="RightIn_Page"
  KeepUpdated = true
  ProjectionType = 0
  Template = -> Template004
  Views = -> [View004]
FEATURE [App::Part] Part003  label="RightIn_Part"
  Group = -> [Body003,Template004,Page004]
  License = CC BY 3.0
  LicenseURL = http://creativecommons.org/licenses/by/3.0/
  Origin = -> Origin006
FEATURE [TechDraw::DrawViewPart] View005  label="LeftOut_View"
  CoarseView = false
  Direction = (1,0,0)
  Focus = 100
  HardHidden = false
  IsoCount = 0
  IsoHidden = false
  IsoVisible = false
  LockPosition = false
  Perspective = false
  Rotation = 0
  ScaleType = 0
  SeamHidden = false
  SeamVisible = false
  SmoothHidden = false
  SmoothVisible = false
  Source = -> [Body004]
  X = 148.5
  Y = 105
FEATURE [TechDraw::DrawPage] Page005  label="LeftOut_Page"
  KeepUpdated = true
  ProjectionType = 0
  Template = -> Template005
  Views = -> [View005]
FEATURE [App::Part] Part004  label="LeftOut_Part"
  Group = -> [Body004,Template005,Page005]
  License = CC BY 3.0
  LicenseURL = http://creativecommons.org/licenses/by/3.0/
  Origin = -> Origin008
FEATURE [TechDraw::DrawSVGTemplate] Template007  label="TopOut_Template"
  Height = 210
  Orientation = 1
  Width = 297
FEATURE [TechDraw::DrawSVGTemplate] Template008  label="TopIn_Template"
  Height = 210
  Orientation = 1
  Width = 297
FEATURE [TechDraw::DrawSVGTemplate] Template009  label="BaseOut_Template"
  Height = 210
  Orientation = 1
  Width = 297
FEATURE [TechDraw::DrawSVGTemplate] Template010  label="BaseIn_Template"
  Height = 210
  Orientation = 1
  Width = 297
FEATURE [TechDraw::DrawSVGTemplate] Template011  label="LidOut_Template"
  Height = 210
  Orientation = 1
  Width = 297
FEATURE [TechDraw::DrawSVGTemplate] Template012  label="LidSlide_Template"
  Height = 210
  Orientation = 1
  Width = 297
FEATURE [TechDraw::DrawViewPart] View007  label="TopOut_View"
  CoarseView = false
  Direction = (0,1,0)
  Focus = 100
  HardHidden = false
  IsoCount = 0
  IsoHidden = false
  IsoVisible = false
  LockPosition = false
  Perspective = false
  Rotation = 0
  ScaleType = 0
  SeamHidden = false
  SeamVisible = false
  SmoothHidden = false
  SmoothVisible = false
  Source = -> [Body006]
  X = 148.5
  Y = 105
FEATURE [TechDraw::DrawPage] Page007  label="TopOut_Page"
  KeepUpdated = true
  ProjectionType = 0
  Template = -> Template007
  Views = -> [View007]
FEATURE [App::Part] Part006  label="TopOut_Part"
  Group = -> [Body006,Template007,Page007]
  License = CC BY 3.0
  LicenseURL = http://creativecommons.org/licenses/by/3.0/
  Origin = -> Origin012
FEATURE [TechDraw::DrawViewPart] View009  label="BaseOut_View"
  CoarseView = false
  Direction = (0,0,1)
  Focus = 100
  HardHidden = false
  IsoCount = 0
  IsoHidden = false
  IsoVisible = false
  LockPosition = false
  Perspective = false
  Rotation = 0
  ScaleType = 0
  SeamHidden = false
  SeamVisible = false
  SmoothHidden = false
  SmoothVisible = false
  Source = -> [Body008]
  X = 148.5
  Y = 105
FEATURE [TechDraw::DrawPage] Page009  label="BaseOut_Page"
  KeepUpdated = true
  ProjectionType = 0
  Template = -> Template009
  Views = -> [View009]
FEATURE [App::Part] Part008  label="BaseOut_Part"
  Group = -> [Body008,Template009,Page009]
  License = CC BY 3.0
  LicenseURL = http://creativecommons.org/licenses/by/3.0/
  Origin = -> Origin016
FEATURE [TechDraw::DrawViewPart] View010  label="BaseIn_View"
  CoarseView = false
  Direction = (0,0,1)
  Focus = 100
  HardHidden = false
  IsoCount = 0
  IsoHidden = false
  IsoVisible = false
  LockPosition = false
  Perspective = false
  Rotation = 0
  ScaleType = 0
  SeamHidden = false
  SeamVisible = false
  SmoothHidden = false
  SmoothVisible = false
  Source = -> [Body009]
  X = 148.197
  Y = 104.395
FEATURE [TechDraw::DrawPage] Page010  label="BaseIn_Page"
  KeepUpdated = true
  ProjectionType = 0
  Template = -> Template010
  Views = -> [View010]
FEATURE [App::Part] Part009  label="BaseIn_Part"
  Group = -> [Body009,Template010,Page010]
  License = CC BY 3.0
  LicenseURL = http://creativecommons.org/licenses/by/3.0/
  Origin = -> Origin018
FEATURE [TechDraw::DrawViewPart] View011  label="LidOut_View"
  CoarseView = false
  Direction = (0,0,1)
  Focus = 100
  HardHidden = false
  IsoCount = 0
  IsoHidden = false
  IsoVisible = false
  LockPosition = false
  Perspective = false
  Rotation = 0
  ScaleType = 0
  SeamHidden = false
  SeamVisible = false
  SmoothHidden = false
  SmoothVisible = false
  Source = -> [Body013]
  X = 148.5
  Y = 105
FEATURE [TechDraw::DrawPage] Page011  label="LidOut_Page"
  KeepUpdated = true
  ProjectionType = 0
  Template = -> Template011
  Views = -> [View011]
FEATURE [PartDesign::ShapeBinder] ShapeBinder040
  Support = -> [Sketch032]
FEATURE [Sketcher::SketchObject] Sketch041  label="BreadBoard_Sketch"
  ExternalGeometry = -> [ShapeBinder040]
  MapMode = 5
  Support = -> [XY_Plane028]
  sketch-geometry (4):
    g0: LineSegment StartX=-43 StartY=18 StartZ=0 EndX=122 EndY=18 EndZ=0
    g1: LineSegment StartX=122 StartY=18 StartZ=0 EndX=122 EndY=-18 EndZ=0
    g2: LineSegment StartX=122 StartY=-18 StartZ=0 EndX=-43 EndY=-18 EndZ=0
    g3: LineSegment StartX=-43 StartY=-18 StartZ=0 EndX=-43 EndY=18 EndZ=0
  constraints (10):
    c: Coincident(g0,g1)
    c: Coincident(g1,g2)
    c: Coincident(g2,g3)
    c: Coincident(g3,g0)
    c: Horizontal(g0)
    c: Horizontal(g2)
    c: Vertical(g1)
    c: Vertical(g3)
    c: Coincident(g0,g-6)
    c: Coincident(g1,g-8)
FEATURE [PartDesign::Pad] Pad012  label="BreadBoard_Pad"
  Length = 10
  Length2 = 100
  Profile = -> Sketch041
  Type = 0
FEATURE [Sketcher::SketchObject] Sketch042  label="BreadBoard_Socket_Sketch"
  ExternalGeometry = -> [Pad012]
  MapMode = 5
  Placement = pos=(0,0,10) rot=(0,0,1;0rad)
  Support = -> [Pad012]
  expr: Constraints[22] = 2.54 * 4
  sketch-geometry (12):
    g0: Circle CenterX=-40.46 CenterY=15.24 CenterZ=0 NormalX=0 NormalY=0 NormalZ=1 AngleXU=0 Radius=0.5
    g1: LineSegment [constr] StartX=-40.46 StartY=15.24 StartZ=0 EndX=-40.46 EndY=12.7 EndZ=0
    g2: LineSegment [constr] StartX=-40.46 StartY=12.7 StartZ=0 EndX=-40.46 EndY=10.16 EndZ=0
    g3: LineSegment [constr] StartX=-40.46 StartY=10.16 StartZ=0 EndX=-40.46 EndY=7.62 EndZ=0
    g4: LineSegment [constr] StartX=-40.46 StartY=7.62 StartZ=0 EndX=-40.46 EndY=5.08 EndZ=0
    g5: Circle CenterX=-40.46 CenterY=-5.08 CenterZ=0 NormalX=0 NormalY=0 NormalZ=1 AngleXU=0 Radius=0.5
    g6: LineSegment [constr] StartX=-40.46 StartY=5.08 StartZ=0 EndX=-40.46 EndY=-5.08 EndZ=0
    g7: LineSegment [constr] StartX=-40.46 StartY=-5.08 StartZ=0 EndX=-40.46 EndY=-7.62 EndZ=0
    g8: LineSegment [constr] StartX=-40.46 StartY=-7.62 StartZ=0 EndX=-40.46 EndY=-10.16 EndZ=0
    g9: LineSegment [constr] StartX=-40.46 StartY=-10.16 StartZ=0 EndX=-40.46 EndY=-12.7 EndZ=0
    g10: LineSegment [constr] StartX=-40.46 StartY=-12.7 StartZ=0 EndX=-40.46 EndY=-15.24 EndZ=0
    g11: GeomPoint X=-40.46 Y=0 Z=0
  constraints (34):
    c: Radius(g0) = 0.5
    c: Coincident(g0,g1)
    c: Distance(g1) = 2.54
    c: Angle(g1) = -1.5708
    c: Equal(g1,g2)
    c: Parallel(g2,g1)
    c: Equal(g1,g3)
    c: Parallel(g3,g1)
    c: Equal(g1,g4)
    c: Parallel(g4,g1)
    c: Equal(g0,g5) = 1.27
    c: Coincident(g5,g6)
    c: Parallel(g6,g1)
    c: Coincident(g5,g7)
    c: Equal(g1,g7)
    c: Parallel(g7,g1)
    c: Equal(g1,g8)
    c: Parallel(g8,g1)
    c: Equal(g1,g9)
    c: Parallel(g9,g1)
    c: Equal(g1,g10)
    c: Parallel(g10,g1)
    c: DistanceY(g6,g6) = 10.16
    c: Symmetric(g6,g6,g11)
    c: PointOnObject(g11,g-1)
    c: DistanceX(g-5,g11) = 2.54
    c: DistanceY(g5,g0) = 20.32
    c: Coincident(g1,g2)
    c: Coincident(g2,g3)
    c: Coincident(g3,g4)
    c: Coincident(g4,g6)
    c: Coincident(g9,g10)
    c: Coincident(g8,g9)
    c: Coincident(g7,g8)
FEATURE [PartDesign::Pocket] Pocket015  label="BreadBoard_Socket_Pocket"
  BaseFeature = -> Pad012
  Length = 5
  Length2 = 100
  Profile = -> Sketch042
  Type = 0
FEATURE [Sketcher::SketchObject] Sketch043  label="BreadBoard_Socket2_Sketch"
  ExternalGeometry = -> [Pocket015]
  MapMode = 5
  Placement = pos=(0,0,10) rot=(0,0,1;0rad)
  Support = -> [Pocket015]
  sketch-geometry (8):
    g0: LineSegment StartX=-41.46 StartY=16.24 StartZ=0 EndX=-39.46 EndY=16.24 EndZ=0
    g1: LineSegment StartX=-39.46 StartY=16.24 StartZ=0 EndX=-39.46 EndY=14.24 EndZ=0
    g2: LineSegment StartX=-39.46 StartY=14.24 StartZ=0 EndX=-41.46 EndY=14.24 EndZ=0
    g3: LineSegment StartX=-41.46 StartY=14.24 StartZ=0 EndX=-41.46 EndY=16.24 EndZ=0
    g4: LineSegment StartX=-41.46 StartY=-4.08 StartZ=0 EndX=-39.46 EndY=-4.08 EndZ=0
    g5: LineSegment StartX=-41.46 StartY=-6.08 StartZ=0 EndX=-41.46 EndY=-4.08 EndZ=0
    g6: LineSegment StartX=-39.46 StartY=-6.08 StartZ=0 EndX=-41.46 EndY=-6.08 EndZ=0
    g7: LineSegment StartX=-39.46 StartY=-4.08 StartZ=0 EndX=-39.46 EndY=-6.08 EndZ=0
  constraints (22):
    c: Coincident(g0,g1)
    c: Coincident(g1,g2)
    c: Coincident(g2,g3)
    c: Coincident(g3,g0)
    c: Horizontal(g0)
    c: Horizontal(g2)
    c: Vertical(g1)
    c: Vertical(g3)
    c: Equal(g0,g3)
    c: Symmetric(g2,g0,g-3)
    c: DistanceX(g0,g0) = 2
    c: Coincident(g4,g7)
    c: Coincident(g7,g6)
    c: Coincident(g6,g5)
    c: Coincident(g5,g4)
    c: Horizontal(g4)
    c: Horizontal(g6)
    c: Vertical(g7)
    c: Vertical(g5)
    c: Equal(g4,g5)
    c: Equal(g0,g4) = 2
    c: Symmetric(g4,g5,g-4)
FEATURE [PartDesign::Pocket] Pocket016  label="BreadBoard_Socket2_Pocket"
  BaseFeature = -> Pocket015
  Length = 0.5
  Length2 = 100
  Profile = -> Sketch043
  Type = 0
FEATURE [PartDesign::LinearPattern] LinearPattern  label="BreadBoard_Socket_LinearPattern_Columns"
  Direction = -> Y_Axis028
  Length = 10.16
  Occurrences = 5
  Reversed = true
  expr: Length = 4 * 2.54
FEATURE [PartDesign::LinearPattern] LinearPattern001  label="BreadBoard_Socket_LinearPattern_Rows"
  Direction = -> Sketch043 [H_Axis]
  Length = 160.02
  Occurrences = 64
  expr: Length = 63 * 2.54
FEATURE [PartDesign::MultiTransform] MultiTransform001  label="BreadBoard_Socket_MultiTransform"
  BaseFeature = -> Pocket016
  Originals = -> [Pocket016,Pocket015]
  Transformations = -> [LinearPattern,LinearPattern001]
FEATURE [PartDesign::Body] Body014  label="BreadBoard_Body"
  Group = -> [ShapeBinder040,Sketch041,Pad012,Sketch042,Pocket015,Sketch043,Pocket016,MultiTransform001,LinearPattern,LinearPattern001]
  Origin = -> Origin028
  Tip = -> MultiTransform001
FEATURE [PartDesign::ShapeBinder] ShapeBinder041
  Support = -> [Sketch032]
FEATURE [Sketcher::SketchObject] Sketch044  label="BreadBoardPower_Sketch"
  ExternalGeometry = -> [ShapeBinder041]
  MapMode = 5
  Support = -> [XY_Plane030]
  sketch-geometry (6):
    g0: LineSegment StartX=-43 StartY=4.75 StartZ=0 EndX=122 EndY=4.75 EndZ=0
    g1: LineSegment StartX=122 StartY=4.75 StartZ=0 EndX=122 EndY=-4.75 EndZ=0
    g2: LineSegment StartX=122 StartY=-4.75 StartZ=0 EndX=-43 EndY=-4.75 EndZ=0
    g3: LineSegment StartX=-43 StartY=-4.75 StartZ=0 EndX=-43 EndY=4.75 EndZ=0
    g4: GeomPoint X=-43 Y=0 Z=0
    g5: LineSegment [constr] StartX=122 StartY=-18 StartZ=0 EndX=122 EndY=-27.5 EndZ=0
  constraints (17):
    c: Coincident(g0,g1)
    c: Coincident(g1,g2)
    c: Coincident(g2,g3)
    c: Coincident(g3,g0)
    c: Horizontal(g0)
    c: Horizontal(g2)
    c: Vertical(g1)
    c: Vertical(g3)
    c: PointOnObject(g0,g-6)
    c: PointOnObject(g0,g-5)
    c: Symmetric(g3,g3,g4)
    c: PointOnObject(g4,g-1)
    c: Coincident(g5,g-5)
    c: Vertical(g5)
    c: Equal(g5,g1)
    c: Coincident(g5,g-4)
    c: DistanceY(g1,g1) = 9.5
FEATURE [PartDesign::Pad] Pad013  label="BreadBoardPower_Pad"
  Length = 10
  Length2 = 100
  Profile = -> Sketch044
  Type = 0
FEATURE [Sketcher::SketchObject] Sketch045  label="BreadBoardPower_Socket_Sketch"
  ExternalGeometry = -> [Pad013]
  MapMode = 5
  Placement = pos=(0,0,10) rot=(0,0,1;0rad)
  Support = -> [Pad013]
  sketch-geometry (3):
    g0: LineSegment [constr] StartX=-38 StartY=1.27 StartZ=0 EndX=-38 EndY=-1.27 EndZ=0
    g1: Circle CenterX=-38 CenterY=1.27 CenterZ=0 NormalX=0 NormalY=0 NormalZ=1 AngleXU=0 Radius=0.5
    g2: GeomPoint X=-38 Y=0 Z=0
  constraints (7):
    c: Vertical(g0)
    c: Coincident(g1,g0)
    c: Symmetric(g0,g0,g2)
    c: PointOnObject(g2,g-1)
    c: DistanceY(g0,g0) = 2.54
    c: Radius(g1) = 0.5
    c: DistanceX(g-5,g2) = 5
FEATURE [PartDesign::Pocket] Pocket017  label="BreadBoardPower_Socket_Pocket"
  BaseFeature = -> Pad013
  Length = 5
  Length2 = 100
  Profile = -> Sketch045
  Type = 0
FEATURE [Sketcher::SketchObject] Sketch046  label="BreadBoardPower_Socket2_Sketch"
  ExternalGeometry = -> [Pocket017]
  MapMode = 5
  Placement = pos=(0,0,10) rot=(0,0,1;0rad)
  Support = -> [Pocket017]
  sketch-geometry (4):
    g0: LineSegment StartX=-39 StartY=2.27 StartZ=0 EndX=-37 EndY=2.27 EndZ=0
    g1: LineSegment StartX=-37 StartY=2.27 StartZ=0 EndX=-37 EndY=0.27 EndZ=0
    g2: LineSegment StartX=-37 StartY=0.27 StartZ=0 EndX=-39 EndY=0.27 EndZ=0
    g3: LineSegment StartX=-39 StartY=0.27 StartZ=0 EndX=-39 EndY=2.27 EndZ=0
  constraints (11):
    c: Coincident(g0,g1)
    c: Coincident(g1,g2)
    c: Coincident(g2,g3)
    c: Coincident(g3,g0)
    c: Horizontal(g0)
    c: Horizontal(g2)
    c: Vertical(g1)
    c: Vertical(g3)
    c: Equal(g0,g1)
    c: DistanceX(g0,g0) = 2
    c: Symmetric(g0,g2,g-3)
FEATURE [PartDesign::Pocket] Pocket018  label="BreadBoardPower_Socket2_Pocket"
  BaseFeature = -> Pocket017
  Length = 1
  Length2 = 100
  Profile = -> Sketch046
  Type = 0
FEATURE [PartDesign::LinearPattern] LinearPattern002  label="BBP_Socket2_LinearPattern005"
  Direction = -> Y_Axis030
  Length = 2.54
  Occurrences = 2
  Reversed = true
FEATURE [PartDesign::LinearPattern] LinearPattern003  label="BBP_Socket2_LinearPattern"
  Direction = -> Sketch046 [H_Axis]
  Length = 10.16
  Occurrences = 5
  expr: Length = 4 * 2.54
FEATURE [PartDesign::LinearPattern] LinearPattern004  label="BBP_Socket2_LinearPattern006"
  Direction = -> Sketch046 [H_Axis]
  Length = 145
  Occurrences = 10
FEATURE [PartDesign::MultiTransform] MultiTransform002  label="BBP_Socket2_MultiTransform"
  BaseFeature = -> Pocket018
  Originals = -> [Pocket018,Pocket017]
  Transformations = -> [LinearPattern002,LinearPattern003,LinearPattern004]
FEATURE [PartDesign::Body] Body015  label="BreadBoardPower_Body"
  Group = -> [ShapeBinder041,Sketch044,Pad013,Sketch045,Pocket017,Sketch046,Pocket018,MultiTransform002,LinearPattern002,LinearPattern003,LinearPattern004]
  Origin = -> Origin030
  Placement = pos=(0,-22.8,0) rot=(0,0,1;0rad)
  Tip = -> MultiTransform002
FEATURE [PartDesign::FeatureBase] Clone  label="BB_Clone1"
  BaseFeature = -> Body014
  Placement = pos=(0,-46,0) rot=(0,0,1;0rad)
FEATURE [PartDesign::FeatureBase] Clone001  label="BB_Clone2"
  BaseFeature = -> Body014
  Placement = pos=(0,46,0) rot=(0,0,1;0rad)
FEATURE [PartDesign::FeatureBase] Clone002  label="BBP_Clone1"
  BaseFeature = -> Body015
  Placement = pos=(0,22.8,0) rot=(0,0,1;0rad)
FEATURE [PartDesign::FeatureBase] Clone003  label="BBP_Clone2"
  BaseFeature = -> Body015
  Placement = pos=(0,-68.8,0) rot=(0,0,1;0rad)
FEATURE [PartDesign::FeatureBase] Clone004  label="BBP_Clone3"
  BaseFeature = -> Body015
  Placement = pos=(0,68.8,0) rot=(0,0,1;0rad)
FEATURE [App::Part] Part014  label="BreadBoards_Part"
  Group = -> [Body014,Body015,Clone,Clone001,Clone002,Clone003,Clone004]
  License = CC BY 3.0
  LicenseURL = http://creativecommons.org/licenses/by/3.0/
  Origin = -> Origin029
FEATURE [Sketcher::SketchObject] Sketch047  label="ClampSideBase_Sketch"
  MapMode = 5
  Placement = pos=(0,0,0) rot=(1,0,0;1.5708rad)
  Support = -> [XZ_Plane032]
  sketch-geometry (12):
    g0: LineSegment StartX=-10 StartY=27 StartZ=0 EndX=10 EndY=27 EndZ=0
    g1: LineSegment StartX=10 StartY=27 StartZ=0 EndX=10 EndY=5 EndZ=0
    g2: LineSegment StartX=10 StartY=5 StartZ=0 EndX=-10 EndY=5 EndZ=0
    g3: LineSegment StartX=-10 StartY=5 StartZ=0 EndX=-10 EndY=27 EndZ=0
    g4: LineSegment [constr] StartX=0 StartY=0 StartZ=0 EndX=0 EndY=5 EndZ=0
    g5: LineSegment [constr] StartX=-14 StartY=32.5 StartZ=0 EndX=14 EndY=32.5 EndZ=0
    g6: LineSegment [constr] StartX=14 StartY=32.5 StartZ=0 EndX=14 EndY=-7.5 EndZ=0
    g7: LineSegment [constr] StartX=14 StartY=-7.5 StartZ=0 EndX=-14 EndY=-7.5 EndZ=0
    g8: LineSegment [constr] StartX=-14 StartY=-7.5 StartZ=0 EndX=-14 EndY=32.5 EndZ=0
    g9: LineSegment [constr] StartX=0 StartY=-7.5 StartZ=0 EndX=0 EndY=2.5 EndZ=0
    g10: LineSegment [constr] StartX=-14 StartY=27 StartZ=0 EndX=-10 EndY=27 EndZ=0
    g11: LineSegment [constr] StartX=10 StartY=27 StartZ=0 EndX=14 EndY=27 EndZ=0
  constraints (36):
    c: Coincident(g0,g1)
    c: Coincident(g1,g2)
    c: Coincident(g2,g3)
    c: Coincident(g3,g0)
    c: Horizontal(g0)
    c: Horizontal(g2)
    c: Vertical(g1)
    c: Vertical(g3)
    c: DistanceX(g0,g0) = 20
    c: DistanceY(g1,g1) = 22
    c: Vertical(g4)
    c: DistanceY(g4,g4) = -5
    c: Coincident(g4,g-1)
    c: Symmetric(g2,g2,g4)
    c: Coincident(g5,g6)
    c: Coincident(g6,g7)
    c: Coincident(g7,g8)
    c: Coincident(g8,g5)
    c: Horizontal(g5)
    c: Horizontal(g7)
    c: Vertical(g6)
    c: Vertical(g8)
    c: DistanceY(g6,g6) = 40
    c: Vertical(g9)
    c: Symmetric(g7,g7,g9)
    c: Horizontal(g11)
    c: Equal(g11,g10)
    c: Horizontal(g10)
    c: DistanceX(g10,g10) = 4
    c: Coincident(g0,g11)
    c: Coincident(g0,g10)
    c: PointOnObject(g10,g8)
    c: PointOnObject(g11,g6)
    c: Symmetric(g4,g4,g9)
    c: DistanceY(g9,g9) = 10
    c: DistanceY(g11,g5) = 5.5
FEATURE [PartDesign::Pad] Pad014  label="ClampSideBase_Pad"
  Length = 4
  Length2 = 100
  Placement = pos=(0,0,0) rot=(1,0,0;1.5708rad)
  Profile = -> Sketch047
  Type = 0
FEATURE [Sketcher::SketchObject] Sketch048  label="ClampSideBase_screwhole_Sketch"
  ExternalGeometry = -> [Pad014]
  MapMode = 5
  Placement = pos=(0,-4,0) rot=(1,0,0;1.5708rad)
  Support = -> [Pad014]
  expr: Constraints[15] = 3.2000000000000002 / 2
  expr: Constraints[14] = 5.5 / 2
  sketch-geometry (10):
    g0: ArcOfCircle [constr] CenterX=1e-12 CenterY=21.25 CenterZ=0 NormalX=0 NormalY=0 NormalZ=1 AngleXU=0 Radius=2.75 StartAngle=0 EndAngle=3.14159
    g1: ArcOfCircle [constr] CenterX=1e-12 CenterY=10.75 CenterZ=0 NormalX=0 NormalY=0 NormalZ=1 AngleXU=0 Radius=2.75 StartAngle=3.14159 EndAngle=6.28319
    g2: LineSegment [constr] StartX=-2.75 StartY=21.25 StartZ=0 EndX=-2.75 EndY=10.75 EndZ=0
    g3: LineSegment [constr] StartX=2.75 StartY=21.25 StartZ=0 EndX=2.75 EndY=10.75 EndZ=0
    g4: ArcOfCircle CenterX=1e-12 CenterY=21.25 CenterZ=0 NormalX=0 NormalY=0 NormalZ=1 AngleXU=0 Radius=1.6 StartAngle=0 EndAngle=3.14159
    g5: ArcOfCircle CenterX=1e-12 CenterY=10.75 CenterZ=0 NormalX=0 NormalY=0 NormalZ=1 AngleXU=0 Radius=1.6 StartAngle=3.14159 EndAngle=6.28319
    g6: LineSegment StartX=-1.6 StartY=21.25 StartZ=0 EndX=-1.6 EndY=10.75 EndZ=0
    g7: LineSegment StartX=1.6 StartY=21.25 StartZ=0 EndX=1.6 EndY=10.75 EndZ=0
    g8: LineSegment [constr] StartX=0 StartY=27 StartZ=0 EndX=0 EndY=24 EndZ=0
    g9: LineSegment [constr] StartX=0 StartY=8 StartZ=0 EndX=0 EndY=5 EndZ=0
  constraints (25):
    c: Tangent(g0,g3) = 1.5708
    c: Tangent(g0,g2) = -1.5708
    c: Tangent(g2,g1) = -1.5708
    c: Tangent(g3,g1) = 1.5708
    c: Vertical(g2)
    c: Equal(g0,g1)
    c: Tangent(g4,g7) = 1.5708
    c: Tangent(g4,g6) = -1.5708
    c: Tangent(g6,g5) = -1.5708
    c: Tangent(g7,g5) = 1.5708
    c: Vertical(g6)
    c: Equal(g4,g5)
    c: Coincident(g4,g0)
    c: Coincident(g5,g1)
    c: Radius(g0) = 2.75
    c: Radius(g4) = 1.6
    c: DistanceY(g1,g0) = 10.5
    c: Vertical(g8)
    c: Vertical(g9)
    c: Equal(g8,g9)
    c: Symmetric(g-3,g-3,g8)
    c: Symmetric(g-4,g-4,g9)
    c: Perpendicular(g9,g1) = 1.5708
    c: Perpendicular(g8,g0) = 4.71239
    c: DistanceY(g9,g9) = 3
FEATURE [PartDesign::Pocket] Pocket019  label="ClampSideBase_screwhole_Pocket"
  BaseFeature = -> Pad014
  Length = 5
  Length2 = 100
  Placement = pos=(0,0,0) rot=(1,0,0;1.5708rad)
  Profile = -> Sketch048
  Type = 1
FEATURE [PartDesign::Body] Body016  label="ClampSideBase_Body"
  Group = -> [Sketch047,Pad014,Sketch048,Pocket019]
  Origin = -> Origin032
  Tip = -> Pocket019
FEATURE [PartDesign::Plane] DatumPlane011
  MapMode = 5
  Placement = pos=(0,-4,0) rot=(1,0,0;1.5708rad)
  Support = -> [Pocket019]
FEATURE [PartDesign::ShapeBinder] ShapeBinder042
  Placement = pos=(0,0,0) rot=(1,0,0;1.5708rad)
  Support = -> [Pocket019]
FEATURE [Sketcher::SketchObject] Sketch049  label="ClampSideTop_Sketch"
  ExternalGeometry = -> [ShapeBinder042]
  MapMode = 5
  Placement = pos=(0,-4,0) rot=(1,0,0;1.5708rad)
  Support = -> [DatumPlane011]
  sketch-geometry (4):
    g0: LineSegment StartX=-10 StartY=27 StartZ=0 EndX=10 EndY=27 EndZ=0
    g1: LineSegment StartX=10 StartY=27 StartZ=0 EndX=10 EndY=5 EndZ=0
    g2: LineSegment StartX=10 StartY=5 StartZ=0 EndX=-10 EndY=5 EndZ=0
    g3: LineSegment StartX=-10 StartY=5 StartZ=0 EndX=-10 EndY=27 EndZ=0
  constraints (10):
    c: Coincident(g0,g1)
    c: Coincident(g2,g3)
    c: Coincident(g3,g0)
    c: Horizontal(g0)
    c: Horizontal(g2)
    c: Vertical(g1)
    c: Vertical(g3)
    c: Coincident(g0,g-3)
    c: Coincident(g1,g-4)
    c: Coincident(g2,g1)
FEATURE [PartDesign::Pad] Pad015  label="ClampSideTop_Pad"
  Length = 4
  Length2 = 100
  Placement = pos=(0,-4,0) rot=(1,0,0;1.5708rad)
  Profile = -> Sketch049
  Type = 0
FEATURE [Sketcher::SketchObject] Sketch050  label="ClampSideTop_nut_Sketch"
  ExternalGeometry = -> [ShapeBinder042]
  MapMode = 5
  Placement = pos=(0,-8,-1e-12) rot=(1,0,0;1.5708rad)
  Support = -> [Pad015]
  sketch-geometry (4):
    g0: ArcOfCircle CenterX=1e-12 CenterY=21.25 CenterZ=0 NormalX=0 NormalY=0 NormalZ=1 AngleXU=0 Radius=2.75 StartAngle=0 EndAngle=3.14159
    g1: ArcOfCircle CenterX=1e-12 CenterY=10.75 CenterZ=0 NormalX=0 NormalY=0 NormalZ=1 AngleXU=0 Radius=2.75 StartAngle=3.14159 EndAngle=6.28319
    g2: LineSegment StartX=-2.75 StartY=21.25 StartZ=0 EndX=-2.75 EndY=10.75 EndZ=0
    g3: LineSegment StartX=2.75 StartY=21.25 StartZ=0 EndX=2.75 EndY=10.75 EndZ=0
  constraints (9):
    c: Tangent(g0,g3) = 1.5708
    c: Tangent(g0,g2) = -1.5708
    c: Tangent(g2,g1) = -1.5708
    c: Tangent(g3,g1) = 1.5708
    c: Vertical(g2)
    c: Equal(g0,g1)
    c: DistanceX(g0,g0) = 5.5
    c: Coincident(g0,g-5)
    c: Coincident(g1,g-4)
FEATURE [PartDesign::Pocket] Pocket020  label="ClampSideTop_nut_Pocket"
  BaseFeature = -> Pad015
  Length = 5
  Length2 = 100
  Placement = pos=(0,-4,0) rot=(1,0,0;1.5708rad)
  Profile = -> Sketch050
  Type = 1
FEATURE [PartDesign::Body] Body017  label="ClampSideTop_Body"
  Group = -> [DatumPlane011,Sketch049,ShapeBinder042,Pad015,Sketch050,Pocket020]
  Origin = -> Origin033
  Tip = -> Pocket020
FEATURE [PartDesign::Plane] DatumPlane012
  AttachmentOffset = pos=(0,0,0) rot=(0,0,1;1.5708rad)
  MapMode = 5
  Placement = pos=(-10,0,0) rot=(0.57735,-0.57735,-0.57735;2.0944rad)
  Support = -> [Pocket019]
FEATURE [PartDesign::ShapeBinder] ShapeBinder043
  Placement = pos=(0,0,0) rot=(1,0,0;1.5708rad)
  Support = -> [Pocket019]
FEATURE [PartDesign::ShapeBinder] ShapeBinder044
  Placement = pos=(0,-4,0) rot=(1,0,0;1.5708rad)
  Support = -> [Pocket020]
FEATURE [Sketcher::SketchObject] Sketch051  label="ClampSideWing_Sketch"
  ExternalGeometry = -> [ShapeBinder044,ShapeBinder043]
  MapMode = 5
  Placement = pos=(-10,0,0) rot=(0.57735,-0.57735,-0.57735;2.0944rad)
  Support = -> [DatumPlane012]
  sketch-geometry (7):
    g0: LineSegment StartX=0 StartY=27 StartZ=0 EndX=8 EndY=27 EndZ=0
    g1: LineSegment StartX=8 StartY=27 StartZ=0 EndX=8 EndY=5 EndZ=0
    g2: LineSegment [constr] StartX=8 StartY=5 StartZ=0 EndX=0 EndY=5 EndZ=0
    g3: LineSegment StartX=0 StartY=5 StartZ=0 EndX=0 EndY=27 EndZ=0
    g4: LineSegment StartX=0 StartY=5 StartZ=0 EndX=0 EndY=0 EndZ=0
    g5: LineSegment StartX=0 StartY=0 StartZ=0 EndX=8 EndY=5 EndZ=0
    g6: GeomPoint X=4 Y=2.5 Z=0
  constraints (18):
    c: Coincident(g0,g1)
    c: Coincident(g1,g2)
    c: Coincident(g2,g3)
    c: Coincident(g3,g0)
    c: Horizontal(g0)
    c: Horizontal(g2)
    c: Vertical(g1)
    c: Vertical(g3)
    c: Coincident(g0,g-4)
    c: Coincident(g1,g-3)
    c: Coincident(g2,g4)
    c: Coincident(g4,g-1)
    c: Coincident(g4,g5)
    c: Coincident(g5,g1)
    c: DistanceY(g4,g4) = 5
    c: Symmetric(g5,g5,g6)
    c: DistanceY(g-1,g6) = 2.5
    c: DistanceX(g-1,g6) = 4
FEATURE [PartDesign::Pad] Pad016  label="ClampSideWing_Pad"
  Length = 4
  Length2 = 100
  Placement = pos=(-10,0,0) rot=(0.57735,-0.57735,-0.57735;2.0944rad)
  Profile = -> Sketch051
  Type = 0
FEATURE [PartDesign::Body] Body018  label="ClampSideWing_Body"
  Group = -> [DatumPlane012,ShapeBinder043,ShapeBinder044,Sketch051,Pad016]
  Origin = -> Origin034
  Tip = -> Pad016
FEATURE [PartDesign::FeatureBase] Clone005  label="ClampSideWing_Clone"
  BaseFeature = -> Body018
  Placement = pos=(24,0,0) rot=(0,0,1;0rad)
FEATURE [TechDraw::DrawSVGTemplate] Template013  label="ClampSideBase_Template"
  Height = 210
  Orientation = 1
  Width = 297
FEATURE [TechDraw::DrawSVGTemplate] Template014  label="ClampSideTop_Template"
  Height = 210
  Orientation = 1
  Width = 297
FEATURE [TechDraw::DrawSVGTemplate] Template015  label="ClampSideWing_Template"
  Height = 210
  Orientation = 1
  Width = 297
FEATURE [TechDraw::DrawViewPart] View013  label="ClampSideBase_View"
  CoarseView = false
  Direction = (0,1,0)
  Focus = 100
  HardHidden = false
  IsoCount = 0
  IsoHidden = false
  IsoVisible = false
  LockPosition = false
  Perspective = false
  Rotation = 0
  ScaleType = 0
  SeamHidden = false
  SeamVisible = false
  SmoothHidden = false
  SmoothVisible = false
  Source = -> [Body016]
  X = 148.5
  Y = 105
FEATURE [TechDraw::DrawPage] Page013  label="ClampSideBase_Page"
  KeepUpdated = true
  ProjectionType = 0
  Template = -> Template013
  Views = -> [View013]
FEATURE [TechDraw::DrawViewPart] View014  label="ClampSideTop_View"
  CoarseView = false
  Direction = (0,1,0)
  Focus = 100
  HardHidden = false
  IsoCount = 0
  IsoHidden = false
  IsoVisible = false
  LockPosition = false
  Perspective = false
  Rotation = 0
  ScaleType = 0
  SeamHidden = false
  SeamVisible = false
  SmoothHidden = false
  SmoothVisible = false
  Source = -> [Body017]
  X = 148.5
  Y = 105
FEATURE [TechDraw::DrawPage] Page014  label="ClampSideTop_Page"
  KeepUpdated = true
  ProjectionType = 0
  Template = -> Template014
  Views = -> [View014]
FEATURE [TechDraw::DrawViewPart] View015  label="ClampSideWing_View"
  CoarseView = false
  Direction = (1,0,0)
  Focus = 100
  HardHidden = false
  IsoCount = 0
  IsoHidden = false
  IsoVisible = false
  LockPosition = false
  Perspective = false
  Rotation = 0
  ScaleType = 0
  SeamHidden = false
  SeamVisible = false
  SmoothHidden = false
  SmoothVisible = false
  Source = -> [Body018]
  X = 148.5
  Y = 105
FEATURE [TechDraw::DrawPage] Page015  label="ClampSideWing_Page"
  KeepUpdated = true
  ProjectionType = 0
  Template = -> Template015
  Views = -> [View015]
FEATURE [App::Part] Part015  label="ClampSide_Part"
  Group = -> [Body016,Body017,Body018,Clone005,Template013,Page013,Template014,Page014,Template015,Page015]
  License = CC BY 3.0
  LicenseURL = http://creativecommons.org/licenses/by/3.0/
  Origin = -> Origin031
  Placement = pos=(39.5,75,8) rot=(0,0,1;0rad)
FEATURE [TechDraw::DrawSVGTemplate] Template016
  EditableTexts = Designed by Name=Stefan Krüger; Drawing number=Drawing number; FC-Date=17.07.2017; FC-SC=1:1; FC-SH=Sheet; FC-Title=Title; Subtitle=Subtitle; Weight=Weight
  Height = 210
  Orientation = 1
  Width = 297
FEATURE [TechDraw::DrawViewPart] View016
  CoarseView = false
  Direction = (0,0,1)
  Focus = 100
  HardHidden = false
  IsoCount = 0
  IsoHidden = false
  IsoVisible = false
  LockPosition = false
  Perspective = false
  Rotation = 0
  ScaleType = 0
  SeamHidden = false
  SeamVisible = false
  SmoothHidden = false
  SmoothVisible = false
  Source = -> [Body013]
  X = 148.5
  Y = 105
FEATURE [TechDraw::DrawViewDimension] Dimension002
  FormatSpec = %.3f
  LockPosition = false
  MeasureType = 1
  References2D = -> [View016]
  Rotation = 0
  ScaleType = 0
  Type = 2
  X = -92.0259
  Y = 3.31897
FEATURE [TechDraw::DrawPage] Page016  label="LidOut_Measurements_Page"
  KeepUpdated = true
  ProjectionType = 0
  Template = -> Template016
  Views = -> [View016,Dimension002]
FEATURE [App::Part] Part010  label="LidOut_Part"
  Group = -> [Body013,Template011,Page011,Template016,Page016]
  License = CC BY 3.0
  LicenseURL = http://creativecommons.org/licenses/by/3.0/
  Origin = -> Origin020
FEATURE [TechDraw::DrawSVGTemplate] Template017  label="LidIn_Template"
  Height = 210
  Orientation = 1
  Width = 297
FEATURE [PartDesign::ShapeBinder] ShapeBinder045
  Placement = pos=(-31.1547,0,47) rot=(0,0,-1;1.5708rad)
  Support = -> [Sketch029]
FEATURE [PartDesign::Plane] DatumPlane013
  MapMode = 5
  Placement = pos=(0,79,40) rot=(0,0,1;3.14159rad)
  Support = -> [Hole005]
FEATURE [PartDesign::ShapeBinder] ShapeBinder046
  Placement = pos=(0,79,0) rot=(1,0,0;1.5708rad)
  Support = -> [Hole005]
FEATURE [PartDesign::ShapeBinder] ShapeBinder047
  Placement = pos=(-129,0,-4) rot=(0.57735,0.57735,0.57735;2.0944rad)
  Support = -> [Pocket011]
FEATURE [Sketcher::SketchObject] Sketch052  label="LidIn_Sketch"
  ExternalGeometry = -> [ShapeBinder045,ShapeBinder047,ShapeBinder046]
  MapMode = 5
  Placement = pos=(0,79,40) rot=(0,0,1;3.14159rad)
  Support = -> [DatumPlane013]
  sketch-geometry (5):
    g0: ArcOfCircle CenterX=63 CenterY=8 CenterZ=0 NormalX=0 NormalY=0 NormalZ=1 AngleXU=0 Radius=10 StartAngle=1.5708 EndAngle=3.14159
    g1: LineSegment StartX=63 StartY=18 StartZ=0 EndX=129 EndY=18 EndZ=0
    g2: LineSegment StartX=53 StartY=8 StartZ=0 EndX=53 EndY=0 EndZ=0
    g3: LineSegment StartX=53 StartY=0 StartZ=0 EndX=129 EndY=0 EndZ=0
    g4: LineSegment StartX=129 StartY=18 StartZ=0 EndX=129 EndY=0 EndZ=0
  constraints (13):
    c: Coincident(g0,g-6)
    c: Coincident(g0,g-6)
    c: Coincident(g1,g0)
    c: Horizontal(g1)
    c: Coincident(g3,g2)
    c: Horizontal(g3)
    c: Coincident(g4,g1)
    c: Coincident(g4,g3)
    c: Vertical(g4)
    c: Vertical(g2)
    c: PointOnObject(g1,g-9)
    c: PointOnObject(g2,g-10)
    c: Tangent(g2,g0) = -1.5708
FEATURE [PartDesign::Pad] Pad017  label="LidIn_Pad"
  Length = 4
  Length2 = 100
  Placement = pos=(0,79,40) rot=(0,0,1;3.14159rad)
  Profile = -> Sketch052
  Reversed = true
  Type = 0
FEATURE [PartDesign::Body] Body019  label="LidIn_Body"
  Group = -> [ShapeBinder045,DatumPlane013,Sketch052,ShapeBinder046,ShapeBinder047,Pad017]
  Origin = -> Origin036
  Tip = -> Pad017
FEATURE [TechDraw::DrawViewPart] View017  label="LidIn_View"
  CoarseView = false
  Direction = (0,0,1)
  Focus = 100
  HardHidden = false
  IsoCount = 0
  IsoHidden = false
  IsoVisible = false
  LockPosition = false
  Perspective = false
  Rotation = 0
  ScaleType = 0
  SeamHidden = false
  SeamVisible = false
  SmoothHidden = false
  SmoothVisible = false
  Source = -> [Body019]
  X = 148.5
  Y = 105
FEATURE [TechDraw::DrawPage] Page017  label="LidIn_Page"
  KeepUpdated = true
  ProjectionType = 0
  Template = -> Template017
  Views = -> [View017]
FEATURE [App::Part] Part016  label="LidIn_Part"
  Group = -> [Body019,Template017,Page017]
  License = CC BY 3.0
  LicenseURL = http://creativecommons.org/licenses/by/3.0/
  Origin = -> Origin035
FEATURE [TechDraw::DrawSVGTemplate] Template018  label="LidSpacer_Template"
  Height = 210
  Orientation = 1
  Width = 297
FEATURE [PartDesign::Plane] DatumPlane014
  MapMode = 5
  Placement = pos=(0,79,40) rot=(0,0,1;3.14159rad)
  Support = -> [Pad017]
FEATURE [PartDesign::ShapeBinder] ShapeBinder048
  Support = -> [Pad017]
FEATURE [Sketcher::SketchObject] Sketch053  label="LidSpacer_Sketch"
  ExternalGeometry = -> [ShapeBinder048]
  MapMode = 5
  Placement = pos=(0,79,40) rot=(0,0,1;3.14159rad)
  Support = -> [DatumPlane014]
  sketch-geometry (4):
    g0: LineSegment StartX=63 StartY=12 StartZ=0 EndX=129 EndY=12 EndZ=0
    g1: LineSegment StartX=129 StartY=12 StartZ=0 EndX=129 EndY=0 EndZ=0
    g2: LineSegment StartX=129 StartY=0 StartZ=0 EndX=63 EndY=0 EndZ=0
    g3: LineSegment StartX=63 StartY=0 StartZ=0 EndX=63 EndY=12 EndZ=0
  constraints (13):
    c: Coincident(g0,g1)
    c: Coincident(g1,g2)
    c: Coincident(g2,g3)
    c: Coincident(g3,g0)
    c: Horizontal(g0)
    c: Horizontal(g2)
    c: Vertical(g1)
    c: Vertical(g3)
    c: Coincident(g1,g-4)
    c: PointOnObject(g-6,g3)
    c: DistanceX(g0,g0) = 66
    c: DistanceY(g0,g-4) = 6
    c: DistanceY(g1,g1) = 12
FEATURE [PartDesign::Pad] Pad018  label="LidSpacer_Pad"
  Length = 3
  Length2 = 100
  Placement = pos=(0,79,40) rot=(0,0,1;3.14159rad)
  Profile = -> Sketch053
  Type = 0
FEATURE [PartDesign::Body] Body020  label="LidSpacer_Body"
  Group = -> [DatumPlane014,ShapeBinder048,Sketch053,Pad018]
  Origin = -> Origin038
  Tip = -> Pad018
FEATURE [TechDraw::DrawViewPart] View018  label="LidSpacer_View"
  CoarseView = false
  Direction = (0,0,1)
  Focus = 100
  HardHidden = false
  IsoCount = 0
  IsoHidden = false
  IsoVisible = false
  LockPosition = false
  Perspective = false
  Rotation = 0
  ScaleType = 0
  SeamHidden = false
  SeamVisible = false
  SmoothHidden = false
  SmoothVisible = false
  Source = -> [Body020]
  X = 148.5
  Y = 105
FEATURE [TechDraw::DrawPage] Page018  label="LidSpacer_Page"
  KeepUpdated = true
  ProjectionType = 0
  Template = -> Template018
  Views = -> [View018]
FEATURE [App::Part] Part017  label="LidSpacer_Part"
  Group = -> [Template018,Page018,Body020]
  License = CC BY 3.0
  LicenseURL = http://creativecommons.org/licenses/by/3.0/
  Origin = -> Origin037
FEATURE [PartDesign::ShapeBinder] ShapeBinder049
  Placement = pos=(0,0,3) rot=(0,0,1;0rad)
  Support = -> [Pad018]
FEATURE [Sketcher::SketchObject] Sketch014  label="LidSlide_Sketch"
  ExternalGeometry = -> [ShapeBinder019,ShapeBinder020,ShapeBinder021,ShapeBinder022,ShapeBinder023,ShapeBinder049]
  MapMode = 5
  Placement = pos=(-31.1547,0,43) rot=(0.707107,-0.707107,0;3.14159rad)
  Support = -> [DatumPlane010]
  sketch-geometry (4):
    g0: LineSegment StartX=-79 StartY=31.8453 StartZ=0 EndX=79 EndY=31.8453 EndZ=0
    g1: LineSegment StartX=79 StartY=31.8453 StartZ=0 EndX=79 EndY=-164.155 EndZ=0
    g2: LineSegment StartX=79 StartY=-164.155 StartZ=0 EndX=-79 EndY=-164.155 EndZ=0
    g3: LineSegment StartX=-79 StartY=-164.155 StartZ=0 EndX=-79 EndY=31.8453 EndZ=0
  constraints (10):
    c: Coincident(g0,g1)
    c: Coincident(g1,g2)
    c: Coincident(g2,g3)
    c: Coincident(g3,g0)
    c: Horizontal(g0)
    c: Horizontal(g2)
    c: Vertical(g1)
    c: Vertical(g3)
    c: Coincident(g1,g-5)
    c: Coincident(g0,g-9)
FEATURE [PartDesign::Pad] Pad011  label="LidSlide_Pad"
  Length = 3
  Length2 = 100
  Placement = pos=(-31.1547,0,43) rot=(0.707107,-0.707107,0;3.14159rad)
  Profile = -> Sketch014
  Type = 0
FEATURE [PartDesign::Body] Body010  label="LidSlide_Body"
  Group = -> [DatumPlane010,ShapeBinder019,ShapeBinder020,ShapeBinder021,ShapeBinder022,ShapeBinder023,Sketch014,Pad011,ShapeBinder049]
  Origin = -> Origin022
  Tip = -> Pad011
FEATURE [TechDraw::DrawViewPart] View
  CoarseView = false
  Direction = (0,0,1)
  Focus = 100
  HardHidden = false
  IsoCount = 0
  IsoHidden = false
  IsoVisible = false
  LockPosition = false
  Perspective = false
  Rotation = 0
  ScaleType = 0
  SeamHidden = false
  SeamVisible = false
  SmoothHidden = false
  SmoothVisible = false
  Source = -> [Pad011]
  X = 148.5
  Y = 105
FEATURE [TechDraw::DrawViewDimension] Dimension
  FormatSpec = %.3f
  LockPosition = false
  MeasureType = 1
  References2D = -> [View]
  Rotation = 0
  ScaleType = 0
  Type = 1
  X = -0.947368
  Y = -52.1053
FEATURE [TechDraw::DrawViewDimension] Dimension001
  FormatSpec = %.3f
  LockPosition = false
  MeasureType = 1
  References2D = -> [View]
  Rotation = 0
  ScaleType = 0
  Type = 2
  X = 0
  Y = 0
FEATURE [TechDraw::DrawPage] Page  label="LibSlide_Page"
  KeepUpdated = true
  ProjectionType = 0
  Template = -> Template
  Views = -> [View,Dimension,Dimension001]
FEATURE [TechDraw::DrawViewPart] View012  label="LidSlide_View"
  CoarseView = false
  Direction = (0,0,1)
  Focus = 100
  HardHidden = false
  IsoCount = 0
  IsoHidden = false
  IsoVisible = false
  LockPosition = false
  Perspective = false
  Rotation = 0
  ScaleType = 0
  SeamHidden = false
  SeamVisible = false
  SmoothHidden = false
  SmoothVisible = false
  Source = -> [Body010]
  X = 148.5
  Y = 105
FEATURE [TechDraw::DrawPage] Page012  label="LidSlide_Page"
  KeepUpdated = true
  ProjectionType = 0
  Template = -> Template012
  Views = -> [View012]
FEATURE [PartDesign::Plane] DatumPlane015
  MapMode = 5
  Placement = pos=(-31.1547,0,43) rot=(0,0,-1;1.5708rad)
  Support = -> [Pad011]
FEATURE [PartDesign::ShapeBinder] ShapeBinder050
  Support = -> [Pad011]
FEATURE [PartDesign::ShapeBinder] ShapeBinder051
  Placement = pos=(0,0,3) rot=(0,0,1;0rad)
  Support = -> [Pad018]
FEATURE [Sketcher::SketchObject] Sketch054  label="LidSlideSmall_Sketch"
  ExternalGeometry = -> [ShapeBinder050,ShapeBinder051]
  MapMode = 5
  Placement = pos=(-31.1547,0,43) rot=(0,0,-1;1.5708rad)
  Support = -> [DatumPlane015]
  sketch-geometry (4):
    g0: LineSegment StartX=-67 StartY=-31.8453 StartZ=0 EndX=79 EndY=-31.8453 EndZ=0
    g1: LineSegment StartX=79 StartY=-31.8453 StartZ=0 EndX=79 EndY=-97.8453 EndZ=0
    g2: LineSegment StartX=79 StartY=-97.8453 StartZ=0 EndX=-67 EndY=-97.8453 EndZ=0
    g3: LineSegment StartX=-67 StartY=-97.8453 StartZ=0 EndX=-67 EndY=-31.8453 EndZ=0
  constraints (11):
    c: Coincident(g0,g1)
    c: Coincident(g1,g2)
    c: Coincident(g2,g3)
    c: Coincident(g3,g0)
    c: Horizontal(g0)
    c: Horizontal(g2)
    c: Vertical(g1)
    c: Vertical(g3)
    c: Coincident(g0,g-4)
    c: Coincident(g2,g-4)
    c: Coincident(g0,g-3)
FEATURE [TechDraw::DrawSVGTemplate] Template019  label="LidSlideSmall_Template"
  Height = 210
  Orientation = 1
  Width = 297
FEATURE [PartDesign::Pad] Pad019  label="LidSlideSmall_Pad"
  Length = 4
  Length2 = 100
  Placement = pos=(-31.1547,0,43) rot=(0,0,-1;1.5708rad)
  Profile = -> Sketch054
  Reversed = true
  Type = 0
FEATURE [PartDesign::Body] Body021  label="LidSlideSmall_Body"
  Group = -> [DatumPlane015,ShapeBinder050,ShapeBinder051,Sketch054,Pad019]
  Origin = -> Origin040
  Tip = -> Pad019
FEATURE [TechDraw::DrawViewPart] View019  label="LidSlideSmall_View"
  CoarseView = false
  Direction = (0,0,1)
  Focus = 100
  HardHidden = false
  IsoCount = 0
  IsoHidden = false
  IsoVisible = false
  LockPosition = false
  Perspective = false
  Rotation = 0
  ScaleType = 0
  SeamHidden = false
  SeamVisible = false
  SmoothHidden = false
  SmoothVisible = false
  Source = -> [Body021]
  X = 148.5
  Y = 105
FEATURE [TechDraw::DrawPage] Page019  label="LidSlideSmall_Page"
  KeepUpdated = true
  ProjectionType = 0
  Template = -> Template019
  Views = -> [View019]
FEATURE [App::Part] Part011  label="LidSlide_Part"
  Group = -> [Body010,Template,Page,Template012,Page012,Body021,Template019,Page019]
  License = CC BY 3.0
  LicenseURL = http://creativecommons.org/licenses/by/3.0/
  Origin = -> Origin021
FEATURE [PartDesign::ShapeBinder] ShapeBinder052
  Placement = pos=(0,79,40) rot=(0,0,1;3.14159rad)
  Support = -> [Pad017]
FEATURE [Sketcher::SketchObject] Sketch055  label="TopIn_LidInCutout_Sketch"
  ExternalGeometry = -> [ShapeBinder052]
  MapMode = 5
  Placement = pos=(0,79,0) rot=(-1,0,0;1.5708rad)
  Support = -> [Pocket007]
  sketch-geometry (4):
    g0: LineSegment StartX=-129 StartY=-36 StartZ=0 EndX=-53 EndY=-36 EndZ=0
    g1: LineSegment StartX=-53 StartY=-36 StartZ=0 EndX=-53 EndY=-46 EndZ=0
    g2: LineSegment StartX=-53 StartY=-46 StartZ=0 EndX=-129 EndY=-46 EndZ=0
    g3: LineSegment StartX=-129 StartY=-46 StartZ=0 EndX=-129 EndY=-36 EndZ=0
  constraints (11):
    c: Coincident(g0,g1)
    c: Coincident(g1,g2)
    c: Coincident(g2,g3)
    c: Coincident(g3,g0)
    c: Horizontal(g0)
    c: Horizontal(g2)
    c: Vertical(g1)
    c: Vertical(g3)
    c: Coincident(g-3,g0)
    c: Coincident(g0,g-3)
    c: DistanceY(g3,g3) = 10
FEATURE [PartDesign::Pocket] Pocket021  label="TopIn_LidInCutout_Pocket"
  BaseFeature = -> Hole005
  Length = 5
  Length2 = 100
  Placement = pos=(0,79,0) rot=(1,0,0;1.5708rad)
  Profile = -> Sketch055
  Type = 1
FEATURE [PartDesign::Body] Body007  label="TopIn_Body"
  Group = -> [ShapeBinder003,DatumPlane002,Sketch006,Pad003,ShapeBinder029,Sketch024,Pocket007,Sketch031,Pocket014,ShapeBinder039,Sketch040,Hole005,ShapeBinder052,Sketch055,Pocket021]
  Origin = -> Origin015
  Tip = -> Pocket021
FEATURE [TechDraw::DrawViewPart] View008  label="TopIn_View"
  CoarseView = false
  Direction = (0,1,0)
  Focus = 100
  HardHidden = false
  IsoCount = 0
  IsoHidden = false
  IsoVisible = false
  LockPosition = false
  Perspective = false
  Rotation = 0
  ScaleType = 0
  SeamHidden = false
  SeamVisible = false
  SmoothHidden = false
  SmoothVisible = false
  Source = -> [Body007]
  X = 148.5
  Y = 105
FEATURE [TechDraw::DrawPage] Page008  label="TopIn_Page"
  KeepUpdated = true
  ProjectionType = 0
  Template = -> Template008
  Views = -> [View008]
FEATURE [App::Part] Part007  label="TopIn_Part"
  Group = -> [Body007,Template008,Page008]
  License = CC BY 3.0
  LicenseURL = http://creativecommons.org/licenses/by/3.0/
  Origin = -> Origin014
FEATURE [PartDesign::ShapeBinder] ShapeBinder053
  Placement = pos=(0,79,40) rot=(0,0,1;3.14159rad)
  Support = -> [Pad017]
FEATURE [Sketcher::SketchObject] Sketch056  label="LeftIn_LidIn_Cutout_Sketch"
  ExternalGeometry = -> [ShapeBinder053]
  MapMode = 5
  Placement = pos=(-129,0,-4) rot=(0.57735,0.57735,-0.57735;4.18879rad)
  Support = -> [Pocket011]
  sketch-geometry (4):
    g0: LineSegment StartX=61 StartY=-40 StartZ=0 EndX=79 EndY=-40 EndZ=0
    g1: LineSegment StartX=79 StartY=-40 StartZ=0 EndX=79 EndY=-50 EndZ=0
    g2: LineSegment StartX=79 StartY=-50 StartZ=0 EndX=61 EndY=-50 EndZ=0
    g3: LineSegment StartX=61 StartY=-50 StartZ=0 EndX=61 EndY=-40 EndZ=0
  constraints (11):
    c: Coincident(g0,g1)
    c: Coincident(g1,g2)
    c: Coincident(g2,g3)
    c: Coincident(g3,g0)
    c: Horizontal(g0)
    c: Horizontal(g2)
    c: Vertical(g1)
    c: Vertical(g3)
    c: Coincident(g0,g-3)
    c: Coincident(g0,g-3)
    c: DistanceY(g3,g3) = 10
FEATURE [PartDesign::Pocket] Pocket022  label="LeftIn_LidIn_Cutout_Pocket"
  BaseFeature = -> Pocket011
  Length = 5
  Length2 = 100
  Placement = pos=(-129,0,-4) rot=(0.57735,0.57735,0.57735;2.0944rad)
  Profile = -> Sketch056
  Type = 1
FEATURE [PartDesign::Body] Body005  label="LeftIn_Body"
  Group = -> [DatumPlane004,ShapeBinder006,ShapeBinder007,Sketch008,Pad005,ShapeBinder033,Sketch028,Pocket011,ShapeBinder053,Sketch056,Pocket022]
  Origin = -> Origin011
  Tip = -> Pocket022
FEATURE [TechDraw::DrawViewPart] View006  label="LeftIn_View"
  CoarseView = false
  Direction = (1,0,0)
  Focus = 100
  HardHidden = false
  IsoCount = 0
  IsoHidden = false
  IsoVisible = false
  LockPosition = false
  Perspective = false
  Rotation = 0
  ScaleType = 0
  SeamHidden = false
  SeamVisible = false
  SmoothHidden = false
  SmoothVisible = false
  Source = -> [Body005]
  X = 148.5
  Y = 105
FEATURE [TechDraw::DrawPage] Page006  label="LeftIn_Page"
  KeepUpdated = true
  ProjectionType = 0
  Template = -> Template006
  Views = -> [View006]
FEATURE [App::Part] Part005  label="LeftIn_Part"
  Group = -> [Body005,Template006,Page006]
  License = CC BY 3.0
  LicenseURL = http://creativecommons.org/licenses/by/3.0/
  Origin = -> Origin010
FEATURE [App::DocumentObjectGroup] Group  label="Housing"
  Group = -> [Part,Part001,Part002,Part003,Part004,Part005,Part006,Part007,Part008,Part009,Part010,Part011,Part013,Part016,Part017]
FEATURE [TechDraw::DrawSVGTemplate] Template020  label="ClampTopBase_Template"
  Height = 210
  Orientation = 1
  Width = 297
FEATURE [TechDraw::DrawSVGTemplate] Template021  label="ClampTopMid_Template"
  Height = 210
  Orientation = 1
  Width = 297
FEATURE [TechDraw::DrawSVGTemplate] Template022  label="ClampTopTop_Template"
  Height = 210
  Orientation = 1
  Width = 297
FEATURE [TechDraw::DrawSVGTemplate] Template023  label="ClampTopWing_Template"
  Height = 210
  Orientation = 1
  Width = 297
FEATURE [Sketcher::SketchObject] Sketch057  label="ClampTopBase_Sketch"
  MapMode = 5
  Support = -> [XY_Plane043]
  sketch-geometry (5):
    g0: LineSegment StartX=-10 StartY=-5 StartZ=0 EndX=10 EndY=-5 EndZ=0
    g1: LineSegment StartX=10 StartY=-5 StartZ=0 EndX=10 EndY=-30 EndZ=0
    g2: LineSegment StartX=10 StartY=-30 StartZ=0 EndX=-10 EndY=-30 EndZ=0
    g3: LineSegment StartX=-10 StartY=-30 StartZ=0 EndX=-10 EndY=-5 EndZ=0
    g4: LineSegment [constr] StartX=0 StartY=0 StartZ=0 EndX=0 EndY=-5 EndZ=0
  constraints (14):
    c: Coincident(g0,g1)
    c: Coincident(g1,g2)
    c: Coincident(g2,g3)
    c: Coincident(g3,g0)
    c: Horizontal(g0)
    c: Horizontal(g2)
    c: Vertical(g1)
    c: Vertical(g3)
    c: Vertical(g4)
    c: Coincident(g4,g-1)
    c: Symmetric(g0,g0,g4)
    c: DistanceX(g2,g2) = 20
    c: DistanceY(g1,g1) = 25
    c: DistanceY(g4,g4) = 5
FEATURE [PartDesign::Pad] Pad020  label="ClampTopBase_Pad"
  Length = 4
  Length2 = 100
  Profile = -> Sketch057
  Type = 0
FEATURE [Sketcher::SketchObject] Sketch058  label="ClampTop_Mounting_Sketch"
  ExternalGeometry = -> [Pad020]
  MapMode = 5
  Placement = pos=(0,0,4) rot=(0,0,1;0rad)
  Support = -> [Pad020]
  sketch-geometry (10):
    g0: ArcOfCircle CenterX=0 CenterY=-11.75 CenterZ=0 NormalX=0 NormalY=0 NormalZ=1 AngleXU=0 Radius=1.6 StartAngle=0 EndAngle=3.14159
    g1: ArcOfCircle CenterX=0 CenterY=-23.25 CenterZ=0 NormalX=0 NormalY=0 NormalZ=1 AngleXU=0 Radius=1.6 StartAngle=3.14159 EndAngle=6.28319
    g2: LineSegment StartX=-1.6 StartY=-11.75 StartZ=0 EndX=-1.6 EndY=-23.25 EndZ=0
    g3: LineSegment StartX=1.6 StartY=-11.75 StartZ=0 EndX=1.6 EndY=-23.25 EndZ=0
    g4: ArcOfCircle [constr] CenterX=0 CenterY=-11.75 CenterZ=0 NormalX=0 NormalY=0 NormalZ=1 AngleXU=0 Radius=2.75 StartAngle=0 EndAngle=3.14159
    g5: ArcOfCircle [constr] CenterX=0 CenterY=-23.25 CenterZ=0 NormalX=0 NormalY=0 NormalZ=1 AngleXU=0 Radius=2.75 StartAngle=3.14159 EndAngle=6.28319
    g6: LineSegment [constr] StartX=-2.75 StartY=-11.75 StartZ=0 EndX=-2.75 EndY=-23.25 EndZ=0
    g7: LineSegment [constr] StartX=2.75 StartY=-11.75 StartZ=0 EndX=2.75 EndY=-23.25 EndZ=0
    g8: LineSegment [constr] StartX=0 StartY=-5 StartZ=0 EndX=0 EndY=-9 EndZ=0
    g9: LineSegment [constr] StartX=0 StartY=-26 StartZ=0 EndX=0 EndY=-30 EndZ=0
  constraints (23):
    c: Tangent(g0,g3) = 1.5708
    c: Tangent(g0,g2) = -1.5708
    c: Tangent(g2,g1) = -1.5708
    c: Tangent(g3,g1) = 1.5708
    c: Vertical(g2)
    c: Equal(g0,g1)
    c: DistanceX(g0,g0) = 3.2
    c: Tangent(g4,g7) = 1.5708
    c: Tangent(g4,g6) = -1.5708
    c: Tangent(g6,g5) = -1.5708
    c: Tangent(g7,g5) = 1.5708
    c: Vertical(g6)
    c: Equal(g4,g5)
    c: Coincident(g4,g0)
    c: Coincident(g5,g1)
    c: DistanceX(g4,g4) = 5.5
    c: Symmetric(g-4,g-4,g9)
    c: Symmetric(g-3,g-3,g8)
    c: Vertical(g8)
    c: Perpendicular(g8,g4) = 4.71239
    c: Perpendicular(g9,g5) = 1.5708
    c: Equal(g9,g8)
    c: DistanceY(g9,g9) = 4
FEATURE [PartDesign::Pocket] Pocket023  label="ClampTopBase_Pocket"
  BaseFeature = -> Pad020
  Length = 5
  Length2 = 100
  Profile = -> Sketch058
  Type = 1
FEATURE [PartDesign::Body] Body022  label="ClampTopBase_Body"
  Group = -> [Sketch057,Pad020,Sketch058,Pocket023]
  Origin = -> Origin043
  Tip = -> Pocket023
FEATURE [PartDesign::Plane] DatumPlane016
  MapMode = 13
  Placement = pos=(-3.33333,-21.6667,4) rot=(0,0,1;0rad)
  Support = -> [Pocket023]
FEATURE [PartDesign::ShapeBinder] ShapeBinder054
  Placement = pos=(0,0,4) rot=(0,0,1;0rad)
  Support = -> [Sketch058]
FEATURE [PartDesign::ShapeBinder] ShapeBinder055
  Support = -> [Pocket023]
FEATURE [Sketcher::SketchObject] Sketch059  label="ClampTopMid_Sketch"
  ExternalGeometry = -> [ShapeBinder055,ShapeBinder054]
  MapMode = 5
  Placement = pos=(-3.33333,-21.6667,4) rot=(0,0,1;0rad)
  Support = -> [DatumPlane016]
  sketch-geometry (10):
    g0: LineSegment StartX=-10.6667 StartY=16.6667 StartZ=0 EndX=17.3333 EndY=16.6667 EndZ=0
    g1: LineSegment StartX=17.3333 StartY=16.6667 StartZ=0 EndX=17.3333 EndY=-8.33333 EndZ=0
    g2: LineSegment StartX=17.3333 StartY=-8.33333 StartZ=0 EndX=-10.6667 EndY=-8.33333 EndZ=0
    g3: LineSegment StartX=-10.6667 StartY=-8.33333 StartZ=0 EndX=-10.6667 EndY=16.6667 EndZ=0
    g4: LineSegment [constr] StartX=-10.6667 StartY=-8.33333 StartZ=0 EndX=-6.66667 EndY=-8.33333 EndZ=0
    g5: LineSegment [constr] StartX=13.3333 StartY=-8.33333 StartZ=0 EndX=17.3333 EndY=-8.33333 EndZ=0
    g6: ArcOfCircle CenterX=3.33333 CenterY=9.91667 CenterZ=0 NormalX=0 NormalY=0 NormalZ=1 AngleXU=0 Radius=1.6 StartAngle=0 EndAngle=3.14159
    g7: ArcOfCircle CenterX=3.33333 CenterY=-1.58333 CenterZ=0 NormalX=0 NormalY=0 NormalZ=1 AngleXU=0 Radius=1.6 StartAngle=3.14159 EndAngle=6.28319
    g8: LineSegment StartX=1.73333 StartY=9.91667 StartZ=0 EndX=1.73333 EndY=-1.58333 EndZ=0
    g9: LineSegment StartX=4.93333 StartY=9.91667 StartZ=0 EndX=4.93333 EndY=-1.58333 EndZ=0
  constraints (27):
    c: Coincident(g0,g1)
    c: Coincident(g1,g2)
    c: Coincident(g2,g3)
    c: Coincident(g3,g0)
    c: Horizontal(g0)
    c: Horizontal(g2)
    c: Vertical(g1)
    c: Vertical(g3)
    c: PointOnObject(g-4,g0)
    c: PointOnObject(g-4,g2)
    c: Horizontal(g5)
    c: Coincident(g4,g-4)
    c: Equal(g4,g5)
    c: DistanceX(g4,g4) = 4
    c: Horizontal(g4)
    c: Coincident(g2,g4)
    c: Coincident(g5,g-3)
    c: Coincident(g1,g5)
    c: Tangent(g6,g9) = 1.5708
    c: Tangent(g6,g8) = -1.5708
    c: Tangent(g8,g7) = -1.5708
    c: Tangent(g9,g7) = 1.5708
    c: Vertical(g8)
    c: Equal(g6,g7)
    c: Coincident(g6,g-5)
    c: Coincident(g7,g-6)
    c: Coincident(g6,g-5)
FEATURE [PartDesign::Pad] Pad021  label="ClampTopMid_Pad"
  Length = 4
  Length2 = 100
  Placement = pos=(-3.33333,-21.6667,4) rot=(0,0,1;0rad)
  Profile = -> Sketch059
  Type = 0
FEATURE [PartDesign::Body] Body023  label="ClampTopMid_Body"
  Group = -> [DatumPlane016,ShapeBinder054,Sketch059,ShapeBinder055,Pad021]
  Origin = -> Origin044
  Tip = -> Pad021
FEATURE [PartDesign::Plane] DatumPlane017
  MapMode = 5
  Placement = pos=(-3.33333,-21.6667,8) rot=(0,0,1;0rad)
  Support = -> [Pad021]
FEATURE [PartDesign::ShapeBinder] ShapeBinder056
  Placement = pos=(0,0,4) rot=(0,0,1;0rad)
  Support = -> [Sketch058]
FEATURE [PartDesign::ShapeBinder] ShapeBinder057
  Support = -> [Sketch057]
FEATURE [Sketcher::SketchObject] Sketch060  label="ClampTopTop_Sketch"
  ExternalGeometry = -> [ShapeBinder057,ShapeBinder056]
  MapMode = 5
  Placement = pos=(-3.33333,-21.6667,8) rot=(0,0,1;0rad)
  Support = -> [DatumPlane017]
  sketch-geometry (8):
    g0: LineSegment StartX=-6.66667 StartY=16.6667 StartZ=0 EndX=13.3333 EndY=16.6667 EndZ=0
    g1: LineSegment StartX=13.3333 StartY=16.6667 StartZ=0 EndX=13.3333 EndY=-8.33333 EndZ=0
    g2: LineSegment StartX=13.3333 StartY=-8.33333 StartZ=0 EndX=-6.66667 EndY=-8.33333 EndZ=0
    g3: LineSegment StartX=-6.66667 StartY=-8.33333 StartZ=0 EndX=-6.66667 EndY=16.6667 EndZ=0
    g4: ArcOfCircle CenterX=3.33333 CenterY=9.91667 CenterZ=0 NormalX=0 NormalY=0 NormalZ=1 AngleXU=0 Radius=2.75 StartAngle=0 EndAngle=3.14159
    g5: ArcOfCircle CenterX=3.33333 CenterY=-1.58333 CenterZ=0 NormalX=0 NormalY=0 NormalZ=1 AngleXU=0 Radius=2.75 StartAngle=3.14159 EndAngle=6.28319
    g6: LineSegment StartX=0.583333 StartY=9.91667 StartZ=0 EndX=0.583333 EndY=-1.58333 EndZ=0
    g7: LineSegment StartX=6.08333 StartY=9.91667 StartZ=0 EndX=6.08333 EndY=-1.58333 EndZ=0
  constraints (19):
    c: Coincident(g0,g1)
    c: Coincident(g1,g2)
    c: Coincident(g2,g3)
    c: Coincident(g3,g0)
    c: Horizontal(g0)
    c: Horizontal(g2)
    c: Vertical(g1)
    c: Vertical(g3)
    c: Tangent(g4,g7) = 1.5708
    c: Tangent(g4,g6) = -1.5708
    c: Tangent(g6,g5) = -1.5708
    c: Tangent(g7,g5) = 1.5708
    c: Vertical(g6)
    c: Equal(g4,g5)
    c: DistanceX(g4,g4) = 5.5
    c: Coincident(g0,g-3)
    c: Coincident(g1,g-4)
    c: Coincident(g-6,g4)
    c: Coincident(g5,g-5)
FEATURE [PartDesign::Pad] Pad022  label="ClampTopTop_Pad"
  Length = 4
  Length2 = 100
  Placement = pos=(-3.33333,-21.6667,8) rot=(0,0,1;0rad)
  Profile = -> Sketch060
  Type = 0
FEATURE [PartDesign::Body] Body024  label="ClampTopTop_Body"
  Group = -> [DatumPlane017,ShapeBinder056,Sketch060,ShapeBinder057,Pad022]
  Origin = -> Origin045
  Tip = -> Pad022
FEATURE [PartDesign::Plane] DatumPlane018
  MapMode = 5
  Placement = pos=(-10,0,0) rot=(0.57735,-0.57735,-0.57735;2.0944rad)
  Support = -> [Pocket023]
FEATURE [PartDesign::ShapeBinder] ShapeBinder058
  Support = -> [Pocket023]
FEATURE [PartDesign::ShapeBinder] ShapeBinder059
  Placement = pos=(-3.33333,-21.6667,4) rot=(0,0,1;0rad)
  Support = -> [Pad021]
FEATURE [PartDesign::ShapeBinder] ShapeBinder060
  Placement = pos=(-3.33333,-21.6667,8) rot=(0,0,1;0rad)
  Support = -> [Pad022]
FEATURE [Sketcher::SketchObject] Sketch061  label="ClampTopWing_Sketch"
  ExternalGeometry = -> [ShapeBinder060,ShapeBinder059,ShapeBinder058]
  MapMode = 5
  Placement = pos=(-10,0,0) rot=(0.57735,-0.57735,-0.57735;2.0944rad)
  Support = -> [DatumPlane018]
  sketch-geometry (12):
    g0: LineSegment StartX=5 StartY=8 StartZ=0 EndX=30 EndY=8 EndZ=0
    g1: LineSegment StartX=30 StartY=4 StartZ=0 EndX=5 EndY=4 EndZ=0
    g2: LineSegment StartX=5 StartY=4 StartZ=0 EndX=5 EndY=8 EndZ=0
    g3: LineSegment StartX=-2.5 StartY=12 StartZ=0 EndX=30 EndY=12 EndZ=0
    g4: LineSegment StartX=5 StartY=0 StartZ=0 EndX=30 EndY=0 EndZ=0
    g5: LineSegment StartX=30 StartY=0 StartZ=0 EndX=30 EndY=4 EndZ=0
    g6: LineSegment StartX=30 StartY=12 StartZ=0 EndX=30 EndY=8 EndZ=0
    g7: ArcOfCircle CenterX=-2.5 CenterY=9.5 CenterZ=0 NormalX=0 NormalY=0 NormalZ=1 AngleXU=0 Radius=2.5 StartAngle=1.5708 EndAngle=4.71239
    g8: ArcOfCircle CenterX=-2.5 CenterY=3.48214 CenterZ=0 NormalX=0 NormalY=0 NormalZ=1 AngleXU=0 Radius=3.51786 StartAngle=0.0689382 EndAngle=1.5708
    g9: ArcOfCircle CenterX=5 CenterY=4 CenterZ=0 NormalX=0 NormalY=0 NormalZ=1 AngleXU=0 Radius=4 StartAngle=3.21053 EndAngle=4.71239
    g10: LineSegment [constr] StartX=-5 StartY=12 StartZ=0 EndX=-5 EndY=9.5 EndZ=0
    g11: LineSegment [constr] StartX=5 StartY=4 StartZ=0 EndX=1.0095 EndY=3.72447 EndZ=0
  constraints (33):
    c: Coincident(g1,g2)
    c: Coincident(g2,g0)
    c: Horizontal(g0)
    c: Horizontal(g1)
    c: Vertical(g2)
    c: Coincident(g0,g-4)
    c: Coincident(g1,g-4)
    c: Coincident(g0,g-5)
    c: Coincident(g1,g-5)
    c: Coincident(g3,g-3)
    c: Horizontal(g3)
    c: Coincident(g4,g-6)
    c: Horizontal(g4)
    c: Coincident(g5,g4)
    c: Coincident(g5,g1)
    c: Coincident(g6,g0)
    c: Vertical(g6)
    c: Coincident(g3,g6)
    c: DistanceX(g-1,g-6) = 5
    c: Tangent(g4,g9) = -1.5708
    c: Tangent(g3,g7) = 1.5708
    c: Tangent(g7,g8) = 1.5708
    c: Tangent(g8,g9) = 1.5708
    c: Coincident(g4,g-6)
    c: DistanceY(g7,g3) = 5
    c: Angle(g7) = 3.14159
    c: Tangent(g10,g7) = -1.5708
    c: Vertical(g10)
    c: DistanceX(g10,g-3) = 10
    c: PointOnObject(g10,g3)
    c: Coincident(g11,g8)
    c: Distance(g11) = 4
    c: Coincident(g1,g11)
FEATURE [PartDesign::Pad] Pad023  label="ClampTopWing_Pad"
  Length = 4
  Length2 = 100
  Placement = pos=(-10,0,0) rot=(0.57735,-0.57735,-0.57735;2.0944rad)
  Profile = -> Sketch061
  Type = 0
FEATURE [PartDesign::Body] Body025  label="ClampTopWing_Body"
  Group = -> [DatumPlane018,ShapeBinder058,ShapeBinder059,ShapeBinder060,Sketch061,Pad023]
  Origin = -> Origin046
  Tip = -> Pad023
FEATURE [PartDesign::FeatureBase] Clone006  label="ClampTopWing_Clone"
  BaseFeature = -> Body025
  Placement = pos=(24,0,0) rot=(0,0,1;0rad)
FEATURE [TechDraw::DrawViewPart] View020  label="ClampTopBase_View"
  CoarseView = false
  Direction = (0,0,1)
  Focus = 100
  HardHidden = false
  IsoCount = 0
  IsoHidden = false
  IsoVisible = false
  LockPosition = false
  Perspective = false
  Rotation = 0
  ScaleType = 0
  SeamHidden = false
  SeamVisible = false
  SmoothHidden = false
  SmoothVisible = false
  Source = -> [Body022]
  X = 148.5
  Y = 105
FEATURE [TechDraw::DrawPage] Page020  label="ClampTopBase_Page"
  KeepUpdated = true
  ProjectionType = 0
  Template = -> Template020
  Views = -> [View020]
FEATURE [TechDraw::DrawViewPart] View021  label="ClampTopMid_View"
  CoarseView = false
  Direction = (0,0,1)
  Focus = 100
  HardHidden = false
  IsoCount = 0
  IsoHidden = false
  IsoVisible = false
  LockPosition = false
  Perspective = false
  Rotation = 0
  ScaleType = 0
  SeamHidden = false
  SeamVisible = false
  SmoothHidden = false
  SmoothVisible = false
  Source = -> [Body023]
  X = 148.5
  Y = 105
FEATURE [TechDraw::DrawPage] Page021  label="ClampTopMid_Page"
  KeepUpdated = true
  ProjectionType = 0
  Template = -> Template021
  Views = -> [View021]
FEATURE [TechDraw::DrawViewPart] View022  label="ClampTopTop_View"
  CoarseView = false
  Direction = (0,0,1)
  Focus = 100
  HardHidden = false
  IsoCount = 0
  IsoHidden = false
  IsoVisible = false
  LockPosition = false
  Perspective = false
  Rotation = 0
  ScaleType = 0
  SeamHidden = false
  SeamVisible = false
  SmoothHidden = false
  SmoothVisible = false
  Source = -> [Body024]
  X = 148.5
  Y = 105
FEATURE [TechDraw::DrawPage] Page022  label="ClampTopTop_Page"
  KeepUpdated = true
  ProjectionType = 0
  Template = -> Template022
  Views = -> [View022]
FEATURE [TechDraw::DrawViewPart] View023  label="ClampTopWing_View"
  CoarseView = false
  Direction = (1,0,0)
  Focus = 100
  HardHidden = false
  IsoCount = 0
  IsoHidden = false
  IsoVisible = false
  LockPosition = false
  Perspective = false
  Rotation = 0
  ScaleType = 0
  SeamHidden = false
  SeamVisible = false
  SmoothHidden = false
  SmoothVisible = false
  Source = -> [Body025]
  X = 148.5
  Y = 105
FEATURE [TechDraw::DrawPage] Page023  label="ClampTopWing_Page"
  KeepUpdated = true
  ProjectionType = 0
  Template = -> Template023
  Views = -> [View023]
FEATURE [App::Part] Part018  label="ClampTop_Part"
  Group = -> [Template020,Page020,Template021,Page021,Template022,Page022,Template023,Page023,Body022,Body023,Body024,Body025,Clone006]
  License = CC BY 3.0
  LicenseURL = http://creativecommons.org/licenses/by/3.0/
  Origin = -> Origin041
  Placement = pos=(39.5,-28,0) rot=(0,0,1;0rad)
